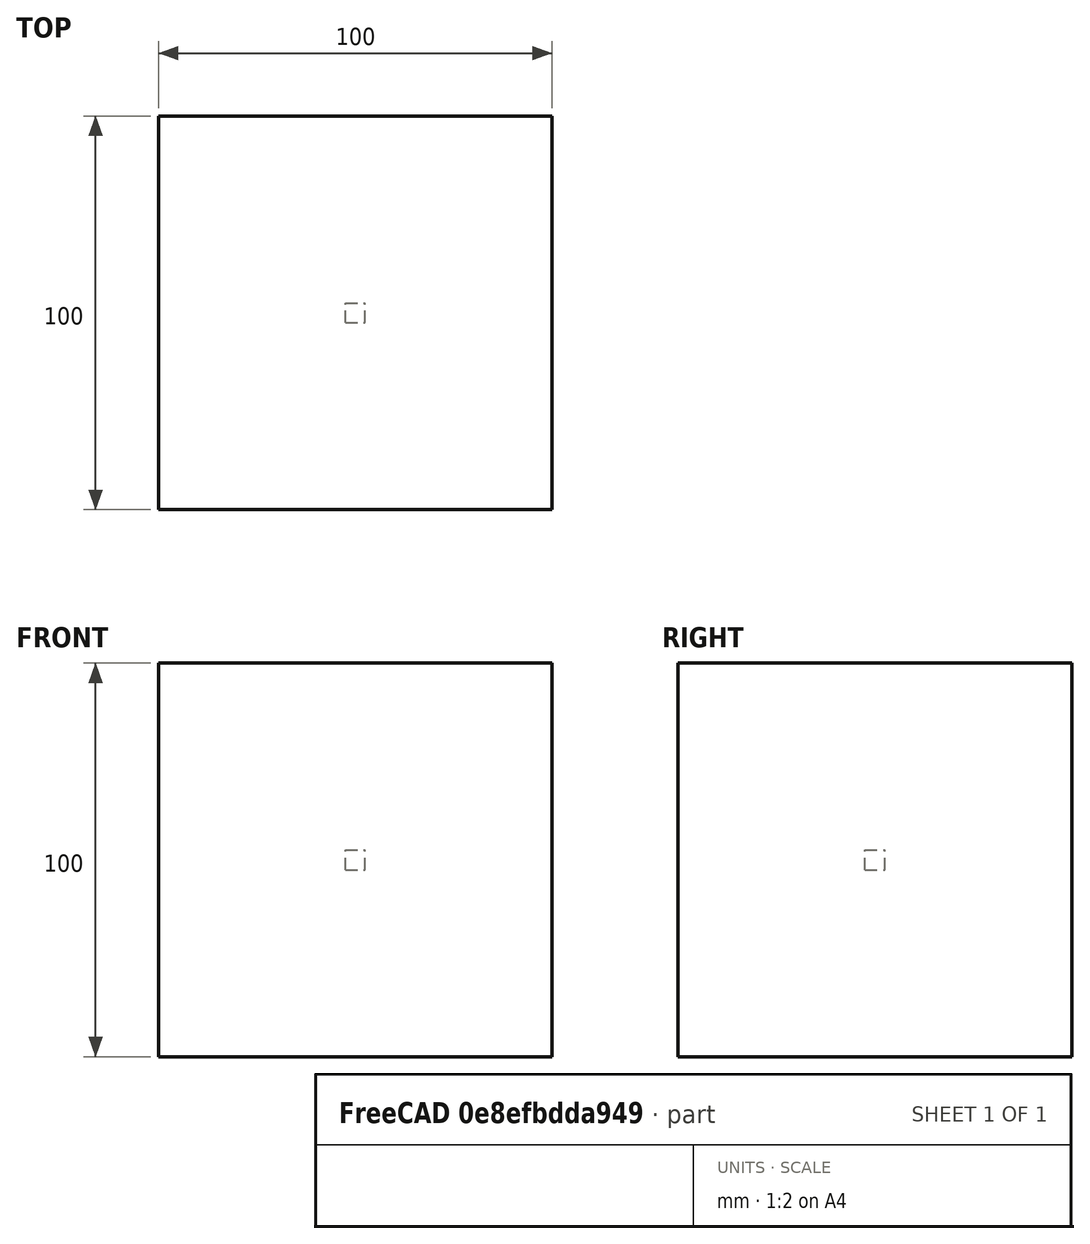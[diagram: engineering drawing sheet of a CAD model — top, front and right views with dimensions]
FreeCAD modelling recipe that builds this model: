
FCSTD DOCUMENT  (FreeCAD 1.0R39109 (Git))
Label: arrayTest-1-a
License: All rights reserved
LicenseURL: http://en.wikipedia.org/wiki/All_rights_reserved
objects: App::DocumentObjectGroupPython×1248, Part::FeaturePython×4, App::Part×4
note: 4 computed .brp shape members not serialized (recipe doc carries the construction recipe); baked Part::Feature solids carry a one-line shape summary decoded from their .brp

FEATURE [App::DocumentObjectGroupPython] HALFPI  # scripted group (container) (typed FeaturePython)
  name = HALFPI
  value = pi/2.
FEATURE [App::DocumentObjectGroupPython] PI  # scripted group (container) (typed FeaturePython)
  name = PI
  value = 1.*pi
FEATURE [App::DocumentObjectGroupPython] TWOPI  # scripted group (container) (typed FeaturePython)
  name = TWOPI
  value = 2.*pi
FEATURE [App::DocumentObjectGroupPython] Constants  # scripted group (container) (typed FeaturePython)
  Group = -> [HALFPI,PI,TWOPI]
FEATURE [App::DocumentObjectGroupPython] Variables  # scripted group (container) (typed FeaturePython)
FEATURE [App::DocumentObjectGroupPython] Quantities  # scripted group (container) (typed FeaturePython)
FEATURE [App::DocumentObjectGroupPython] Isotopes  # scripted group (container) (typed FeaturePython)
FEATURE [App::DocumentObjectGroupPython] Elements  # scripted group (container) (typed FeaturePython)
FEATURE [App::DocumentObjectGroupPython] G4Isotopes  # scripted group (container) (typed FeaturePython)
FEATURE [App::DocumentObjectGroupPython] H_element  # scripted group (container) (typed FeaturePython)
  Z = 1
  atom_value = 1.008
  formula = H
  name = H_element
FEATURE [App::DocumentObjectGroupPython] He_element  # scripted group (container) (typed FeaturePython)
  Z = 2
  atom_value = 4.0026
  formula = He
  name = He_element
FEATURE [App::DocumentObjectGroupPython] Li_element  # scripted group (container) (typed FeaturePython)
  Z = 3
  atom_value = 6.94
  formula = Li
  name = Li_element
FEATURE [App::DocumentObjectGroupPython] Be_element  # scripted group (container) (typed FeaturePython)
  Z = 4
  atom_value = 9.01218
  formula = Be
  name = Be_element
FEATURE [App::DocumentObjectGroupPython] B_element  # scripted group (container) (typed FeaturePython)
  Z = 5
  atom_value = 10.81
  formula = B
  name = B_element
FEATURE [App::DocumentObjectGroupPython] C_element  # scripted group (container) (typed FeaturePython)
  Z = 6
  atom_value = 12.011
  formula = C
  name = C_element
FEATURE [App::DocumentObjectGroupPython] N_element  # scripted group (container) (typed FeaturePython)
  Z = 7
  atom_value = 14.007
  formula = N
  name = N_element
FEATURE [App::DocumentObjectGroupPython] O_element  # scripted group (container) (typed FeaturePython)
  Z = 8
  atom_value = 15.999
  formula = O
  name = O_element
FEATURE [App::DocumentObjectGroupPython] F_element  # scripted group (container) (typed FeaturePython)
  Z = 9
  atom_value = 18.9984
  formula = F
  name = F_element
FEATURE [App::DocumentObjectGroupPython] Ne_element  # scripted group (container) (typed FeaturePython)
  Z = 10
  atom_value = 20.1797
  formula = Ne
  name = Ne_element
FEATURE [App::DocumentObjectGroupPython] Na_element  # scripted group (container) (typed FeaturePython)
  Z = 11
  atom_value = 22.9898
  formula = Na
  name = Na_element
FEATURE [App::DocumentObjectGroupPython] Mg_element  # scripted group (container) (typed FeaturePython)
  Z = 12
  atom_value = 24.305
  formula = Mg
  name = Mg_element
FEATURE [App::DocumentObjectGroupPython] Al_element  # scripted group (container) (typed FeaturePython)
  Z = 13
  atom_value = 26.9815
  formula = Al
  name = Al_element
FEATURE [App::DocumentObjectGroupPython] Si_element  # scripted group (container) (typed FeaturePython)
  Z = 14
  atom_value = 28.085
  formula = Si
  name = Si_element
FEATURE [App::DocumentObjectGroupPython] P_element  # scripted group (container) (typed FeaturePython)
  Z = 15
  atom_value = 30.9738
  formula = P
  name = P_element
FEATURE [App::DocumentObjectGroupPython] S_element  # scripted group (container) (typed FeaturePython)
  Z = 16
  atom_value = 32.06
  formula = S
  name = S_element
FEATURE [App::DocumentObjectGroupPython] Cl_element  # scripted group (container) (typed FeaturePython)
  Z = 17
  atom_value = 35.45
  formula = Cl
  name = Cl_element
FEATURE [App::DocumentObjectGroupPython] Ar_element  # scripted group (container) (typed FeaturePython)
  Z = 18
  atom_value = 39.95
  formula = Ar
  name = Ar_element
FEATURE [App::DocumentObjectGroupPython] K_element  # scripted group (container) (typed FeaturePython)
  Z = 19
  atom_value = 39.0983
  formula = K
  name = K_element
FEATURE [App::DocumentObjectGroupPython] Ca_element  # scripted group (container) (typed FeaturePython)
  Z = 20
  atom_value = 40.078
  formula = Ca
  name = Ca_element
FEATURE [App::DocumentObjectGroupPython] Sc_element  # scripted group (container) (typed FeaturePython)
  Z = 21
  atom_value = 44.9559
  formula = Sc
  name = Sc_element
FEATURE [App::DocumentObjectGroupPython] Ti_element  # scripted group (container) (typed FeaturePython)
  Z = 22
  atom_value = 47.867
  formula = Ti
  name = Ti_element
FEATURE [App::DocumentObjectGroupPython] V_element  # scripted group (container) (typed FeaturePython)
  Z = 23
  atom_value = 50.9415
  formula = V
  name = V_element
FEATURE [App::DocumentObjectGroupPython] Cr_element  # scripted group (container) (typed FeaturePython)
  Z = 24
  atom_value = 51.9961
  formula = Cr
  name = Cr_element
FEATURE [App::DocumentObjectGroupPython] Mn_element  # scripted group (container) (typed FeaturePython)
  Z = 25
  atom_value = 54.938
  formula = Mn
  name = Mn_element
FEATURE [App::DocumentObjectGroupPython] Fe_element  # scripted group (container) (typed FeaturePython)
  Z = 26
  atom_value = 55.845
  formula = Fe
  name = Fe_element
FEATURE [App::DocumentObjectGroupPython] Co_element  # scripted group (container) (typed FeaturePython)
  Z = 27
  atom_value = 58.9332
  formula = Co
  name = Co_element
FEATURE [App::DocumentObjectGroupPython] Ni_element  # scripted group (container) (typed FeaturePython)
  Z = 28
  atom_value = 58.6934
  formula = Ni
  name = Ni_element
FEATURE [App::DocumentObjectGroupPython] Cu_element  # scripted group (container) (typed FeaturePython)
  Z = 29
  atom_value = 63.546
  formula = Cu
  name = Cu_element
FEATURE [App::DocumentObjectGroupPython] Zn_element  # scripted group (container) (typed FeaturePython)
  Z = 30
  atom_value = 65.38
  formula = Zn
  name = Zn_element
FEATURE [App::DocumentObjectGroupPython] Ga_element  # scripted group (container) (typed FeaturePython)
  Z = 31
  atom_value = 69.723
  formula = Ga
  name = Ga_element
FEATURE [App::DocumentObjectGroupPython] Ge_element  # scripted group (container) (typed FeaturePython)
  Z = 32
  atom_value = 72.63
  formula = Ge
  name = Ge_element
FEATURE [App::DocumentObjectGroupPython] As_element  # scripted group (container) (typed FeaturePython)
  Z = 33
  atom_value = 74.9216
  formula = As
  name = As_element
FEATURE [App::DocumentObjectGroupPython] Se_element  # scripted group (container) (typed FeaturePython)
  Z = 34
  atom_value = 78.971
  formula = Se
  name = Se_element
FEATURE [App::DocumentObjectGroupPython] Br_element  # scripted group (container) (typed FeaturePython)
  Z = 35
  atom_value = 79.904
  formula = Br
  name = Br_element
FEATURE [App::DocumentObjectGroupPython] Kr_element  # scripted group (container) (typed FeaturePython)
  Z = 36
  atom_value = 83.798
  formula = Kr
  name = Kr_element
FEATURE [App::DocumentObjectGroupPython] Rb_element  # scripted group (container) (typed FeaturePython)
  Z = 37
  atom_value = 85.4678
  formula = Rb
  name = Rb_element
FEATURE [App::DocumentObjectGroupPython] Sr_element  # scripted group (container) (typed FeaturePython)
  Z = 38
  atom_value = 87.62
  formula = Sr
  name = Sr_element
FEATURE [App::DocumentObjectGroupPython] Y_element  # scripted group (container) (typed FeaturePython)
  Z = 39
  atom_value = 88.9058
  formula = Y
  name = Y_element
FEATURE [App::DocumentObjectGroupPython] Zr_element  # scripted group (container) (typed FeaturePython)
  Z = 40
  atom_value = 91.224
  formula = Zr
  name = Zr_element
FEATURE [App::DocumentObjectGroupPython] Nb_element  # scripted group (container) (typed FeaturePython)
  Z = 41
  atom_value = 92.9064
  formula = Nb
  name = Nb_element
FEATURE [App::DocumentObjectGroupPython] Mo_element  # scripted group (container) (typed FeaturePython)
  Z = 42
  atom_value = 95.95
  formula = Mo
  name = Mo_element
FEATURE [App::DocumentObjectGroupPython] Tc_element  # scripted group (container) (typed FeaturePython)
  Z = 43
  atom_value = 97
  formula = Tc
  name = Tc_element
FEATURE [App::DocumentObjectGroupPython] Ru_element  # scripted group (container) (typed FeaturePython)
  Z = 44
  atom_value = 101.07
  formula = Ru
  name = Ru_element
FEATURE [App::DocumentObjectGroupPython] Rh_element  # scripted group (container) (typed FeaturePython)
  Z = 45
  atom_value = 102.905
  formula = Rh
  name = Rh_element
FEATURE [App::DocumentObjectGroupPython] Pd_element  # scripted group (container) (typed FeaturePython)
  Z = 46
  atom_value = 106.42
  formula = Pd
  name = Pd_element
FEATURE [App::DocumentObjectGroupPython] Ag_element  # scripted group (container) (typed FeaturePython)
  Z = 47
  atom_value = 107.868
  formula = Ag
  name = Ag_element
FEATURE [App::DocumentObjectGroupPython] Cd_element  # scripted group (container) (typed FeaturePython)
  Z = 48
  atom_value = 112.414
  formula = Cd
  name = Cd_element
FEATURE [App::DocumentObjectGroupPython] In_element  # scripted group (container) (typed FeaturePython)
  Z = 49
  atom_value = 114.818
  formula = In
  name = In_element
FEATURE [App::DocumentObjectGroupPython] Sn_element  # scripted group (container) (typed FeaturePython)
  Z = 50
  atom_value = 118.71
  formula = Sn
  name = Sn_element
FEATURE [App::DocumentObjectGroupPython] Sb_element  # scripted group (container) (typed FeaturePython)
  Z = 51
  atom_value = 121.76
  formula = Sb
  name = Sb_element
FEATURE [App::DocumentObjectGroupPython] Te_element  # scripted group (container) (typed FeaturePython)
  Z = 52
  atom_value = 127.6
  formula = Te
  name = Te_element
FEATURE [App::DocumentObjectGroupPython] I_element  # scripted group (container) (typed FeaturePython)
  Z = 53
  atom_value = 126.904
  formula = I
  name = I_element
FEATURE [App::DocumentObjectGroupPython] Xe_element  # scripted group (container) (typed FeaturePython)
  Z = 54
  atom_value = 131.293
  formula = Xe
  name = Xe_element
FEATURE [App::DocumentObjectGroupPython] Cs_element  # scripted group (container) (typed FeaturePython)
  Z = 55
  atom_value = 132.905
  formula = Cs
  name = Cs_element
FEATURE [App::DocumentObjectGroupPython] Ba_element  # scripted group (container) (typed FeaturePython)
  Z = 56
  atom_value = 137.327
  formula = Ba
  name = Ba_element
FEATURE [App::DocumentObjectGroupPython] La_element  # scripted group (container) (typed FeaturePython)
  Z = 57
  atom_value = 138.905
  formula = La
  name = La_element
FEATURE [App::DocumentObjectGroupPython] Ce_element  # scripted group (container) (typed FeaturePython)
  Z = 58
  atom_value = 140.116
  formula = Ce
  name = Ce_element
FEATURE [App::DocumentObjectGroupPython] Pr_element  # scripted group (container) (typed FeaturePython)
  Z = 59
  atom_value = 140.908
  formula = Pr
  name = Pr_element
FEATURE [App::DocumentObjectGroupPython] Nd_element  # scripted group (container) (typed FeaturePython)
  Z = 60
  atom_value = 144.242
  formula = Nd
  name = Nd_element
FEATURE [App::DocumentObjectGroupPython] Pm_element  # scripted group (container) (typed FeaturePython)
  Z = 61
  atom_value = 145
  formula = Pm
  name = Pm_element
FEATURE [App::DocumentObjectGroupPython] Sm_element  # scripted group (container) (typed FeaturePython)
  Z = 62
  atom_value = 150.36
  formula = Sm
  name = Sm_element
FEATURE [App::DocumentObjectGroupPython] Eu_element  # scripted group (container) (typed FeaturePython)
  Z = 63
  atom_value = 151.964
  formula = Eu
  name = Eu_element
FEATURE [App::DocumentObjectGroupPython] Gd_element  # scripted group (container) (typed FeaturePython)
  Z = 64
  atom_value = 157.25
  formula = Gd
  name = Gd_element
FEATURE [App::DocumentObjectGroupPython] Tb_element  # scripted group (container) (typed FeaturePython)
  Z = 65
  atom_value = 158.925
  formula = Tb
  name = Tb_element
FEATURE [App::DocumentObjectGroupPython] Dy_element  # scripted group (container) (typed FeaturePython)
  Z = 66
  atom_value = 162.5
  formula = Dy
  name = Dy_element
FEATURE [App::DocumentObjectGroupPython] Ho_element  # scripted group (container) (typed FeaturePython)
  Z = 67
  atom_value = 164.93
  formula = Ho
  name = Ho_element
FEATURE [App::DocumentObjectGroupPython] Er_element  # scripted group (container) (typed FeaturePython)
  Z = 68
  atom_value = 167.259
  formula = Er
  name = Er_element
FEATURE [App::DocumentObjectGroupPython] Tm_element  # scripted group (container) (typed FeaturePython)
  Z = 69
  atom_value = 168.934
  formula = Tm
  name = Tm_element
FEATURE [App::DocumentObjectGroupPython] Yb_element  # scripted group (container) (typed FeaturePython)
  Z = 70
  atom_value = 173.045
  formula = Yb
  name = Yb_element
FEATURE [App::DocumentObjectGroupPython] Lu_element  # scripted group (container) (typed FeaturePython)
  Z = 71
  atom_value = 174.967
  formula = Lu
  name = Lu_element
FEATURE [App::DocumentObjectGroupPython] Hf_element  # scripted group (container) (typed FeaturePython)
  Z = 72
  atom_value = 178.49
  formula = Hf
  name = Hf_element
FEATURE [App::DocumentObjectGroupPython] Ta_element  # scripted group (container) (typed FeaturePython)
  Z = 73
  atom_value = 180.948
  formula = Ta
  name = Ta_element
FEATURE [App::DocumentObjectGroupPython] W_element  # scripted group (container) (typed FeaturePython)
  Z = 74
  atom_value = 183.84
  formula = W
  name = W_element
FEATURE [App::DocumentObjectGroupPython] Re_element  # scripted group (container) (typed FeaturePython)
  Z = 75
  atom_value = 186.207
  formula = Re
  name = Re_element
FEATURE [App::DocumentObjectGroupPython] Os_element  # scripted group (container) (typed FeaturePython)
  Z = 76
  atom_value = 190.23
  formula = Os
  name = Os_element
FEATURE [App::DocumentObjectGroupPython] Ir_element  # scripted group (container) (typed FeaturePython)
  Z = 77
  atom_value = 192.217
  formula = Ir
  name = Ir_element
FEATURE [App::DocumentObjectGroupPython] Pt_element  # scripted group (container) (typed FeaturePython)
  Z = 78
  atom_value = 195.084
  formula = Pt
  name = Pt_element
FEATURE [App::DocumentObjectGroupPython] Au_element  # scripted group (container) (typed FeaturePython)
  Z = 79
  atom_value = 196.967
  formula = Au
  name = Au_element
FEATURE [App::DocumentObjectGroupPython] Hg_element  # scripted group (container) (typed FeaturePython)
  Z = 80
  atom_value = 200.592
  formula = Hg
  name = Hg_element
FEATURE [App::DocumentObjectGroupPython] Tl_element  # scripted group (container) (typed FeaturePython)
  Z = 81
  atom_value = 204.38
  formula = Tl
  name = Tl_element
FEATURE [App::DocumentObjectGroupPython] Pb_element  # scripted group (container) (typed FeaturePython)
  Z = 82
  atom_value = 207.2
  formula = Pb
  name = Pb_element
FEATURE [App::DocumentObjectGroupPython] Bi_element  # scripted group (container) (typed FeaturePython)
  Z = 83
  atom_value = 208.98
  formula = Bi
  name = Bi_element
FEATURE [App::DocumentObjectGroupPython] Po_element  # scripted group (container) (typed FeaturePython)
  Z = 84
  atom_value = 209
  formula = Po
  name = Po_element
FEATURE [App::DocumentObjectGroupPython] At_element  # scripted group (container) (typed FeaturePython)
  Z = 85
  atom_value = 210
  formula = At
  name = At_element
FEATURE [App::DocumentObjectGroupPython] Rn_element  # scripted group (container) (typed FeaturePython)
  Z = 86
  atom_value = 222
  formula = Rn
  name = Rn_element
FEATURE [App::DocumentObjectGroupPython] Fr_element  # scripted group (container) (typed FeaturePython)
  Z = 87
  atom_value = 223
  formula = Fr
  name = Fr_element
FEATURE [App::DocumentObjectGroupPython] Ra_element  # scripted group (container) (typed FeaturePython)
  Z = 88
  atom_value = 226
  formula = Ra
  name = Ra_element
FEATURE [App::DocumentObjectGroupPython] Ac_element  # scripted group (container) (typed FeaturePython)
  Z = 89
  atom_value = 227
  formula = Ac
  name = Ac_element
FEATURE [App::DocumentObjectGroupPython] Th_element  # scripted group (container) (typed FeaturePython)
  Z = 90
  atom_value = 232.038
  formula = Th
  name = Th_element
FEATURE [App::DocumentObjectGroupPython] Pa_element  # scripted group (container) (typed FeaturePython)
  Z = 91
  atom_value = 231.036
  formula = Pa
  name = Pa_element
FEATURE [App::DocumentObjectGroupPython] U_element  # scripted group (container) (typed FeaturePython)
  Z = 92
  atom_value = 238.029
  formula = U
  name = U_element
FEATURE [App::DocumentObjectGroupPython] Np_element  # scripted group (container) (typed FeaturePython)
  Z = 93
  atom_value = 237
  formula = Np
  name = Np_element
FEATURE [App::DocumentObjectGroupPython] Pu_element  # scripted group (container) (typed FeaturePython)
  Z = 94
  atom_value = 244
  formula = Pu
  name = Pu_element
FEATURE [App::DocumentObjectGroupPython] Am_element  # scripted group (container) (typed FeaturePython)
  Z = 95
  atom_value = 243
  formula = Am
  name = Am_element
FEATURE [App::DocumentObjectGroupPython] Cm_element  # scripted group (container) (typed FeaturePython)
  Z = 96
  atom_value = 247
  formula = Cm
  name = Cm_element
FEATURE [App::DocumentObjectGroupPython] Bk_element  # scripted group (container) (typed FeaturePython)
  Z = 97
  atom_value = 247
  formula = Bk
  name = Bk_element
FEATURE [App::DocumentObjectGroupPython] Cf_element  # scripted group (container) (typed FeaturePython)
  Z = 98
  atom_value = 251
  formula = Cf
  name = Cf_element
FEATURE [App::DocumentObjectGroupPython] G4Elements  # scripted group (container) (typed FeaturePython)
  Group = -> [H_element,He_element,Li_element,Be_element,B_element,C_element,N_element,O_element,F_element,Ne_element,Na_element,Mg_element,Al_element,Si_element,P_element,S_element,Cl_element,Ar_element,K_element,Ca_element,Sc_element,Ti_element,V_element,Cr_element,Mn_element,Fe_element,Co_element,Ni_element,Cu_element,Zn_element,Ga_element,Ge_element,As_element,Se_element,Br_element,Kr_element,Rb_element,+61 more]
FEATURE [App::DocumentObjectGroupPython] H_element001  label="H_element : 0.101"  # scripted group (container) (typed FeaturePython)
  n = 0.101327
FEATURE [App::DocumentObjectGroupPython] C_element001  label="C_element : 0.775"  # scripted group (container) (typed FeaturePython)
  n = 0.7755
FEATURE [App::DocumentObjectGroupPython] N_element001  label="N_element : 0.035"  # scripted group (container) (typed FeaturePython)
  n = 0.035057
FEATURE [App::DocumentObjectGroupPython] O_element001  label="O_element : 0.052"  # scripted group (container) (typed FeaturePython)
  n = 0.0523159
FEATURE [App::DocumentObjectGroupPython] F_element001  label="F_element : 0.017"  # scripted group (container) (typed FeaturePython)
  n = 0.017422
FEATURE [App::DocumentObjectGroupPython] Ca_element001  label="Ca_element : 0.018"  # scripted group (container) (typed FeaturePython)
  n = 0.018378
FEATURE [App::DocumentObjectGroupPython] G4_A_150_TISSUE  label="G4_A-150_TISSUE"  # scripted group (container) (typed FeaturePython)
  Dunit = g/cm3
  Dvalue = 1.127
  Group = -> [H_element001,C_element001,N_element001,O_element001,F_element001,Ca_element001]
  conduct = 2
  density = 1
  expand = 3
  formula = G4_A-150_TISSUE
  name = G4_A-150_TISSUE
  specific = 4
FEATURE [App::DocumentObjectGroupPython] C_element002  label="C_element : 3"  # scripted group (container) (typed FeaturePython)
  n = 3
  ref = C_element
FEATURE [App::DocumentObjectGroupPython] H_element002  label="H_element : 6"  # scripted group (container) (typed FeaturePython)
  n = 6
  ref = H_element
FEATURE [App::DocumentObjectGroupPython] O_element002  label="O_element : 1"  # scripted group (container) (typed FeaturePython)
  n = 1
  ref = O_element
FEATURE [App::DocumentObjectGroupPython] G4_ACETONE  # scripted group (container) (typed FeaturePython)
  Dunit = g/cm3
  Dvalue = 0.7899
  Group = -> [C_element002,H_element002,O_element002]
  conduct = 2
  density = 1
  expand = 3
  formula = G4_ACETONE
  name = G4_ACETONE
  specific = 4
FEATURE [App::DocumentObjectGroupPython] C_element003  label="C_element : 2"  # scripted group (container) (typed FeaturePython)
  n = 2
  ref = C_element
FEATURE [App::DocumentObjectGroupPython] H_element003  label="H_element : 2"  # scripted group (container) (typed FeaturePython)
  n = 2
  ref = H_element
FEATURE [App::DocumentObjectGroupPython] G4_ACETYLENE  # scripted group (container) (typed FeaturePython)
  Dunit = g/cm3
  Dvalue = 0.0010967
  Group = -> [C_element003,H_element003]
  conduct = 2
  density = 1
  expand = 3
  formula = G4_ACETYLENE
  name = G4_ACETYLENE
  specific = 4
FEATURE [App::DocumentObjectGroupPython] C_element004  label="C_element : 5"  # scripted group (container) (typed FeaturePython)
  n = 5
  ref = C_element
FEATURE [App::DocumentObjectGroupPython] H_element004  label="H_element : 5"  # scripted group (container) (typed FeaturePython)
  n = 5
  ref = H_element
FEATURE [App::DocumentObjectGroupPython] N_element002  label="N_element : 5"  # scripted group (container) (typed FeaturePython)
  n = 5
  ref = N_element
FEATURE [App::DocumentObjectGroupPython] G4_ADENINE  # scripted group (container) (typed FeaturePython)
  Dunit = g/cm3
  Dvalue = 1.6
  Group = -> [C_element004,H_element004,N_element002]
  conduct = 2
  density = 1
  expand = 3
  formula = G4_ADENINE
  name = G4_ADENINE
  specific = 4
FEATURE [App::DocumentObjectGroupPython] H_element005  label="H_element : 0.114"  # scripted group (container) (typed FeaturePython)
  n = 0.114
FEATURE [App::DocumentObjectGroupPython] C_element005  label="C_element : 0.598"  # scripted group (container) (typed FeaturePython)
  n = 0.598
FEATURE [App::DocumentObjectGroupPython] N_element003  label="N_element : 0.007"  # scripted group (container) (typed FeaturePython)
  n = 0.007
FEATURE [App::DocumentObjectGroupPython] O_element003  label="O_element : 0.278"  # scripted group (container) (typed FeaturePython)
  n = 0.278
FEATURE [App::DocumentObjectGroupPython] Na_element001  label="Na_element : 0.001"  # scripted group (container) (typed FeaturePython)
  n = 0.001
FEATURE [App::DocumentObjectGroupPython] S_element001  label="S_element : 0.001"  # scripted group (container) (typed FeaturePython)
  n = 0.001
FEATURE [App::DocumentObjectGroupPython] Cl_element001  label="Cl_element : 0.001"  # scripted group (container) (typed FeaturePython)
  n = 0.001
FEATURE [App::DocumentObjectGroupPython] G4_ADIPOSE_TISSUE_ICRP  # scripted group (container) (typed FeaturePython)
  Dunit = g/cm3
  Dvalue = 0.95
  Group = -> [H_element005,C_element005,N_element003,O_element003,Na_element001,S_element001,Cl_element001]
  conduct = 2
  density = 1
  expand = 3
  formula = G4_ADIPOSE_TISSUE_ICRP
  name = G4_ADIPOSE_TISSUE_ICRP
  specific = 4
FEATURE [App::DocumentObjectGroupPython] C_element006  label="C_element : 0.000"  # scripted group (container) (typed FeaturePython)
  n = 0.000124
FEATURE [App::DocumentObjectGroupPython] N_element004  label="N_element : 0.755"  # scripted group (container) (typed FeaturePython)
  n = 0.755268
FEATURE [App::DocumentObjectGroupPython] O_element004  label="O_element : 0.232"  # scripted group (container) (typed FeaturePython)
  n = 0.231781
FEATURE [App::DocumentObjectGroupPython] Ar_element001  label="Ar_element : 0.013"  # scripted group (container) (typed FeaturePython)
  n = 0.012827
FEATURE [App::DocumentObjectGroupPython] G4_AIR  # scripted group (container) (typed FeaturePython)
  Dunit = g/cm3
  Dvalue = 0.00120479
  Group = -> [C_element006,N_element004,O_element004,Ar_element001]
  conduct = 2
  density = 1
  expand = 3
  formula = G4_AIR
  name = G4_AIR
  specific = 4
FEATURE [App::DocumentObjectGroupPython] C_element007  label="C_element : 006"  # scripted group (container) (typed FeaturePython)
  n = 3
  ref = C_element
FEATURE [App::DocumentObjectGroupPython] H_element006  label="H_element : 7"  # scripted group (container) (typed FeaturePython)
  n = 7
  ref = H_element
FEATURE [App::DocumentObjectGroupPython] N_element005  label="N_element : 1"  # scripted group (container) (typed FeaturePython)
  n = 1
  ref = N_element
FEATURE [App::DocumentObjectGroupPython] O_element005  label="O_element : 2"  # scripted group (container) (typed FeaturePython)
  n = 2
  ref = O_element
FEATURE [App::DocumentObjectGroupPython] G4_ALANINE  # scripted group (container) (typed FeaturePython)
  Dunit = g/cm3
  Dvalue = 1.42
  Group = -> [C_element007,H_element006,N_element005,O_element005]
  conduct = 2
  density = 1
  expand = 3
  formula = G4_ALANINE
  name = G4_ALANINE
  specific = 4
FEATURE [App::DocumentObjectGroupPython] Al_element001  label="Al_element : 2"  # scripted group (container) (typed FeaturePython)
  n = 2
  ref = Al_element
FEATURE [App::DocumentObjectGroupPython] O_element006  label="O_element : 3"  # scripted group (container) (typed FeaturePython)
  n = 3
  ref = O_element
FEATURE [App::DocumentObjectGroupPython] G4_ALUMINUM_OXIDE  # scripted group (container) (typed FeaturePython)
  Dunit = g/cm3
  Dvalue = 3.97
  Group = -> [Al_element001,O_element006]
  conduct = 2
  density = 1
  expand = 3
  formula = G4_ALUMINUM_OXIDE
  name = G4_ALUMINUM_OXIDE
  specific = 4
FEATURE [App::DocumentObjectGroupPython] H_element007  label="H_element : 0.106"  # scripted group (container) (typed FeaturePython)
  n = 0.10593
FEATURE [App::DocumentObjectGroupPython] C_element008  label="C_element : 0.789"  # scripted group (container) (typed FeaturePython)
  n = 0.788974
FEATURE [App::DocumentObjectGroupPython] O_element007  label="O_element : 0.105"  # scripted group (container) (typed FeaturePython)
  n = 0.105096
FEATURE [App::DocumentObjectGroupPython] G4_AMBER  # scripted group (container) (typed FeaturePython)
  Dunit = g/cm3
  Dvalue = 1.1
  Group = -> [H_element007,C_element008,O_element007]
  conduct = 2
  density = 1
  expand = 3
  formula = G4_AMBER
  name = G4_AMBER
  specific = 4
FEATURE [App::DocumentObjectGroupPython] N_element006  label="N_element : 006"  # scripted group (container) (typed FeaturePython)
  n = 1
  ref = N_element
FEATURE [App::DocumentObjectGroupPython] H_element008  label="H_element : 3"  # scripted group (container) (typed FeaturePython)
  n = 3
  ref = H_element
FEATURE [App::DocumentObjectGroupPython] G4_AMMONIA  # scripted group (container) (typed FeaturePython)
  Dunit = g/cm3
  Dvalue = 0.000826019
  Group = -> [N_element006,H_element008]
  conduct = 2
  density = 1
  expand = 3
  formula = G4_AMMONIA
  name = G4_AMMONIA
  specific = 4
FEATURE [App::DocumentObjectGroupPython] C_element009  label="C_element : 6"  # scripted group (container) (typed FeaturePython)
  n = 6
  ref = C_element
FEATURE [App::DocumentObjectGroupPython] H_element009  label="H_element : 008"  # scripted group (container) (typed FeaturePython)
  n = 7
  ref = H_element
FEATURE [App::DocumentObjectGroupPython] N_element007  label="N_element : 007"  # scripted group (container) (typed FeaturePython)
  n = 1
  ref = N_element
FEATURE [App::DocumentObjectGroupPython] G4_ANILINE  # scripted group (container) (typed FeaturePython)
  Dunit = g/cm3
  Dvalue = 1.0235
  Group = -> [C_element009,H_element009,N_element007]
  conduct = 2
  density = 1
  expand = 3
  formula = G4_ANILINE
  name = G4_ANILINE
  specific = 4
FEATURE [App::DocumentObjectGroupPython] C_element010  label="C_element : 14"  # scripted group (container) (typed FeaturePython)
  n = 14
  ref = C_element
FEATURE [App::DocumentObjectGroupPython] H_element010  label="H_element : 10"  # scripted group (container) (typed FeaturePython)
  n = 10
  ref = H_element
FEATURE [App::DocumentObjectGroupPython] G4_ANTHRACENE  # scripted group (container) (typed FeaturePython)
  Dunit = g/cm3
  Dvalue = 1.283
  Group = -> [C_element010,H_element010]
  conduct = 2
  density = 1
  expand = 3
  formula = G4_ANTHRACENE
  name = G4_ANTHRACENE
  specific = 4
FEATURE [App::DocumentObjectGroupPython] H_element011  label="H_element : 0.065"  # scripted group (container) (typed FeaturePython)
  n = 0.0654709
FEATURE [App::DocumentObjectGroupPython] C_element011  label="C_element : 0.537"  # scripted group (container) (typed FeaturePython)
  n = 0.536944
FEATURE [App::DocumentObjectGroupPython] N_element008  label="N_element : 0.021"  # scripted group (container) (typed FeaturePython)
  n = 0.0215
FEATURE [App::DocumentObjectGroupPython] O_element008  label="O_element : 0.032"  # scripted group (container) (typed FeaturePython)
  n = 0.032085
FEATURE [App::DocumentObjectGroupPython] F_element002  label="F_element : 0.167"  # scripted group (container) (typed FeaturePython)
  n = 0.167411
FEATURE [App::DocumentObjectGroupPython] Ca_element002  label="Ca_element : 0.177"  # scripted group (container) (typed FeaturePython)
  n = 0.176589
FEATURE [App::DocumentObjectGroupPython] G4_B_100_BONE  label="G4_B-100_BONE"  # scripted group (container) (typed FeaturePython)
  Dunit = g/cm3
  Dvalue = 1.45
  Group = -> [H_element011,C_element011,N_element008,O_element008,F_element002,Ca_element002]
  conduct = 2
  density = 1
  expand = 3
  formula = G4_B-100_BONE
  name = G4_B-100_BONE
  specific = 4
FEATURE [App::DocumentObjectGroupPython] H_element012  label="H_element : 0.057"  # scripted group (container) (typed FeaturePython)
  n = 0.057441
FEATURE [App::DocumentObjectGroupPython] C_element012  label="C_element : 0.790"  # scripted group (container) (typed FeaturePython)
  n = 0.774591
FEATURE [App::DocumentObjectGroupPython] O_element009  label="O_element : 0.168"  # scripted group (container) (typed FeaturePython)
  n = 0.167968
FEATURE [App::DocumentObjectGroupPython] G4_BAKELITE  # scripted group (container) (typed FeaturePython)
  Dunit = g/cm3
  Dvalue = 1.25
  Group = -> [H_element012,C_element012,O_element009]
  conduct = 2
  density = 1
  expand = 3
  formula = G4_BAKELITE
  name = G4_BAKELITE
  specific = 4
FEATURE [App::DocumentObjectGroupPython] Ba_element001  label="Ba_element : 1"  # scripted group (container) (typed FeaturePython)
  n = 1
  ref = Ba_element
FEATURE [App::DocumentObjectGroupPython] F_element003  label="F_element : 2"  # scripted group (container) (typed FeaturePython)
  n = 2
  ref = F_element
FEATURE [App::DocumentObjectGroupPython] G4_BARIUM_FLUORIDE  # scripted group (container) (typed FeaturePython)
  Dunit = g/cm3
  Dvalue = 4.89
  Group = -> [Ba_element001,F_element003]
  conduct = 2
  density = 1
  expand = 3
  formula = G4_BARIUM_FLUORIDE
  name = G4_BARIUM_FLUORIDE
  specific = 4
FEATURE [App::DocumentObjectGroupPython] Ba_element002  label="Ba_element : 002"  # scripted group (container) (typed FeaturePython)
  n = 1
  ref = Ba_element
FEATURE [App::DocumentObjectGroupPython] S_element002  label="S_element : 1"  # scripted group (container) (typed FeaturePython)
  n = 1
  ref = S_element
FEATURE [App::DocumentObjectGroupPython] O_element010  label="O_element : 4"  # scripted group (container) (typed FeaturePython)
  n = 4
  ref = O_element
FEATURE [App::DocumentObjectGroupPython] G4_BARIUM_SULFATE  # scripted group (container) (typed FeaturePython)
  Dunit = g/cm3
  Dvalue = 4.5
  Group = -> [Ba_element002,S_element002,O_element010]
  conduct = 2
  density = 1
  expand = 3
  formula = G4_BARIUM_SULFATE
  name = G4_BARIUM_SULFATE
  specific = 4
FEATURE [App::DocumentObjectGroupPython] C_element013  label="C_element : 007"  # scripted group (container) (typed FeaturePython)
  n = 6
  ref = C_element
FEATURE [App::DocumentObjectGroupPython] H_element013  label="H_element : 009"  # scripted group (container) (typed FeaturePython)
  n = 6
  ref = H_element
FEATURE [App::DocumentObjectGroupPython] G4_BENZENE  # scripted group (container) (typed FeaturePython)
  Dunit = g/cm3
  Dvalue = 0.87865
  Group = -> [C_element013,H_element013]
  conduct = 2
  density = 1
  expand = 3
  formula = G4_BENZENE
  name = G4_BENZENE
  specific = 4
FEATURE [App::DocumentObjectGroupPython] Be_element001  label="Be_element : 1"  # scripted group (container) (typed FeaturePython)
  n = 1
  ref = Be_element
FEATURE [App::DocumentObjectGroupPython] O_element011  label="O_element : 005"  # scripted group (container) (typed FeaturePython)
  n = 1
  ref = O_element
FEATURE [App::DocumentObjectGroupPython] G4_BERYLLIUM_OXIDE  # scripted group (container) (typed FeaturePython)
  Dunit = g/cm3
  Dvalue = 3.01
  Group = -> [Be_element001,O_element011]
  conduct = 2
  density = 1
  expand = 3
  formula = G4_BERYLLIUM_OXIDE
  name = G4_BERYLLIUM_OXIDE
  specific = 4
FEATURE [App::DocumentObjectGroupPython] Bi_element001  label="Bi_element : 4"  # scripted group (container) (typed FeaturePython)
  n = 4
  ref = Bi_element
FEATURE [App::DocumentObjectGroupPython] Ge_element001  label="Ge_element : 3"  # scripted group (container) (typed FeaturePython)
  n = 3
  ref = Ge_element
FEATURE [App::DocumentObjectGroupPython] O_element012  label="O_element : 12"  # scripted group (container) (typed FeaturePython)
  n = 12
  ref = O_element
FEATURE [App::DocumentObjectGroupPython] G4_BGO  # scripted group (container) (typed FeaturePython)
  Dunit = g/cm3
  Dvalue = 7.13
  Group = -> [Bi_element001,Ge_element001,O_element012]
  conduct = 2
  density = 1
  expand = 3
  formula = G4_BGO
  name = G4_BGO
  specific = 4
FEATURE [App::DocumentObjectGroupPython] H_element014  label="H_element : 0.102"  # scripted group (container) (typed FeaturePython)
  n = 0.102
FEATURE [App::DocumentObjectGroupPython] C_element014  label="C_element : 0.110"  # scripted group (container) (typed FeaturePython)
  n = 0.11
FEATURE [App::DocumentObjectGroupPython] N_element009  label="N_element : 0.033"  # scripted group (container) (typed FeaturePython)
  n = 0.033
FEATURE [App::DocumentObjectGroupPython] O_element013  label="O_element : 0.745"  # scripted group (container) (typed FeaturePython)
  n = 0.745
FEATURE [App::DocumentObjectGroupPython] Na_element002  label="Na_element : 0.002"  # scripted group (container) (typed FeaturePython)
  n = 0.001
FEATURE [App::DocumentObjectGroupPython] P_element001  label="P_element : 0.001"  # scripted group (container) (typed FeaturePython)
  n = 0.001
FEATURE [App::DocumentObjectGroupPython] S_element003  label="S_element : 0.002"  # scripted group (container) (typed FeaturePython)
  n = 0.002
FEATURE [App::DocumentObjectGroupPython] Cl_element002  label="Cl_element : 0.003"  # scripted group (container) (typed FeaturePython)
  n = 0.003
FEATURE [App::DocumentObjectGroupPython] K_element001  label="K_element : 0.002"  # scripted group (container) (typed FeaturePython)
  n = 0.002
FEATURE [App::DocumentObjectGroupPython] Fe_element001  label="Fe_element : 0.001"  # scripted group (container) (typed FeaturePython)
  n = 0.001
FEATURE [App::DocumentObjectGroupPython] G4_BLOOD_ICRP  # scripted group (container) (typed FeaturePython)
  Dunit = g/cm3
  Dvalue = 1.06
  Group = -> [H_element014,C_element014,N_element009,O_element013,Na_element002,P_element001,S_element003,Cl_element002,K_element001,Fe_element001]
  conduct = 2
  density = 1
  expand = 3
  formula = G4_BLOOD_ICRP
  name = G4_BLOOD_ICRP
  specific = 4
FEATURE [App::DocumentObjectGroupPython] H_element015  label="H_element : 0.064"  # scripted group (container) (typed FeaturePython)
  n = 0.064
FEATURE [App::DocumentObjectGroupPython] C_element015  label="C_element : 0.278"  # scripted group (container) (typed FeaturePython)
  n = 0.278
FEATURE [App::DocumentObjectGroupPython] N_element010  label="N_element : 0.027"  # scripted group (container) (typed FeaturePython)
  n = 0.027
FEATURE [App::DocumentObjectGroupPython] O_element014  label="O_element : 0.410"  # scripted group (container) (typed FeaturePython)
  n = 0.41
FEATURE [App::DocumentObjectGroupPython] Mg_element001  label="Mg_element : 0.002"  # scripted group (container) (typed FeaturePython)
  n = 0.002
FEATURE [App::DocumentObjectGroupPython] P_element002  label="P_element : 0.070"  # scripted group (container) (typed FeaturePython)
  n = 0.07
FEATURE [App::DocumentObjectGroupPython] S_element004  label="S_element : 0.003"  # scripted group (container) (typed FeaturePython)
  n = 0.002
FEATURE [App::DocumentObjectGroupPython] Ca_element003  label="Ca_element : 0.147"  # scripted group (container) (typed FeaturePython)
  n = 0.147
FEATURE [App::DocumentObjectGroupPython] G4_BONE_COMPACT_ICRU  # scripted group (container) (typed FeaturePython)
  Dunit = g/cm3
  Dvalue = 1.85
  Group = -> [H_element015,C_element015,N_element010,O_element014,Mg_element001,P_element002,S_element004,Ca_element003]
  conduct = 2
  density = 1
  expand = 3
  formula = G4_BONE_COMPACT_ICRU
  name = G4_BONE_COMPACT_ICRU
  specific = 4
FEATURE [App::DocumentObjectGroupPython] H_element016  label="H_element : 0.034"  # scripted group (container) (typed FeaturePython)
  n = 0.034
FEATURE [App::DocumentObjectGroupPython] C_element016  label="C_element : 0.155"  # scripted group (container) (typed FeaturePython)
  n = 0.155
FEATURE [App::DocumentObjectGroupPython] N_element011  label="N_element : 0.042"  # scripted group (container) (typed FeaturePython)
  n = 0.042
FEATURE [App::DocumentObjectGroupPython] O_element015  label="O_element : 0.435"  # scripted group (container) (typed FeaturePython)
  n = 0.435
FEATURE [App::DocumentObjectGroupPython] Na_element003  label="Na_element : 0.003"  # scripted group (container) (typed FeaturePython)
  n = 0.001
FEATURE [App::DocumentObjectGroupPython] Mg_element002  label="Mg_element : 0.003"  # scripted group (container) (typed FeaturePython)
  n = 0.002
FEATURE [App::DocumentObjectGroupPython] P_element003  label="P_element : 0.103"  # scripted group (container) (typed FeaturePython)
  n = 0.103
FEATURE [App::DocumentObjectGroupPython] S_element005  label="S_element : 0.004"  # scripted group (container) (typed FeaturePython)
  n = 0.003
FEATURE [App::DocumentObjectGroupPython] Ca_element004  label="Ca_element : 0.225"  # scripted group (container) (typed FeaturePython)
  n = 0.225
FEATURE [App::DocumentObjectGroupPython] G4_BONE_CORTICAL_ICRP  # scripted group (container) (typed FeaturePython)
  Dunit = g/cm3
  Dvalue = 1.92
  Group = -> [H_element016,C_element016,N_element011,O_element015,Na_element003,Mg_element002,P_element003,S_element005,Ca_element004]
  conduct = 2
  density = 1
  expand = 3
  formula = G4_BONE_CORTICAL_ICRP
  name = G4_BONE_CORTICAL_ICRP
  specific = 4
FEATURE [App::DocumentObjectGroupPython] B_element001  label="B_element : 4"  # scripted group (container) (typed FeaturePython)
  n = 4
  ref = B_element
FEATURE [App::DocumentObjectGroupPython] C_element017  label="C_element : 1"  # scripted group (container) (typed FeaturePython)
  n = 1
  ref = C_element
FEATURE [App::DocumentObjectGroupPython] G4_BORON_CARBIDE  # scripted group (container) (typed FeaturePython)
  Dunit = g/cm3
  Dvalue = 2.52
  Group = -> [B_element001,C_element017]
  conduct = 2
  density = 1
  expand = 3
  formula = G4_BORON_CARBIDE
  name = G4_BORON_CARBIDE
  specific = 4
FEATURE [App::DocumentObjectGroupPython] B_element002  label="B_element : 2"  # scripted group (container) (typed FeaturePython)
  n = 2
  ref = B_element
FEATURE [App::DocumentObjectGroupPython] O_element016  label="O_element : 006"  # scripted group (container) (typed FeaturePython)
  n = 3
  ref = O_element
FEATURE [App::DocumentObjectGroupPython] G4_BORON_OXIDE  # scripted group (container) (typed FeaturePython)
  Dunit = g/cm3
  Dvalue = 1.812
  Group = -> [B_element002,O_element016]
  conduct = 2
  density = 1
  expand = 3
  formula = G4_BORON_OXIDE
  name = G4_BORON_OXIDE
  specific = 4
FEATURE [App::DocumentObjectGroupPython] H_element017  label="H_element : 0.107"  # scripted group (container) (typed FeaturePython)
  n = 0.107
FEATURE [App::DocumentObjectGroupPython] C_element018  label="C_element : 0.145"  # scripted group (container) (typed FeaturePython)
  n = 0.145
FEATURE [App::DocumentObjectGroupPython] N_element012  label="N_element : 0.022"  # scripted group (container) (typed FeaturePython)
  n = 0.022
FEATURE [App::DocumentObjectGroupPython] O_element017  label="O_element : 0.712"  # scripted group (container) (typed FeaturePython)
  n = 0.712
FEATURE [App::DocumentObjectGroupPython] Na_element004  label="Na_element : 0.004"  # scripted group (container) (typed FeaturePython)
  n = 0.002
FEATURE [App::DocumentObjectGroupPython] P_element004  label="P_element : 0.004"  # scripted group (container) (typed FeaturePython)
  n = 0.004
FEATURE [App::DocumentObjectGroupPython] S_element006  label="S_element : 0.005"  # scripted group (container) (typed FeaturePython)
  n = 0.002
FEATURE [App::DocumentObjectGroupPython] Cl_element003  label="Cl_element : 0.004"  # scripted group (container) (typed FeaturePython)
  n = 0.003
FEATURE [App::DocumentObjectGroupPython] K_element002  label="K_element : 0.003"  # scripted group (container) (typed FeaturePython)
  n = 0.003
FEATURE [App::DocumentObjectGroupPython] G4_BRAIN_ICRP  # scripted group (container) (typed FeaturePython)
  Dunit = g/cm3
  Dvalue = 1.04
  Group = -> [H_element017,C_element018,N_element012,O_element017,Na_element004,P_element004,S_element006,Cl_element003,K_element002]
  conduct = 2
  density = 1
  expand = 3
  formula = G4_BRAIN_ICRP
  name = G4_BRAIN_ICRP
  specific = 4
FEATURE [App::DocumentObjectGroupPython] C_element019  label="C_element : 4"  # scripted group (container) (typed FeaturePython)
  n = 4
  ref = C_element
FEATURE [App::DocumentObjectGroupPython] H_element018  label="H_element : 010"  # scripted group (container) (typed FeaturePython)
  n = 10
  ref = H_element
FEATURE [App::DocumentObjectGroupPython] G4_BUTANE  # scripted group (container) (typed FeaturePython)
  Dunit = g/cm3
  Dvalue = 0.00249343
  Group = -> [C_element019,H_element018]
  conduct = 2
  density = 1
  expand = 3
  formula = G4_BUTANE
  name = G4_BUTANE
  specific = 4
FEATURE [App::DocumentObjectGroupPython] C_element020  label="C_element : 008"  # scripted group (container) (typed FeaturePython)
  n = 4
  ref = C_element
FEATURE [App::DocumentObjectGroupPython] H_element019  label="H_element : 011"  # scripted group (container) (typed FeaturePython)
  n = 10
  ref = H_element
FEATURE [App::DocumentObjectGroupPython] O_element018  label="O_element : 007"  # scripted group (container) (typed FeaturePython)
  n = 1
  ref = O_element
FEATURE [App::DocumentObjectGroupPython] G4_N_BUTYL_ALCOHOL  label="G4_N-BUTYL_ALCOHOL"  # scripted group (container) (typed FeaturePython)
  Dunit = g/cm3
  Dvalue = 0.8098
  Group = -> [C_element020,H_element019,O_element018]
  conduct = 2
  density = 1
  expand = 3
  formula = G4_N-BUTYL_ALCOHOL
  name = G4_N-BUTYL_ALCOHOL
  specific = 4
FEATURE [App::DocumentObjectGroupPython] H_element020  label="H_element : 0.025"  # scripted group (container) (typed FeaturePython)
  n = 0.02468
FEATURE [App::DocumentObjectGroupPython] C_element021  label="C_element : 0.502"  # scripted group (container) (typed FeaturePython)
  n = 0.501611
FEATURE [App::DocumentObjectGroupPython] O_element019  label="O_element : 0.005"  # scripted group (container) (typed FeaturePython)
  n = 0.004527
FEATURE [App::DocumentObjectGroupPython] F_element004  label="F_element : 0.465"  # scripted group (container) (typed FeaturePython)
  n = 0.465209
FEATURE [App::DocumentObjectGroupPython] Si_element001  label="Si_element : 0.004"  # scripted group (container) (typed FeaturePython)
  n = 0.003973
FEATURE [App::DocumentObjectGroupPython] G4_C_552  label="G4_C-552"  # scripted group (container) (typed FeaturePython)
  Dunit = g/cm3
  Dvalue = 1.76
  Group = -> [H_element020,C_element021,O_element019,F_element004,Si_element001]
  conduct = 2
  density = 1
  expand = 3
  formula = G4_C-552
  name = G4_C-552
  specific = 4
FEATURE [App::DocumentObjectGroupPython] Cd_element001  label="Cd_element : 1"  # scripted group (container) (typed FeaturePython)
  n = 1
  ref = Cd_element
FEATURE [App::DocumentObjectGroupPython] Te_element001  label="Te_element : 1"  # scripted group (container) (typed FeaturePython)
  n = 1
  ref = Te_element
FEATURE [App::DocumentObjectGroupPython] G4_CADMIUM_TELLURIDE  # scripted group (container) (typed FeaturePython)
  Dunit = g/cm3
  Dvalue = 6.2
  Group = -> [Cd_element001,Te_element001]
  conduct = 2
  density = 1
  expand = 3
  formula = G4_CADMIUM_TELLURIDE
  name = G4_CADMIUM_TELLURIDE
  specific = 4
FEATURE [App::DocumentObjectGroupPython] Cd_element002  label="Cd_element : 002"  # scripted group (container) (typed FeaturePython)
  n = 1
  ref = Cd_element
FEATURE [App::DocumentObjectGroupPython] W_element001  label="W_element : 1"  # scripted group (container) (typed FeaturePython)
  n = 1
  ref = W_element
FEATURE [App::DocumentObjectGroupPython] O_element020  label="O_element : 008"  # scripted group (container) (typed FeaturePython)
  n = 4
  ref = O_element
FEATURE [App::DocumentObjectGroupPython] G4_CADMIUM_TUNGSTATE  # scripted group (container) (typed FeaturePython)
  Dunit = g/cm3
  Dvalue = 7.9
  Group = -> [Cd_element002,W_element001,O_element020]
  conduct = 2
  density = 1
  expand = 3
  formula = G4_CADMIUM_TUNGSTATE
  name = G4_CADMIUM_TUNGSTATE
  specific = 4
FEATURE [App::DocumentObjectGroupPython] Ca_element005  label="Ca_element : 1"  # scripted group (container) (typed FeaturePython)
  n = 1
  ref = Ca_element
FEATURE [App::DocumentObjectGroupPython] C_element022  label="C_element : 009"  # scripted group (container) (typed FeaturePython)
  n = 1
  ref = C_element
FEATURE [App::DocumentObjectGroupPython] O_element021  label="O_element : 009"  # scripted group (container) (typed FeaturePython)
  n = 3
  ref = O_element
FEATURE [App::DocumentObjectGroupPython] G4_CALCIUM_CARBONATE  # scripted group (container) (typed FeaturePython)
  Dunit = g/cm3
  Dvalue = 2.8
  Group = -> [Ca_element005,C_element022,O_element021]
  conduct = 2
  density = 1
  expand = 3
  formula = G4_CALCIUM_CARBONATE
  name = G4_CALCIUM_CARBONATE
  specific = 4
FEATURE [App::DocumentObjectGroupPython] Ca_element006  label="Ca_element : 002"  # scripted group (container) (typed FeaturePython)
  n = 1
  ref = Ca_element
FEATURE [App::DocumentObjectGroupPython] F_element005  label="F_element : 003"  # scripted group (container) (typed FeaturePython)
  n = 2
  ref = F_element
FEATURE [App::DocumentObjectGroupPython] G4_CALCIUM_FLUORIDE  # scripted group (container) (typed FeaturePython)
  Dunit = g/cm3
  Dvalue = 3.18
  Group = -> [Ca_element006,F_element005]
  conduct = 2
  density = 1
  expand = 3
  formula = G4_CALCIUM_FLUORIDE
  name = G4_CALCIUM_FLUORIDE
  specific = 4
FEATURE [App::DocumentObjectGroupPython] Ca_element007  label="Ca_element : 003"  # scripted group (container) (typed FeaturePython)
  n = 1
  ref = Ca_element
FEATURE [App::DocumentObjectGroupPython] O_element022  label="O_element : 010"  # scripted group (container) (typed FeaturePython)
  n = 1
  ref = O_element
FEATURE [App::DocumentObjectGroupPython] G4_CALCIUM_OXIDE  # scripted group (container) (typed FeaturePython)
  Dunit = g/cm3
  Dvalue = 3.3
  Group = -> [Ca_element007,O_element022]
  conduct = 2
  density = 1
  expand = 3
  formula = G4_CALCIUM_OXIDE
  name = G4_CALCIUM_OXIDE
  specific = 4
FEATURE [App::DocumentObjectGroupPython] Ca_element008  label="Ca_element : 004"  # scripted group (container) (typed FeaturePython)
  n = 1
  ref = Ca_element
FEATURE [App::DocumentObjectGroupPython] S_element007  label="S_element : 002"  # scripted group (container) (typed FeaturePython)
  n = 1
  ref = S_element
FEATURE [App::DocumentObjectGroupPython] O_element023  label="O_element : 011"  # scripted group (container) (typed FeaturePython)
  n = 4
  ref = O_element
FEATURE [App::DocumentObjectGroupPython] G4_CALCIUM_SULFATE  # scripted group (container) (typed FeaturePython)
  Dunit = g/cm3
  Dvalue = 2.96
  Group = -> [Ca_element008,S_element007,O_element023]
  conduct = 2
  density = 1
  expand = 3
  formula = G4_CALCIUM_SULFATE
  name = G4_CALCIUM_SULFATE
  specific = 4
FEATURE [App::DocumentObjectGroupPython] Ca_element009  label="Ca_element : 005"  # scripted group (container) (typed FeaturePython)
  n = 1
  ref = Ca_element
FEATURE [App::DocumentObjectGroupPython] W_element002  label="W_element : 002"  # scripted group (container) (typed FeaturePython)
  n = 1
  ref = W_element
FEATURE [App::DocumentObjectGroupPython] O_element024  label="O_element : 012"  # scripted group (container) (typed FeaturePython)
  n = 4
  ref = O_element
FEATURE [App::DocumentObjectGroupPython] G4_CALCIUM_TUNGSTATE  # scripted group (container) (typed FeaturePython)
  Dunit = g/cm3
  Dvalue = 6.062
  Group = -> [Ca_element009,W_element002,O_element024]
  conduct = 2
  density = 1
  expand = 3
  formula = G4_CALCIUM_TUNGSTATE
  name = G4_CALCIUM_TUNGSTATE
  specific = 4
FEATURE [App::DocumentObjectGroupPython] C_element023  label="C_element : 010"  # scripted group (container) (typed FeaturePython)
  n = 1
  ref = C_element
FEATURE [App::DocumentObjectGroupPython] O_element025  label="O_element : 013"  # scripted group (container) (typed FeaturePython)
  n = 2
  ref = O_element
FEATURE [App::DocumentObjectGroupPython] G4_CARBON_DIOXIDE  # scripted group (container) (typed FeaturePython)
  Dunit = g/cm3
  Dvalue = 0.00184212
  Group = -> [C_element023,O_element025]
  conduct = 2
  density = 1
  expand = 3
  formula = G4_CARBON_DIOXIDE
  name = G4_CARBON_DIOXIDE
  specific = 4
FEATURE [App::DocumentObjectGroupPython] C_element024  label="C_element : 011"  # scripted group (container) (typed FeaturePython)
  n = 1
  ref = C_element
FEATURE [App::DocumentObjectGroupPython] Cl_element004  label="Cl_element : 4"  # scripted group (container) (typed FeaturePython)
  n = 4
  ref = Cl_element
FEATURE [App::DocumentObjectGroupPython] G4_CARBON_TETRACHLORIDE  # scripted group (container) (typed FeaturePython)
  Dunit = g/cm3
  Dvalue = 1.594
  Group = -> [C_element024,Cl_element004]
  conduct = 2
  density = 1
  expand = 3
  formula = G4_CARBON_TETRACHLORIDE
  name = G4_CARBON_TETRACHLORIDE
  specific = 4
FEATURE [App::DocumentObjectGroupPython] C_element025  label="C_element : 012"  # scripted group (container) (typed FeaturePython)
  n = 6
  ref = C_element
FEATURE [App::DocumentObjectGroupPython] H_element021  label="H_element : 012"  # scripted group (container) (typed FeaturePython)
  n = 10
  ref = H_element
FEATURE [App::DocumentObjectGroupPython] O_element026  label="O_element : 5"  # scripted group (container) (typed FeaturePython)
  n = 5
  ref = O_element
FEATURE [App::DocumentObjectGroupPython] G4_CELLULOSE_CELLOPHANE  # scripted group (container) (typed FeaturePython)
  Dunit = g/cm3
  Dvalue = 1.42
  Group = -> [C_element025,H_element021,O_element026]
  conduct = 2
  density = 1
  expand = 3
  formula = G4_CELLULOSE_CELLOPHANE
  name = G4_CELLULOSE_CELLOPHANE
  specific = 4
FEATURE [App::DocumentObjectGroupPython] H_element022  label="H_element : 0.067"  # scripted group (container) (typed FeaturePython)
  n = 0.067125
FEATURE [App::DocumentObjectGroupPython] C_element026  label="C_element : 0.545"  # scripted group (container) (typed FeaturePython)
  n = 0.545403
FEATURE [App::DocumentObjectGroupPython] O_element027  label="O_element : 0.387"  # scripted group (container) (typed FeaturePython)
  n = 0.387472
FEATURE [App::DocumentObjectGroupPython] G4_CELLULOSE_BUTYRATE  # scripted group (container) (typed FeaturePython)
  Dunit = g/cm3
  Dvalue = 1.2
  Group = -> [H_element022,C_element026,O_element027]
  conduct = 2
  density = 1
  expand = 3
  formula = G4_CELLULOSE_BUTYRATE
  name = G4_CELLULOSE_BUTYRATE
  specific = 4
FEATURE [App::DocumentObjectGroupPython] H_element023  label="H_element : 0.029"  # scripted group (container) (typed FeaturePython)
  n = 0.029216
FEATURE [App::DocumentObjectGroupPython] C_element027  label="C_element : 0.271"  # scripted group (container) (typed FeaturePython)
  n = 0.271296
FEATURE [App::DocumentObjectGroupPython] N_element013  label="N_element : 0.121"  # scripted group (container) (typed FeaturePython)
  n = 0.121276
FEATURE [App::DocumentObjectGroupPython] O_element028  label="O_element : 0.578"  # scripted group (container) (typed FeaturePython)
  n = 0.578212
FEATURE [App::DocumentObjectGroupPython] G4_CELLULOSE_NITRATE  # scripted group (container) (typed FeaturePython)
  Dunit = g/cm3
  Dvalue = 1.49
  Group = -> [H_element023,C_element027,N_element013,O_element028]
  conduct = 2
  density = 1
  expand = 3
  formula = G4_CELLULOSE_NITRATE
  name = G4_CELLULOSE_NITRATE
  specific = 4
FEATURE [App::DocumentObjectGroupPython] H_element024  label="H_element : 0.108"  # scripted group (container) (typed FeaturePython)
  n = 0.107596
FEATURE [App::DocumentObjectGroupPython] N_element014  label="N_element : 0.001"  # scripted group (container) (typed FeaturePython)
  n = 0.0008
FEATURE [App::DocumentObjectGroupPython] O_element029  label="O_element : 0.875"  # scripted group (container) (typed FeaturePython)
  n = 0.874976
FEATURE [App::DocumentObjectGroupPython] S_element008  label="S_element : 0.015"  # scripted group (container) (typed FeaturePython)
  n = 0.014627
FEATURE [App::DocumentObjectGroupPython] Ce_element001  label="Ce_element : 0.002"  # scripted group (container) (typed FeaturePython)
  n = 0.002001
FEATURE [App::DocumentObjectGroupPython] G4_CERIC_SULFATE  # scripted group (container) (typed FeaturePython)
  Dunit = g/cm3
  Dvalue = 1.03
  Group = -> [H_element024,N_element014,O_element029,S_element008,Ce_element001]
  conduct = 2
  density = 1
  expand = 3
  formula = G4_CERIC_SULFATE
  name = G4_CERIC_SULFATE
  specific = 4
FEATURE [App::DocumentObjectGroupPython] Cs_element001  label="Cs_element : 1"  # scripted group (container) (typed FeaturePython)
  n = 1
  ref = Cs_element
FEATURE [App::DocumentObjectGroupPython] F_element006  label="F_element : 1"  # scripted group (container) (typed FeaturePython)
  n = 1
  ref = F_element
FEATURE [App::DocumentObjectGroupPython] G4_CESIUM_FLUORIDE  # scripted group (container) (typed FeaturePython)
  Dunit = g/cm3
  Dvalue = 4.115
  Group = -> [Cs_element001,F_element006]
  conduct = 2
  density = 1
  expand = 3
  formula = G4_CESIUM_FLUORIDE
  name = G4_CESIUM_FLUORIDE
  specific = 4
FEATURE [App::DocumentObjectGroupPython] Cs_element002  label="Cs_element : 002"  # scripted group (container) (typed FeaturePython)
  n = 1
  ref = Cs_element
FEATURE [App::DocumentObjectGroupPython] I_element001  label="I_element : 1"  # scripted group (container) (typed FeaturePython)
  n = 1
  ref = I_element
FEATURE [App::DocumentObjectGroupPython] G4_CESIUM_IODIDE  # scripted group (container) (typed FeaturePython)
  Dunit = g/cm3
  Dvalue = 4.51
  Group = -> [Cs_element002,I_element001]
  conduct = 2
  density = 1
  expand = 3
  formula = G4_CESIUM_IODIDE
  name = G4_CESIUM_IODIDE
  specific = 4
FEATURE [App::DocumentObjectGroupPython] C_element028  label="C_element : 013"  # scripted group (container) (typed FeaturePython)
  n = 6
  ref = C_element
FEATURE [App::DocumentObjectGroupPython] H_element025  label="H_element : 013"  # scripted group (container) (typed FeaturePython)
  n = 5
  ref = H_element
FEATURE [App::DocumentObjectGroupPython] Cl_element005  label="Cl_element : 1"  # scripted group (container) (typed FeaturePython)
  n = 1
  ref = Cl_element
FEATURE [App::DocumentObjectGroupPython] G4_CHLOROBENZENE  # scripted group (container) (typed FeaturePython)
  Dunit = g/cm3
  Dvalue = 1.1058
  Group = -> [C_element028,H_element025,Cl_element005]
  conduct = 2
  density = 1
  expand = 3
  formula = G4_CHLOROBENZENE
  name = G4_CHLOROBENZENE
  specific = 4
FEATURE [App::DocumentObjectGroupPython] C_element029  label="C_element : 014"  # scripted group (container) (typed FeaturePython)
  n = 1
  ref = C_element
FEATURE [App::DocumentObjectGroupPython] H_element026  label="H_element : 1"  # scripted group (container) (typed FeaturePython)
  n = 1
  ref = H_element
FEATURE [App::DocumentObjectGroupPython] Cl_element006  label="Cl_element : 3"  # scripted group (container) (typed FeaturePython)
  n = 3
  ref = Cl_element
FEATURE [App::DocumentObjectGroupPython] G4_CHLOROFORM  # scripted group (container) (typed FeaturePython)
  Dunit = g/cm3
  Dvalue = 1.4832
  Group = -> [C_element029,H_element026,Cl_element006]
  conduct = 2
  density = 1
  expand = 3
  formula = G4_CHLOROFORM
  name = G4_CHLOROFORM
  specific = 4
FEATURE [App::DocumentObjectGroupPython] H_element027  label="H_element : 0.010"  # scripted group (container) (typed FeaturePython)
  n = 0.01
FEATURE [App::DocumentObjectGroupPython] C_element030  label="C_element : 0.001"  # scripted group (container) (typed FeaturePython)
  n = 0.001
FEATURE [App::DocumentObjectGroupPython] O_element030  label="O_element : 0.529"  # scripted group (container) (typed FeaturePython)
  n = 0.529107
FEATURE [App::DocumentObjectGroupPython] Na_element005  label="Na_element : 0.016"  # scripted group (container) (typed FeaturePython)
  n = 0.016
FEATURE [App::DocumentObjectGroupPython] Mg_element003  label="Mg_element : 0.004"  # scripted group (container) (typed FeaturePython)
  n = 0.002
FEATURE [App::DocumentObjectGroupPython] Al_element002  label="Al_element : 0.034"  # scripted group (container) (typed FeaturePython)
  n = 0.033872
FEATURE [App::DocumentObjectGroupPython] Si_element002  label="Si_element : 0.337"  # scripted group (container) (typed FeaturePython)
  n = 0.337021
FEATURE [App::DocumentObjectGroupPython] K_element003  label="K_element : 0.013"  # scripted group (container) (typed FeaturePython)
  n = 0.013
FEATURE [App::DocumentObjectGroupPython] Ca_element010  label="Ca_element : 0.044"  # scripted group (container) (typed FeaturePython)
  n = 0.044
FEATURE [App::DocumentObjectGroupPython] Fe_element002  label="Fe_element : 0.014"  # scripted group (container) (typed FeaturePython)
  n = 0.014
FEATURE [App::DocumentObjectGroupPython] G4_CONCRETE  # scripted group (container) (typed FeaturePython)
  Dunit = g/cm3
  Dvalue = 2.3
  Group = -> [H_element027,C_element030,O_element030,Na_element005,Mg_element003,Al_element002,Si_element002,K_element003,Ca_element010,Fe_element002]
  conduct = 2
  density = 1
  expand = 3
  formula = G4_CONCRETE
  name = G4_CONCRETE
  specific = 4
FEATURE [App::DocumentObjectGroupPython] C_element031  label="C_element : 015"  # scripted group (container) (typed FeaturePython)
  n = 6
  ref = C_element
FEATURE [App::DocumentObjectGroupPython] H_element028  label="H_element : 12"  # scripted group (container) (typed FeaturePython)
  n = 12
  ref = H_element
FEATURE [App::DocumentObjectGroupPython] G4_CYCLOHEXANE  # scripted group (container) (typed FeaturePython)
  Dunit = g/cm3
  Dvalue = 0.779
  Group = -> [C_element031,H_element028]
  conduct = 2
  density = 1
  expand = 3
  formula = G4_CYCLOHEXANE
  name = G4_CYCLOHEXANE
  specific = 4
FEATURE [App::DocumentObjectGroupPython] C_element032  label="C_element : 016"  # scripted group (container) (typed FeaturePython)
  n = 6
  ref = C_element
FEATURE [App::DocumentObjectGroupPython] H_element029  label="H_element : 4"  # scripted group (container) (typed FeaturePython)
  n = 4
  ref = H_element
FEATURE [App::DocumentObjectGroupPython] Cl_element007  label="Cl_element : 2"  # scripted group (container) (typed FeaturePython)
  n = 2
  ref = Cl_element
FEATURE [App::DocumentObjectGroupPython] G4_1_2_DICHLOROBENZENE  label="G4_1.2-DICHLOROBENZENE"  # scripted group (container) (typed FeaturePython)
  Dunit = g/cm3
  Dvalue = 1.3048
  Group = -> [C_element032,H_element029,Cl_element007]
  conduct = 2
  density = 1
  expand = 3
  formula = G4_1.2-DICHLOROBENZENE
  name = G4_1.2-DICHLOROBENZENE
  specific = 4
FEATURE [App::DocumentObjectGroupPython] C_element033  label="C_element : 017"  # scripted group (container) (typed FeaturePython)
  n = 4
  ref = C_element
FEATURE [App::DocumentObjectGroupPython] H_element030  label="H_element : 8"  # scripted group (container) (typed FeaturePython)
  n = 8
  ref = H_element
FEATURE [App::DocumentObjectGroupPython] O_element031  label="O_element : 014"  # scripted group (container) (typed FeaturePython)
  n = 1
  ref = O_element
FEATURE [App::DocumentObjectGroupPython] Cl_element008  label="Cl_element : 005"  # scripted group (container) (typed FeaturePython)
  n = 2
  ref = Cl_element
FEATURE [App::DocumentObjectGroupPython] G4_DICHLORODIETHYL_ETHER  # scripted group (container) (typed FeaturePython)
  Dunit = g/cm3
  Dvalue = 1.2199
  Group = -> [C_element033,H_element030,O_element031,Cl_element008]
  conduct = 2
  density = 1
  expand = 3
  formula = G4_DICHLORODIETHYL_ETHER
  name = G4_DICHLORODIETHYL_ETHER
  specific = 4
FEATURE [App::DocumentObjectGroupPython] C_element034  label="C_element : 018"  # scripted group (container) (typed FeaturePython)
  n = 2
  ref = C_element
FEATURE [App::DocumentObjectGroupPython] H_element031  label="H_element : 014"  # scripted group (container) (typed FeaturePython)
  n = 4
  ref = H_element
FEATURE [App::DocumentObjectGroupPython] Cl_element009  label="Cl_element : 006"  # scripted group (container) (typed FeaturePython)
  n = 2
  ref = Cl_element
FEATURE [App::DocumentObjectGroupPython] G4_1_2_DICHLOROETHANE  label="G4_1.2-DICHLOROETHANE"  # scripted group (container) (typed FeaturePython)
  Dunit = g/cm3
  Dvalue = 1.2351
  Group = -> [C_element034,H_element031,Cl_element009]
  conduct = 2
  density = 1
  expand = 3
  formula = G4_1.2-DICHLOROETHANE
  name = G4_1.2-DICHLOROETHANE
  specific = 4
FEATURE [App::DocumentObjectGroupPython] C_element035  label="C_element : 019"  # scripted group (container) (typed FeaturePython)
  n = 4
  ref = C_element
FEATURE [App::DocumentObjectGroupPython] H_element032  label="H_element : 015"  # scripted group (container) (typed FeaturePython)
  n = 10
  ref = H_element
FEATURE [App::DocumentObjectGroupPython] O_element032  label="O_element : 015"  # scripted group (container) (typed FeaturePython)
  n = 1
  ref = O_element
FEATURE [App::DocumentObjectGroupPython] G4_DIETHYL_ETHER  # scripted group (container) (typed FeaturePython)
  Dunit = g/cm3
  Dvalue = 0.71378
  Group = -> [C_element035,H_element032,O_element032]
  conduct = 2
  density = 1
  expand = 3
  formula = G4_DIETHYL_ETHER
  name = G4_DIETHYL_ETHER
  specific = 4
FEATURE [App::DocumentObjectGroupPython] C_element036  label="C_element : 020"  # scripted group (container) (typed FeaturePython)
  n = 3
  ref = C_element
FEATURE [App::DocumentObjectGroupPython] H_element033  label="H_element : 016"  # scripted group (container) (typed FeaturePython)
  n = 7
  ref = H_element
FEATURE [App::DocumentObjectGroupPython] N_element015  label="N_element : 008"  # scripted group (container) (typed FeaturePython)
  n = 1
  ref = N_element
FEATURE [App::DocumentObjectGroupPython] O_element033  label="O_element : 016"  # scripted group (container) (typed FeaturePython)
  n = 1
  ref = O_element
FEATURE [App::DocumentObjectGroupPython] G4_N_N_DIMETHYL_FORMAMIDE  label="G4_N.N-DIMETHYL_FORMAMIDE"  # scripted group (container) (typed FeaturePython)
  Dunit = g/cm3
  Dvalue = 0.9487
  Group = -> [C_element036,H_element033,N_element015,O_element033]
  conduct = 2
  density = 1
  expand = 3
  formula = G4_N.N-DIMETHYL_FORMAMIDE
  name = G4_N.N-DIMETHYL_FORMAMIDE
  specific = 4
FEATURE [App::DocumentObjectGroupPython] C_element037  label="C_element : 021"  # scripted group (container) (typed FeaturePython)
  n = 2
  ref = C_element
FEATURE [App::DocumentObjectGroupPython] H_element034  label="H_element : 017"  # scripted group (container) (typed FeaturePython)
  n = 6
  ref = H_element
FEATURE [App::DocumentObjectGroupPython] O_element034  label="O_element : 017"  # scripted group (container) (typed FeaturePython)
  n = 1
  ref = O_element
FEATURE [App::DocumentObjectGroupPython] S_element009  label="S_element : 003"  # scripted group (container) (typed FeaturePython)
  n = 1
  ref = S_element
FEATURE [App::DocumentObjectGroupPython] G4_DIMETHYL_SULFOXIDE  # scripted group (container) (typed FeaturePython)
  Dunit = g/cm3
  Dvalue = 1.1014
  Group = -> [C_element037,H_element034,O_element034,S_element009]
  conduct = 2
  density = 1
  expand = 3
  formula = G4_DIMETHYL_SULFOXIDE
  name = G4_DIMETHYL_SULFOXIDE
  specific = 4
FEATURE [App::DocumentObjectGroupPython] C_element038  label="C_element : 022"  # scripted group (container) (typed FeaturePython)
  n = 2
  ref = C_element
FEATURE [App::DocumentObjectGroupPython] H_element035  label="H_element : 018"  # scripted group (container) (typed FeaturePython)
  n = 6
  ref = H_element
FEATURE [App::DocumentObjectGroupPython] G4_ETHANE  # scripted group (container) (typed FeaturePython)
  Dunit = g/cm3
  Dvalue = 0.00125324
  Group = -> [C_element038,H_element035]
  conduct = 2
  density = 1
  expand = 3
  formula = G4_ETHANE
  name = G4_ETHANE
  specific = 4
FEATURE [App::DocumentObjectGroupPython] C_element039  label="C_element : 023"  # scripted group (container) (typed FeaturePython)
  n = 2
  ref = C_element
FEATURE [App::DocumentObjectGroupPython] H_element036  label="H_element : 019"  # scripted group (container) (typed FeaturePython)
  n = 6
  ref = H_element
FEATURE [App::DocumentObjectGroupPython] O_element035  label="O_element : 018"  # scripted group (container) (typed FeaturePython)
  n = 1
  ref = O_element
FEATURE [App::DocumentObjectGroupPython] G4_ETHYL_ALCOHOL  # scripted group (container) (typed FeaturePython)
  Dunit = g/cm3
  Dvalue = 0.7893
  Group = -> [C_element039,H_element036,O_element035]
  conduct = 2
  density = 1
  expand = 3
  formula = G4_ETHYL_ALCOHOL
  name = G4_ETHYL_ALCOHOL
  specific = 4
FEATURE [App::DocumentObjectGroupPython] H_element037  label="H_element : 0.090"  # scripted group (container) (typed FeaturePython)
  n = 0.090027
FEATURE [App::DocumentObjectGroupPython] C_element040  label="C_element : 0.585"  # scripted group (container) (typed FeaturePython)
  n = 0.585182
FEATURE [App::DocumentObjectGroupPython] O_element036  label="O_element : 0.325"  # scripted group (container) (typed FeaturePython)
  n = 0.324791
FEATURE [App::DocumentObjectGroupPython] G4_ETHYL_CELLULOSE  # scripted group (container) (typed FeaturePython)
  Dunit = g/cm3
  Dvalue = 1.13
  Group = -> [H_element037,C_element040,O_element036]
  conduct = 2
  density = 1
  expand = 3
  formula = G4_ETHYL_CELLULOSE
  name = G4_ETHYL_CELLULOSE
  specific = 4
FEATURE [App::DocumentObjectGroupPython] C_element041  label="C_element : 024"  # scripted group (container) (typed FeaturePython)
  n = 2
  ref = C_element
FEATURE [App::DocumentObjectGroupPython] H_element038  label="H_element : 020"  # scripted group (container) (typed FeaturePython)
  n = 4
  ref = H_element
FEATURE [App::DocumentObjectGroupPython] G4_ETHYLENE  # scripted group (container) (typed FeaturePython)
  Dunit = g/cm3
  Dvalue = 0.00117497
  Group = -> [C_element041,H_element038]
  conduct = 2
  density = 1
  expand = 3
  formula = G4_ETHYLENE
  name = G4_ETHYLENE
  specific = 4
FEATURE [App::DocumentObjectGroupPython] H_element039  label="H_element : 0.096"  # scripted group (container) (typed FeaturePython)
  n = 0.096
FEATURE [App::DocumentObjectGroupPython] C_element042  label="C_element : 0.195"  # scripted group (container) (typed FeaturePython)
  n = 0.195
FEATURE [App::DocumentObjectGroupPython] N_element016  label="N_element : 0.057"  # scripted group (container) (typed FeaturePython)
  n = 0.057
FEATURE [App::DocumentObjectGroupPython] O_element037  label="O_element : 0.646"  # scripted group (container) (typed FeaturePython)
  n = 0.646
FEATURE [App::DocumentObjectGroupPython] Na_element006  label="Na_element : 0.017"  # scripted group (container) (typed FeaturePython)
  n = 0.001
FEATURE [App::DocumentObjectGroupPython] P_element005  label="P_element : 0.104"  # scripted group (container) (typed FeaturePython)
  n = 0.001
FEATURE [App::DocumentObjectGroupPython] S_element010  label="S_element : 0.016"  # scripted group (container) (typed FeaturePython)
  n = 0.003
FEATURE [App::DocumentObjectGroupPython] Cl_element010  label="Cl_element : 0.005"  # scripted group (container) (typed FeaturePython)
  n = 0.001
FEATURE [App::DocumentObjectGroupPython] G4_EYE_LENS_ICRP  # scripted group (container) (typed FeaturePython)
  Dunit = g/cm3
  Dvalue = 1.07
  Group = -> [H_element039,C_element042,N_element016,O_element037,Na_element006,P_element005,S_element010,Cl_element010]
  conduct = 2
  density = 1
  expand = 3
  formula = G4_EYE_LENS_ICRP
  name = G4_EYE_LENS_ICRP
  specific = 4
FEATURE [App::DocumentObjectGroupPython] Fe_element003  label="Fe_element : 2"  # scripted group (container) (typed FeaturePython)
  n = 2
  ref = Fe_element
FEATURE [App::DocumentObjectGroupPython] O_element038  label="O_element : 019"  # scripted group (container) (typed FeaturePython)
  n = 3
  ref = O_element
FEATURE [App::DocumentObjectGroupPython] G4_FERRIC_OXIDE  # scripted group (container) (typed FeaturePython)
  Dunit = g/cm3
  Dvalue = 5.2
  Group = -> [Fe_element003,O_element038]
  conduct = 2
  density = 1
  expand = 3
  formula = G4_FERRIC_OXIDE
  name = G4_FERRIC_OXIDE
  specific = 4
FEATURE [App::DocumentObjectGroupPython] Fe_element004  label="Fe_element : 1"  # scripted group (container) (typed FeaturePython)
  n = 1
  ref = Fe_element
FEATURE [App::DocumentObjectGroupPython] B_element003  label="B_element : 1"  # scripted group (container) (typed FeaturePython)
  n = 1
  ref = B_element
FEATURE [App::DocumentObjectGroupPython] G4_FERROBORIDE  # scripted group (container) (typed FeaturePython)
  Dunit = g/cm3
  Dvalue = 7.15
  Group = -> [Fe_element004,B_element003]
  conduct = 2
  density = 1
  expand = 3
  formula = G4_FERROBORIDE
  name = G4_FERROBORIDE
  specific = 4
FEATURE [App::DocumentObjectGroupPython] Fe_element005  label="Fe_element : 003"  # scripted group (container) (typed FeaturePython)
  n = 1
  ref = Fe_element
FEATURE [App::DocumentObjectGroupPython] O_element039  label="O_element : 020"  # scripted group (container) (typed FeaturePython)
  n = 1
  ref = O_element
FEATURE [App::DocumentObjectGroupPython] G4_FERROUS_OXIDE  # scripted group (container) (typed FeaturePython)
  Dunit = g/cm3
  Dvalue = 5.7
  Group = -> [Fe_element005,O_element039]
  conduct = 2
  density = 1
  expand = 3
  formula = G4_FERROUS_OXIDE
  name = G4_FERROUS_OXIDE
  specific = 4
FEATURE [App::DocumentObjectGroupPython] H_element040  label="H_element : 0.115"  # scripted group (container) (typed FeaturePython)
  n = 0.108259
FEATURE [App::DocumentObjectGroupPython] N_element017  label="N_element : 0.000"  # scripted group (container) (typed FeaturePython)
  n = 2.7e-05
FEATURE [App::DocumentObjectGroupPython] O_element040  label="O_element : 0.879"  # scripted group (container) (typed FeaturePython)
  n = 0.878636
FEATURE [App::DocumentObjectGroupPython] Na_element007  label="Na_element : 0.000"  # scripted group (container) (typed FeaturePython)
  n = 2.2e-05
FEATURE [App::DocumentObjectGroupPython] S_element011  label="S_element : 0.013"  # scripted group (container) (typed FeaturePython)
  n = 0.012968
FEATURE [App::DocumentObjectGroupPython] Cl_element011  label="Cl_element : 0.000"  # scripted group (container) (typed FeaturePython)
  n = 3.4e-05
FEATURE [App::DocumentObjectGroupPython] Fe_element006  label="Fe_element : 0.000"  # scripted group (container) (typed FeaturePython)
  n = 5.4e-05
FEATURE [App::DocumentObjectGroupPython] G4_FERROUS_SULFATE  # scripted group (container) (typed FeaturePython)
  Dunit = g/cm3
  Dvalue = 1.024
  Group = -> [H_element040,N_element017,O_element040,Na_element007,S_element011,Cl_element011,Fe_element006]
  conduct = 2
  density = 1
  expand = 3
  formula = G4_FERROUS_SULFATE
  name = G4_FERROUS_SULFATE
  specific = 4
FEATURE [App::DocumentObjectGroupPython] C_element043  label="C_element : 0.099"  # scripted group (container) (typed FeaturePython)
  n = 0.099335
FEATURE [App::DocumentObjectGroupPython] F_element007  label="F_element : 0.314"  # scripted group (container) (typed FeaturePython)
  n = 0.314247
FEATURE [App::DocumentObjectGroupPython] Cl_element012  label="Cl_element : 0.586"  # scripted group (container) (typed FeaturePython)
  n = 0.586418
FEATURE [App::DocumentObjectGroupPython] G4_FREON_12  label="G4_FREON-12"  # scripted group (container) (typed FeaturePython)
  Dunit = g/cm3
  Dvalue = 1.12
  Group = -> [C_element043,F_element007,Cl_element012]
  conduct = 2
  density = 1
  expand = 3
  formula = G4_FREON-12
  name = G4_FREON-12
  specific = 4
FEATURE [App::DocumentObjectGroupPython] C_element044  label="C_element : 0.057"  # scripted group (container) (typed FeaturePython)
  n = 0.057245
FEATURE [App::DocumentObjectGroupPython] F_element008  label="F_element : 0.181"  # scripted group (container) (typed FeaturePython)
  n = 0.181096
FEATURE [App::DocumentObjectGroupPython] Br_element001  label="Br_element : 0.762"  # scripted group (container) (typed FeaturePython)
  n = 0.761659
FEATURE [App::DocumentObjectGroupPython] G4_FREON_12B2  label="G4_FREON-12B2"  # scripted group (container) (typed FeaturePython)
  Dunit = g/cm3
  Dvalue = 1.8
  Group = -> [C_element044,F_element008,Br_element001]
  conduct = 2
  density = 1
  expand = 3
  formula = G4_FREON-12B2
  name = G4_FREON-12B2
  specific = 4
FEATURE [App::DocumentObjectGroupPython] C_element045  label="C_element : 0.115"  # scripted group (container) (typed FeaturePython)
  n = 0.114983
FEATURE [App::DocumentObjectGroupPython] F_element009  label="F_element : 0.546"  # scripted group (container) (typed FeaturePython)
  n = 0.545621
FEATURE [App::DocumentObjectGroupPython] Cl_element013  label="Cl_element : 0.339"  # scripted group (container) (typed FeaturePython)
  n = 0.339396
FEATURE [App::DocumentObjectGroupPython] G4_FREON_13  label="G4_FREON-13"  # scripted group (container) (typed FeaturePython)
  Dunit = g/cm3
  Dvalue = 0.95
  Group = -> [C_element045,F_element009,Cl_element013]
  conduct = 2
  density = 1
  expand = 3
  formula = G4_FREON-13
  name = G4_FREON-13
  specific = 4
FEATURE [App::DocumentObjectGroupPython] C_element046  label="C_element : 025"  # scripted group (container) (typed FeaturePython)
  n = 1
  ref = C_element
FEATURE [App::DocumentObjectGroupPython] F_element010  label="F_element : 3"  # scripted group (container) (typed FeaturePython)
  n = 3
  ref = F_element
FEATURE [App::DocumentObjectGroupPython] Br_element002  label="Br_element : 1"  # scripted group (container) (typed FeaturePython)
  n = 1
  ref = Br_element
FEATURE [App::DocumentObjectGroupPython] G4_FREON_13B1  label="G4_FREON-13B1"  # scripted group (container) (typed FeaturePython)
  Dunit = g/cm3
  Dvalue = 1.5
  Group = -> [C_element046,F_element010,Br_element002]
  conduct = 2
  density = 1
  expand = 3
  formula = G4_FREON-13B1
  name = G4_FREON-13B1
  specific = 4
FEATURE [App::DocumentObjectGroupPython] C_element047  label="C_element : 0.061"  # scripted group (container) (typed FeaturePython)
  n = 0.061309
FEATURE [App::DocumentObjectGroupPython] F_element011  label="F_element : 0.291"  # scripted group (container) (typed FeaturePython)
  n = 0.290924
FEATURE [App::DocumentObjectGroupPython] I_element002  label="I_element : 0.648"  # scripted group (container) (typed FeaturePython)
  n = 0.647767
FEATURE [App::DocumentObjectGroupPython] G4_FREON_13I1  label="G4_FREON-13I1"  # scripted group (container) (typed FeaturePython)
  Dunit = g/cm3
  Dvalue = 1.8
  Group = -> [C_element047,F_element011,I_element002]
  conduct = 2
  density = 1
  expand = 3
  formula = G4_FREON-13I1
  name = G4_FREON-13I1
  specific = 4
FEATURE [App::DocumentObjectGroupPython] Gd_element001  label="Gd_element : 2"  # scripted group (container) (typed FeaturePython)
  n = 2
  ref = Gd_element
FEATURE [App::DocumentObjectGroupPython] O_element041  label="O_element : 021"  # scripted group (container) (typed FeaturePython)
  n = 2
  ref = O_element
FEATURE [App::DocumentObjectGroupPython] S_element012  label="S_element : 004"  # scripted group (container) (typed FeaturePython)
  n = 1
  ref = S_element
FEATURE [App::DocumentObjectGroupPython] G4_GADOLINIUM_OXYSULFIDE  # scripted group (container) (typed FeaturePython)
  Dunit = g/cm3
  Dvalue = 7.44
  Group = -> [Gd_element001,O_element041,S_element012]
  conduct = 2
  density = 1
  expand = 3
  formula = G4_GADOLINIUM_OXYSULFIDE
  name = G4_GADOLINIUM_OXYSULFIDE
  specific = 4
FEATURE [App::DocumentObjectGroupPython] Ga_element001  label="Ga_element : 1"  # scripted group (container) (typed FeaturePython)
  n = 1
  ref = Ga_element
FEATURE [App::DocumentObjectGroupPython] As_element001  label="As_element : 1"  # scripted group (container) (typed FeaturePython)
  n = 1
  ref = As_element
FEATURE [App::DocumentObjectGroupPython] G4_GALLIUM_ARSENIDE  # scripted group (container) (typed FeaturePython)
  Dunit = g/cm3
  Dvalue = 5.31
  Group = -> [Ga_element001,As_element001]
  conduct = 2
  density = 1
  expand = 3
  formula = G4_GALLIUM_ARSENIDE
  name = G4_GALLIUM_ARSENIDE
  specific = 4
FEATURE [App::DocumentObjectGroupPython] H_element041  label="H_element : 0.081"  # scripted group (container) (typed FeaturePython)
  n = 0.08118
FEATURE [App::DocumentObjectGroupPython] C_element048  label="C_element : 0.416"  # scripted group (container) (typed FeaturePython)
  n = 0.41606
FEATURE [App::DocumentObjectGroupPython] N_element018  label="N_element : 0.111"  # scripted group (container) (typed FeaturePython)
  n = 0.11124
FEATURE [App::DocumentObjectGroupPython] O_element042  label="O_element : 0.381"  # scripted group (container) (typed FeaturePython)
  n = 0.38064
FEATURE [App::DocumentObjectGroupPython] S_element013  label="S_element : 0.011"  # scripted group (container) (typed FeaturePython)
  n = 0.01088
FEATURE [App::DocumentObjectGroupPython] G4_GEL_PHOTO_EMULSION  # scripted group (container) (typed FeaturePython)
  Dunit = g/cm3
  Dvalue = 1.2914
  Group = -> [H_element041,C_element048,N_element018,O_element042,S_element013]
  conduct = 2
  density = 1
  expand = 3
  formula = G4_GEL_PHOTO_EMULSION
  name = G4_GEL_PHOTO_EMULSION
  specific = 4
FEATURE [App::DocumentObjectGroupPython] B_element004  label="B_element : 0.040"  # scripted group (container) (typed FeaturePython)
  n = 0.0400639
FEATURE [App::DocumentObjectGroupPython] O_element043  label="O_element : 0.540"  # scripted group (container) (typed FeaturePython)
  n = 0.539561
FEATURE [App::DocumentObjectGroupPython] Na_element008  label="Na_element : 0.028"  # scripted group (container) (typed FeaturePython)
  n = 0.0281909
FEATURE [App::DocumentObjectGroupPython] Al_element003  label="Al_element : 0.012"  # scripted group (container) (typed FeaturePython)
  n = 0.011644
FEATURE [App::DocumentObjectGroupPython] Si_element003  label="Si_element : 0.377"  # scripted group (container) (typed FeaturePython)
  n = 0.377219
FEATURE [App::DocumentObjectGroupPython] K_element004  label="K_element : 0.014"  # scripted group (container) (typed FeaturePython)
  n = 0.00332099
FEATURE [App::DocumentObjectGroupPython] G4_Pyrex_Glass  # scripted group (container) (typed FeaturePython)
  Dunit = g/cm3
  Dvalue = 2.23
  Group = -> [B_element004,O_element043,Na_element008,Al_element003,Si_element003,K_element004]
  conduct = 2
  density = 1
  expand = 3
  formula = G4_Pyrex_Glass
  name = G4_Pyrex_Glass
  specific = 4
FEATURE [App::DocumentObjectGroupPython] O_element044  label="O_element : 0.156"  # scripted group (container) (typed FeaturePython)
  n = 0.156453
FEATURE [App::DocumentObjectGroupPython] Si_element004  label="Si_element : 0.081"  # scripted group (container) (typed FeaturePython)
  n = 0.080866
FEATURE [App::DocumentObjectGroupPython] Ti_element001  label="Ti_element : 0.008"  # scripted group (container) (typed FeaturePython)
  n = 0.008092
FEATURE [App::DocumentObjectGroupPython] As_element002  label="As_element : 0.003"  # scripted group (container) (typed FeaturePython)
  n = 0.002651
FEATURE [App::DocumentObjectGroupPython] Pb_element001  label="Pb_element : 0.752"  # scripted group (container) (typed FeaturePython)
  n = 0.751938
FEATURE [App::DocumentObjectGroupPython] G4_GLASS_LEAD  # scripted group (container) (typed FeaturePython)
  Dunit = g/cm3
  Dvalue = 6.22
  Group = -> [O_element044,Si_element004,Ti_element001,As_element002,Pb_element001]
  conduct = 2
  density = 1
  expand = 3
  formula = G4_GLASS_LEAD
  name = G4_GLASS_LEAD
  specific = 4
FEATURE [App::DocumentObjectGroupPython] O_element045  label="O_element : 0.460"  # scripted group (container) (typed FeaturePython)
  n = 0.4598
FEATURE [App::DocumentObjectGroupPython] Na_element009  label="Na_element : 0.096"  # scripted group (container) (typed FeaturePython)
  n = 0.0964411
FEATURE [App::DocumentObjectGroupPython] Si_element005  label="Si_element : 0.378"  # scripted group (container) (typed FeaturePython)
  n = 0.336553
FEATURE [App::DocumentObjectGroupPython] Ca_element011  label="Ca_element : 0.107"  # scripted group (container) (typed FeaturePython)
  n = 0.107205
FEATURE [App::DocumentObjectGroupPython] G4_GLASS_PLATE  # scripted group (container) (typed FeaturePython)
  Dunit = g/cm3
  Dvalue = 2.4
  Group = -> [O_element045,Na_element009,Si_element005,Ca_element011]
  conduct = 2
  density = 1
  expand = 3
  formula = G4_GLASS_PLATE
  name = G4_GLASS_PLATE
  specific = 4
FEATURE [App::DocumentObjectGroupPython] C_element049  label="C_element : 026"  # scripted group (container) (typed FeaturePython)
  n = 5
  ref = C_element
FEATURE [App::DocumentObjectGroupPython] H_element042  label="H_element : 021"  # scripted group (container) (typed FeaturePython)
  n = 10
  ref = H_element
FEATURE [App::DocumentObjectGroupPython] N_element019  label="N_element : 2"  # scripted group (container) (typed FeaturePython)
  n = 2
  ref = N_element
FEATURE [App::DocumentObjectGroupPython] O_element046  label="O_element : 022"  # scripted group (container) (typed FeaturePython)
  n = 3
  ref = O_element
FEATURE [App::DocumentObjectGroupPython] G4_GLUTAMINE  # scripted group (container) (typed FeaturePython)
  Dunit = g/cm3
  Dvalue = 1.46
  Group = -> [C_element049,H_element042,N_element019,O_element046]
  conduct = 2
  density = 1
  expand = 3
  formula = G4_GLUTAMINE
  name = G4_GLUTAMINE
  specific = 4
FEATURE [App::DocumentObjectGroupPython] C_element050  label="C_element : 027"  # scripted group (container) (typed FeaturePython)
  n = 3
  ref = C_element
FEATURE [App::DocumentObjectGroupPython] H_element043  label="H_element : 022"  # scripted group (container) (typed FeaturePython)
  n = 8
  ref = H_element
FEATURE [App::DocumentObjectGroupPython] O_element047  label="O_element : 023"  # scripted group (container) (typed FeaturePython)
  n = 3
  ref = O_element
FEATURE [App::DocumentObjectGroupPython] G4_GLYCEROL  # scripted group (container) (typed FeaturePython)
  Dunit = g/cm3
  Dvalue = 1.2613
  Group = -> [C_element050,H_element043,O_element047]
  conduct = 2
  density = 1
  expand = 3
  formula = G4_GLYCEROL
  name = G4_GLYCEROL
  specific = 4
FEATURE [App::DocumentObjectGroupPython] C_element051  label="C_element : 028"  # scripted group (container) (typed FeaturePython)
  n = 5
  ref = C_element
FEATURE [App::DocumentObjectGroupPython] H_element044  label="H_element : 023"  # scripted group (container) (typed FeaturePython)
  n = 5
  ref = H_element
FEATURE [App::DocumentObjectGroupPython] N_element020  label="N_element : 009"  # scripted group (container) (typed FeaturePython)
  n = 5
  ref = N_element
FEATURE [App::DocumentObjectGroupPython] O_element048  label="O_element : 024"  # scripted group (container) (typed FeaturePython)
  n = 1
  ref = O_element
FEATURE [App::DocumentObjectGroupPython] G4_GUANINE  # scripted group (container) (typed FeaturePython)
  Dunit = g/cm3
  Dvalue = 2.2
  Group = -> [C_element051,H_element044,N_element020,O_element048]
  conduct = 2
  density = 1
  expand = 3
  formula = G4_GUANINE
  name = G4_GUANINE
  specific = 4
FEATURE [App::DocumentObjectGroupPython] Ca_element012  label="Ca_element : 006"  # scripted group (container) (typed FeaturePython)
  n = 1
  ref = Ca_element
FEATURE [App::DocumentObjectGroupPython] S_element014  label="S_element : 005"  # scripted group (container) (typed FeaturePython)
  n = 1
  ref = S_element
FEATURE [App::DocumentObjectGroupPython] O_element049  label="O_element : 6"  # scripted group (container) (typed FeaturePython)
  n = 6
  ref = O_element
FEATURE [App::DocumentObjectGroupPython] H_element045  label="H_element : 024"  # scripted group (container) (typed FeaturePython)
  n = 4
  ref = H_element
FEATURE [App::DocumentObjectGroupPython] G4_GYPSUM  # scripted group (container) (typed FeaturePython)
  Dunit = g/cm3
  Dvalue = 2.32
  Group = -> [Ca_element012,S_element014,O_element049,H_element045]
  conduct = 2
  density = 1
  expand = 3
  formula = G4_GYPSUM
  name = G4_GYPSUM
  specific = 4
FEATURE [App::DocumentObjectGroupPython] C_element052  label="C_element : 7"  # scripted group (container) (typed FeaturePython)
  n = 7
  ref = C_element
FEATURE [App::DocumentObjectGroupPython] H_element046  label="H_element : 16"  # scripted group (container) (typed FeaturePython)
  n = 16
  ref = H_element
FEATURE [App::DocumentObjectGroupPython] G4_N_HEPTANE  label="G4_N-HEPTANE"  # scripted group (container) (typed FeaturePython)
  Dunit = g/cm3
  Dvalue = 0.68376
  Group = -> [C_element052,H_element046]
  conduct = 2
  density = 1
  expand = 3
  formula = G4_N-HEPTANE
  name = G4_N-HEPTANE
  specific = 4
FEATURE [App::DocumentObjectGroupPython] C_element053  label="C_element : 029"  # scripted group (container) (typed FeaturePython)
  n = 6
  ref = C_element
FEATURE [App::DocumentObjectGroupPython] H_element047  label="H_element : 14"  # scripted group (container) (typed FeaturePython)
  n = 14
  ref = H_element
FEATURE [App::DocumentObjectGroupPython] G4_N_HEXANE  label="G4_N-HEXANE"  # scripted group (container) (typed FeaturePython)
  Dunit = g/cm3
  Dvalue = 0.6603
  Group = -> [C_element053,H_element047]
  conduct = 2
  density = 1
  expand = 3
  formula = G4_N-HEXANE
  name = G4_N-HEXANE
  specific = 4
FEATURE [App::DocumentObjectGroupPython] C_element054  label="C_element : 22"  # scripted group (container) (typed FeaturePython)
  n = 22
  ref = C_element
FEATURE [App::DocumentObjectGroupPython] H_element048  label="H_element : 025"  # scripted group (container) (typed FeaturePython)
  n = 10
  ref = H_element
FEATURE [App::DocumentObjectGroupPython] N_element021  label="N_element : 010"  # scripted group (container) (typed FeaturePython)
  n = 2
  ref = N_element
FEATURE [App::DocumentObjectGroupPython] O_element050  label="O_element : 025"  # scripted group (container) (typed FeaturePython)
  n = 5
  ref = O_element
FEATURE [App::DocumentObjectGroupPython] G4_KAPTON  # scripted group (container) (typed FeaturePython)
  Dunit = g/cm3
  Dvalue = 1.42
  Group = -> [C_element054,H_element048,N_element021,O_element050]
  conduct = 2
  density = 1
  expand = 3
  formula = G4_KAPTON
  name = G4_KAPTON
  specific = 4
FEATURE [App::DocumentObjectGroupPython] La_element001  label="La_element : 1"  # scripted group (container) (typed FeaturePython)
  n = 1
  ref = La_element
FEATURE [App::DocumentObjectGroupPython] Br_element003  label="Br_element : 002"  # scripted group (container) (typed FeaturePython)
  n = 1
  ref = Br_element
FEATURE [App::DocumentObjectGroupPython] O_element051  label="O_element : 026"  # scripted group (container) (typed FeaturePython)
  n = 1
  ref = O_element
FEATURE [App::DocumentObjectGroupPython] G4_LANTHANUM_OXYBROMIDE  # scripted group (container) (typed FeaturePython)
  Dunit = g/cm3
  Dvalue = 6.28
  Group = -> [La_element001,Br_element003,O_element051]
  conduct = 2
  density = 1
  expand = 3
  formula = G4_LANTHANUM_OXYBROMIDE
  name = G4_LANTHANUM_OXYBROMIDE
  specific = 4
FEATURE [App::DocumentObjectGroupPython] La_element002  label="La_element : 2"  # scripted group (container) (typed FeaturePython)
  n = 2
  ref = La_element
FEATURE [App::DocumentObjectGroupPython] O_element052  label="O_element : 027"  # scripted group (container) (typed FeaturePython)
  n = 2
  ref = O_element
FEATURE [App::DocumentObjectGroupPython] S_element015  label="S_element : 006"  # scripted group (container) (typed FeaturePython)
  n = 1
  ref = S_element
FEATURE [App::DocumentObjectGroupPython] G4_LANTHANUM_OXYSULFIDE  # scripted group (container) (typed FeaturePython)
  Dunit = g/cm3
  Dvalue = 5.86
  Group = -> [La_element002,O_element052,S_element015]
  conduct = 2
  density = 1
  expand = 3
  formula = G4_LANTHANUM_OXYSULFIDE
  name = G4_LANTHANUM_OXYSULFIDE
  specific = 4
FEATURE [App::DocumentObjectGroupPython] O_element053  label="O_element : 0.072"  # scripted group (container) (typed FeaturePython)
  n = 0.071682
FEATURE [App::DocumentObjectGroupPython] Pb_element002  label="Pb_element : 0.928"  # scripted group (container) (typed FeaturePython)
  n = 0.928318
FEATURE [App::DocumentObjectGroupPython] G4_LEAD_OXIDE  # scripted group (container) (typed FeaturePython)
  Dunit = g/cm3
  Dvalue = 9.53
  Group = -> [O_element053,Pb_element002]
  conduct = 2
  density = 1
  expand = 3
  formula = G4_LEAD_OXIDE
  name = G4_LEAD_OXIDE
  specific = 4
FEATURE [App::DocumentObjectGroupPython] Li_element001  label="Li_element : 1"  # scripted group (container) (typed FeaturePython)
  n = 1
  ref = Li_element
FEATURE [App::DocumentObjectGroupPython] N_element022  label="N_element : 011"  # scripted group (container) (typed FeaturePython)
  n = 1
  ref = N_element
FEATURE [App::DocumentObjectGroupPython] H_element049  label="H_element : 026"  # scripted group (container) (typed FeaturePython)
  n = 2
  ref = H_element
FEATURE [App::DocumentObjectGroupPython] G4_LITHIUM_AMIDE  # scripted group (container) (typed FeaturePython)
  Dunit = g/cm3
  Dvalue = 1.178
  Group = -> [Li_element001,N_element022,H_element049]
  conduct = 2
  density = 1
  expand = 3
  formula = G4_LITHIUM_AMIDE
  name = G4_LITHIUM_AMIDE
  specific = 4
FEATURE [App::DocumentObjectGroupPython] Li_element002  label="Li_element : 2"  # scripted group (container) (typed FeaturePython)
  n = 2
  ref = Li_element
FEATURE [App::DocumentObjectGroupPython] C_element055  label="C_element : 030"  # scripted group (container) (typed FeaturePython)
  n = 1
  ref = C_element
FEATURE [App::DocumentObjectGroupPython] O_element054  label="O_element : 028"  # scripted group (container) (typed FeaturePython)
  n = 3
  ref = O_element
FEATURE [App::DocumentObjectGroupPython] G4_LITHIUM_CARBONATE  # scripted group (container) (typed FeaturePython)
  Dunit = g/cm3
  Dvalue = 2.11
  Group = -> [Li_element002,C_element055,O_element054]
  conduct = 2
  density = 1
  expand = 3
  formula = G4_LITHIUM_CARBONATE
  name = G4_LITHIUM_CARBONATE
  specific = 4
FEATURE [App::DocumentObjectGroupPython] Li_element003  label="Li_element : 003"  # scripted group (container) (typed FeaturePython)
  n = 1
  ref = Li_element
FEATURE [App::DocumentObjectGroupPython] F_element012  label="F_element : 004"  # scripted group (container) (typed FeaturePython)
  n = 1
  ref = F_element
FEATURE [App::DocumentObjectGroupPython] G4_LITHIUM_FLUORIDE  # scripted group (container) (typed FeaturePython)
  Dunit = g/cm3
  Dvalue = 2.635
  Group = -> [Li_element003,F_element012]
  conduct = 2
  density = 1
  expand = 3
  formula = G4_LITHIUM_FLUORIDE
  name = G4_LITHIUM_FLUORIDE
  specific = 4
FEATURE [App::DocumentObjectGroupPython] Li_element004  label="Li_element : 004"  # scripted group (container) (typed FeaturePython)
  n = 1
  ref = Li_element
FEATURE [App::DocumentObjectGroupPython] H_element050  label="H_element : 027"  # scripted group (container) (typed FeaturePython)
  n = 1
  ref = H_element
FEATURE [App::DocumentObjectGroupPython] G4_LITHIUM_HYDRIDE  # scripted group (container) (typed FeaturePython)
  Dunit = g/cm3
  Dvalue = 0.82
  Group = -> [Li_element004,H_element050]
  conduct = 2
  density = 1
  expand = 3
  formula = G4_LITHIUM_HYDRIDE
  name = G4_LITHIUM_HYDRIDE
  specific = 4
FEATURE [App::DocumentObjectGroupPython] Li_element005  label="Li_element : 005"  # scripted group (container) (typed FeaturePython)
  n = 1
  ref = Li_element
FEATURE [App::DocumentObjectGroupPython] I_element003  label="I_element : 002"  # scripted group (container) (typed FeaturePython)
  n = 1
  ref = I_element
FEATURE [App::DocumentObjectGroupPython] G4_LITHIUM_IODIDE  # scripted group (container) (typed FeaturePython)
  Dunit = g/cm3
  Dvalue = 3.494
  Group = -> [Li_element005,I_element003]
  conduct = 2
  density = 1
  expand = 3
  formula = G4_LITHIUM_IODIDE
  name = G4_LITHIUM_IODIDE
  specific = 4
FEATURE [App::DocumentObjectGroupPython] Li_element006  label="Li_element : 006"  # scripted group (container) (typed FeaturePython)
  n = 2
  ref = Li_element
FEATURE [App::DocumentObjectGroupPython] O_element055  label="O_element : 029"  # scripted group (container) (typed FeaturePython)
  n = 1
  ref = O_element
FEATURE [App::DocumentObjectGroupPython] G4_LITHIUM_OXIDE  # scripted group (container) (typed FeaturePython)
  Dunit = g/cm3
  Dvalue = 2.013
  Group = -> [Li_element006,O_element055]
  conduct = 2
  density = 1
  expand = 3
  formula = G4_LITHIUM_OXIDE
  name = G4_LITHIUM_OXIDE
  specific = 4
FEATURE [App::DocumentObjectGroupPython] Li_element007  label="Li_element : 007"  # scripted group (container) (typed FeaturePython)
  n = 2
  ref = Li_element
FEATURE [App::DocumentObjectGroupPython] B_element005  label="B_element : 005"  # scripted group (container) (typed FeaturePython)
  n = 4
  ref = B_element
FEATURE [App::DocumentObjectGroupPython] O_element056  label="O_element : 7"  # scripted group (container) (typed FeaturePython)
  n = 7
  ref = O_element
FEATURE [App::DocumentObjectGroupPython] G4_LITHIUM_TETRABORATE  # scripted group (container) (typed FeaturePython)
  Dunit = g/cm3
  Dvalue = 2.44
  Group = -> [Li_element007,B_element005,O_element056]
  conduct = 2
  density = 1
  expand = 3
  formula = G4_LITHIUM_TETRABORATE
  name = G4_LITHIUM_TETRABORATE
  specific = 4
FEATURE [App::DocumentObjectGroupPython] H_element051  label="H_element : 0.105"  # scripted group (container) (typed FeaturePython)
  n = 0.105
FEATURE [App::DocumentObjectGroupPython] C_element056  label="C_element : 0.083"  # scripted group (container) (typed FeaturePython)
  n = 0.083
FEATURE [App::DocumentObjectGroupPython] N_element023  label="N_element : 0.023"  # scripted group (container) (typed FeaturePython)
  n = 0.023
FEATURE [App::DocumentObjectGroupPython] O_element057  label="O_element : 0.779"  # scripted group (container) (typed FeaturePython)
  n = 0.779
FEATURE [App::DocumentObjectGroupPython] Na_element010  label="Na_element : 0.097"  # scripted group (container) (typed FeaturePython)
  n = 0.002
FEATURE [App::DocumentObjectGroupPython] P_element006  label="P_element : 0.105"  # scripted group (container) (typed FeaturePython)
  n = 0.001
FEATURE [App::DocumentObjectGroupPython] S_element016  label="S_element : 0.017"  # scripted group (container) (typed FeaturePython)
  n = 0.002
FEATURE [App::DocumentObjectGroupPython] Cl_element014  label="Cl_element : 0.587"  # scripted group (container) (typed FeaturePython)
  n = 0.003
FEATURE [App::DocumentObjectGroupPython] K_element005  label="K_element : 0.015"  # scripted group (container) (typed FeaturePython)
  n = 0.002
FEATURE [App::DocumentObjectGroupPython] G4_LUNG_ICRP  # scripted group (container) (typed FeaturePython)
  Dunit = g/cm3
  Dvalue = 1.04
  Group = -> [H_element051,C_element056,N_element023,O_element057,Na_element010,P_element006,S_element016,Cl_element014,K_element005]
  conduct = 2
  density = 1
  expand = 3
  formula = G4_LUNG_ICRP
  name = G4_LUNG_ICRP
  specific = 4
FEATURE [App::DocumentObjectGroupPython] H_element052  label="H_element : 0.116"  # scripted group (container) (typed FeaturePython)
  n = 0.114318
FEATURE [App::DocumentObjectGroupPython] C_element057  label="C_element : 0.656"  # scripted group (container) (typed FeaturePython)
  n = 0.655824
FEATURE [App::DocumentObjectGroupPython] O_element058  label="O_element : 0.092"  # scripted group (container) (typed FeaturePython)
  n = 0.0921831
FEATURE [App::DocumentObjectGroupPython] Mg_element004  label="Mg_element : 0.135"  # scripted group (container) (typed FeaturePython)
  n = 0.134792
FEATURE [App::DocumentObjectGroupPython] Ca_element013  label="Ca_element : 0.003"  # scripted group (container) (typed FeaturePython)
  n = 0.002883
FEATURE [App::DocumentObjectGroupPython] G4_M3_WAX  # scripted group (container) (typed FeaturePython)
  Dunit = g/cm3
  Dvalue = 1.05
  Group = -> [H_element052,C_element057,O_element058,Mg_element004,Ca_element013]
  conduct = 2
  density = 1
  expand = 3
  formula = G4_M3_WAX
  name = G4_M3_WAX
  specific = 4
FEATURE [App::DocumentObjectGroupPython] Mg_element005  label="Mg_element : 1"  # scripted group (container) (typed FeaturePython)
  n = 1
  ref = Mg_element
FEATURE [App::DocumentObjectGroupPython] C_element058  label="C_element : 031"  # scripted group (container) (typed FeaturePython)
  n = 1
  ref = C_element
FEATURE [App::DocumentObjectGroupPython] O_element059  label="O_element : 030"  # scripted group (container) (typed FeaturePython)
  n = 3
  ref = O_element
FEATURE [App::DocumentObjectGroupPython] G4_MAGNESIUM_CARBONATE  # scripted group (container) (typed FeaturePython)
  Dunit = g/cm3
  Dvalue = 2.958
  Group = -> [Mg_element005,C_element058,O_element059]
  conduct = 2
  density = 1
  expand = 3
  formula = G4_MAGNESIUM_CARBONATE
  name = G4_MAGNESIUM_CARBONATE
  specific = 4
FEATURE [App::DocumentObjectGroupPython] Mg_element006  label="Mg_element : 002"  # scripted group (container) (typed FeaturePython)
  n = 1
  ref = Mg_element
FEATURE [App::DocumentObjectGroupPython] F_element013  label="F_element : 005"  # scripted group (container) (typed FeaturePython)
  n = 2
  ref = F_element
FEATURE [App::DocumentObjectGroupPython] G4_MAGNESIUM_FLUORIDE  # scripted group (container) (typed FeaturePython)
  Dunit = g/cm3
  Dvalue = 3
  Group = -> [Mg_element006,F_element013]
  conduct = 2
  density = 1
  expand = 3
  formula = G4_MAGNESIUM_FLUORIDE
  name = G4_MAGNESIUM_FLUORIDE
  specific = 4
FEATURE [App::DocumentObjectGroupPython] Mg_element007  label="Mg_element : 003"  # scripted group (container) (typed FeaturePython)
  n = 1
  ref = Mg_element
FEATURE [App::DocumentObjectGroupPython] O_element060  label="O_element : 031"  # scripted group (container) (typed FeaturePython)
  n = 1
  ref = O_element
FEATURE [App::DocumentObjectGroupPython] G4_MAGNESIUM_OXIDE  # scripted group (container) (typed FeaturePython)
  Dunit = g/cm3
  Dvalue = 3.58
  Group = -> [Mg_element007,O_element060]
  conduct = 2
  density = 1
  expand = 3
  formula = G4_MAGNESIUM_OXIDE
  name = G4_MAGNESIUM_OXIDE
  specific = 4
FEATURE [App::DocumentObjectGroupPython] Mg_element008  label="Mg_element : 004"  # scripted group (container) (typed FeaturePython)
  n = 1
  ref = Mg_element
FEATURE [App::DocumentObjectGroupPython] B_element006  label="B_element : 006"  # scripted group (container) (typed FeaturePython)
  n = 4
  ref = B_element
FEATURE [App::DocumentObjectGroupPython] O_element061  label="O_element : 032"  # scripted group (container) (typed FeaturePython)
  n = 7
  ref = O_element
FEATURE [App::DocumentObjectGroupPython] G4_MAGNESIUM_TETRABORATE  # scripted group (container) (typed FeaturePython)
  Dunit = g/cm3
  Dvalue = 2.53
  Group = -> [Mg_element008,B_element006,O_element061]
  conduct = 2
  density = 1
  expand = 3
  formula = G4_MAGNESIUM_TETRABORATE
  name = G4_MAGNESIUM_TETRABORATE
  specific = 4
FEATURE [App::DocumentObjectGroupPython] Hg_element001  label="Hg_element : 1"  # scripted group (container) (typed FeaturePython)
  n = 1
  ref = Hg_element
FEATURE [App::DocumentObjectGroupPython] I_element004  label="I_element : 2"  # scripted group (container) (typed FeaturePython)
  n = 2
  ref = I_element
FEATURE [App::DocumentObjectGroupPython] G4_MERCURIC_IODIDE  # scripted group (container) (typed FeaturePython)
  Dunit = g/cm3
  Dvalue = 6.36
  Group = -> [Hg_element001,I_element004]
  conduct = 2
  density = 1
  expand = 3
  formula = G4_MERCURIC_IODIDE
  name = G4_MERCURIC_IODIDE
  specific = 4
FEATURE [App::DocumentObjectGroupPython] C_element059  label="C_element : 032"  # scripted group (container) (typed FeaturePython)
  n = 1
  ref = C_element
FEATURE [App::DocumentObjectGroupPython] H_element053  label="H_element : 028"  # scripted group (container) (typed FeaturePython)
  n = 4
  ref = H_element
FEATURE [App::DocumentObjectGroupPython] G4_METHANE  # scripted group (container) (typed FeaturePython)
  Dunit = g/cm3
  Dvalue = 0.000667151
  Group = -> [C_element059,H_element053]
  conduct = 2
  density = 1
  expand = 3
  formula = G4_METHANE
  name = G4_METHANE
  specific = 4
FEATURE [App::DocumentObjectGroupPython] C_element060  label="C_element : 033"  # scripted group (container) (typed FeaturePython)
  n = 1
  ref = C_element
FEATURE [App::DocumentObjectGroupPython] H_element054  label="H_element : 029"  # scripted group (container) (typed FeaturePython)
  n = 4
  ref = H_element
FEATURE [App::DocumentObjectGroupPython] O_element062  label="O_element : 033"  # scripted group (container) (typed FeaturePython)
  n = 1
  ref = O_element
FEATURE [App::DocumentObjectGroupPython] G4_METHANOL  # scripted group (container) (typed FeaturePython)
  Dunit = g/cm3
  Dvalue = 0.7914
  Group = -> [C_element060,H_element054,O_element062]
  conduct = 2
  density = 1
  expand = 3
  formula = G4_METHANOL
  name = G4_METHANOL
  specific = 4
FEATURE [App::DocumentObjectGroupPython] H_element055  label="H_element : 0.134"  # scripted group (container) (typed FeaturePython)
  n = 0.13404
FEATURE [App::DocumentObjectGroupPython] C_element061  label="C_element : 0.778"  # scripted group (container) (typed FeaturePython)
  n = 0.77796
FEATURE [App::DocumentObjectGroupPython] O_element063  label="O_element : 0.035"  # scripted group (container) (typed FeaturePython)
  n = 0.03502
FEATURE [App::DocumentObjectGroupPython] Mg_element009  label="Mg_element : 0.039"  # scripted group (container) (typed FeaturePython)
  n = 0.038594
FEATURE [App::DocumentObjectGroupPython] Ti_element002  label="Ti_element : 0.014"  # scripted group (container) (typed FeaturePython)
  n = 0.014386
FEATURE [App::DocumentObjectGroupPython] G4_MIX_D_WAX  # scripted group (container) (typed FeaturePython)
  Dunit = g/cm3
  Dvalue = 0.99
  Group = -> [H_element055,C_element061,O_element063,Mg_element009,Ti_element002]
  conduct = 2
  density = 1
  expand = 3
  formula = G4_MIX_D_WAX
  name = G4_MIX_D_WAX
  specific = 4
FEATURE [App::DocumentObjectGroupPython] H_element056  label="H_element : 0.135"  # scripted group (container) (typed FeaturePython)
  n = 0.081192
FEATURE [App::DocumentObjectGroupPython] C_element062  label="C_element : 0.583"  # scripted group (container) (typed FeaturePython)
  n = 0.583442
FEATURE [App::DocumentObjectGroupPython] N_element024  label="N_element : 0.018"  # scripted group (container) (typed FeaturePython)
  n = 0.017798
FEATURE [App::DocumentObjectGroupPython] O_element064  label="O_element : 0.186"  # scripted group (container) (typed FeaturePython)
  n = 0.186381
FEATURE [App::DocumentObjectGroupPython] Mg_element010  label="Mg_element : 0.130"  # scripted group (container) (typed FeaturePython)
  n = 0.130287
FEATURE [App::DocumentObjectGroupPython] Cl_element015  label="Cl_element : 0.588"  # scripted group (container) (typed FeaturePython)
  n = 0.0009
FEATURE [App::DocumentObjectGroupPython] G4_MS20_TISSUE  # scripted group (container) (typed FeaturePython)
  Dunit = g/cm3
  Dvalue = 1
  Group = -> [H_element056,C_element062,N_element024,O_element064,Mg_element010,Cl_element015]
  conduct = 2
  density = 1
  expand = 3
  formula = G4_MS20_TISSUE
  name = G4_MS20_TISSUE
  specific = 4
FEATURE [App::DocumentObjectGroupPython] H_element057  label="H_element : 0.136"  # scripted group (container) (typed FeaturePython)
  n = 0.102
FEATURE [App::DocumentObjectGroupPython] C_element063  label="C_element : 0.143"  # scripted group (container) (typed FeaturePython)
  n = 0.143
FEATURE [App::DocumentObjectGroupPython] N_element025  label="N_element : 0.034"  # scripted group (container) (typed FeaturePython)
  n = 0.034
FEATURE [App::DocumentObjectGroupPython] O_element065  label="O_element : 0.710"  # scripted group (container) (typed FeaturePython)
  n = 0.71
FEATURE [App::DocumentObjectGroupPython] Na_element011  label="Na_element : 0.098"  # scripted group (container) (typed FeaturePython)
  n = 0.001
FEATURE [App::DocumentObjectGroupPython] P_element007  label="P_element : 0.002"  # scripted group (container) (typed FeaturePython)
  n = 0.002
FEATURE [App::DocumentObjectGroupPython] S_element017  label="S_element : 0.018"  # scripted group (container) (typed FeaturePython)
  n = 0.003
FEATURE [App::DocumentObjectGroupPython] Cl_element016  label="Cl_element : 0.589"  # scripted group (container) (typed FeaturePython)
  n = 0.001
FEATURE [App::DocumentObjectGroupPython] K_element006  label="K_element : 0.004"  # scripted group (container) (typed FeaturePython)
  n = 0.004
FEATURE [App::DocumentObjectGroupPython] G4_MUSCLE_SKELETAL_ICRP  # scripted group (container) (typed FeaturePython)
  Dunit = g/cm3
  Dvalue = 1.05
  Group = -> [H_element057,C_element063,N_element025,O_element065,Na_element011,P_element007,S_element017,Cl_element016,K_element006]
  conduct = 2
  density = 1
  expand = 3
  formula = G4_MUSCLE_SKELETAL_ICRP
  name = G4_MUSCLE_SKELETAL_ICRP
  specific = 4
FEATURE [App::DocumentObjectGroupPython] H_element058  label="H_element : 0.137"  # scripted group (container) (typed FeaturePython)
  n = 0.102102
FEATURE [App::DocumentObjectGroupPython] C_element064  label="C_element : 0.123"  # scripted group (container) (typed FeaturePython)
  n = 0.123123
FEATURE [App::DocumentObjectGroupPython] N_element026  label="N_element : 0.756"  # scripted group (container) (typed FeaturePython)
  n = 0.035035
FEATURE [App::DocumentObjectGroupPython] O_element066  label="O_element : 0.730"  # scripted group (container) (typed FeaturePython)
  n = 0.72973
FEATURE [App::DocumentObjectGroupPython] Na_element012  label="Na_element : 0.099"  # scripted group (container) (typed FeaturePython)
  n = 0.001001
FEATURE [App::DocumentObjectGroupPython] P_element008  label="P_element : 0.106"  # scripted group (container) (typed FeaturePython)
  n = 0.002002
FEATURE [App::DocumentObjectGroupPython] S_element018  label="S_element : 0.019"  # scripted group (container) (typed FeaturePython)
  n = 0.004004
FEATURE [App::DocumentObjectGroupPython] K_element007  label="K_element : 0.016"  # scripted group (container) (typed FeaturePython)
  n = 0.003003
FEATURE [App::DocumentObjectGroupPython] G4_MUSCLE_STRIATED_ICRU  # scripted group (container) (typed FeaturePython)
  Dunit = g/cm3
  Dvalue = 1.04
  Group = -> [H_element058,C_element064,N_element026,O_element066,Na_element012,P_element008,S_element018,K_element007]
  conduct = 2
  density = 1
  expand = 3
  formula = G4_MUSCLE_STRIATED_ICRU
  name = G4_MUSCLE_STRIATED_ICRU
  specific = 4
FEATURE [App::DocumentObjectGroupPython] H_element059  label="H_element : 0.098"  # scripted group (container) (typed FeaturePython)
  n = 0.0982341
FEATURE [App::DocumentObjectGroupPython] C_element065  label="C_element : 0.156"  # scripted group (container) (typed FeaturePython)
  n = 0.156214
FEATURE [App::DocumentObjectGroupPython] N_element027  label="N_element : 0.757"  # scripted group (container) (typed FeaturePython)
  n = 0.035451
FEATURE [App::DocumentObjectGroupPython] O_element067  label="O_element : 0.880"  # scripted group (container) (typed FeaturePython)
  n = 0.710101
FEATURE [App::DocumentObjectGroupPython] G4_MUSCLE_WITH_SUCROSE  # scripted group (container) (typed FeaturePython)
  Dunit = g/cm3
  Dvalue = 1.11
  Group = -> [H_element059,C_element065,N_element027,O_element067]
  conduct = 2
  density = 1
  expand = 3
  formula = G4_MUSCLE_WITH_SUCROSE
  name = G4_MUSCLE_WITH_SUCROSE
  specific = 4
FEATURE [App::DocumentObjectGroupPython] H_element060  label="H_element : 0.138"  # scripted group (container) (typed FeaturePython)
  n = 0.101969
FEATURE [App::DocumentObjectGroupPython] C_element066  label="C_element : 0.120"  # scripted group (container) (typed FeaturePython)
  n = 0.120058
FEATURE [App::DocumentObjectGroupPython] N_element028  label="N_element : 0.758"  # scripted group (container) (typed FeaturePython)
  n = 0.035451
FEATURE [App::DocumentObjectGroupPython] O_element068  label="O_element : 0.743"  # scripted group (container) (typed FeaturePython)
  n = 0.742522
FEATURE [App::DocumentObjectGroupPython] G4_MUSCLE_WITHOUT_SUCROSE  # scripted group (container) (typed FeaturePython)
  Dunit = g/cm3
  Dvalue = 1.07
  Group = -> [H_element060,C_element066,N_element028,O_element068]
  conduct = 2
  density = 1
  expand = 3
  formula = G4_MUSCLE_WITHOUT_SUCROSE
  name = G4_MUSCLE_WITHOUT_SUCROSE
  specific = 4
FEATURE [App::DocumentObjectGroupPython] C_element067  label="C_element : 10"  # scripted group (container) (typed FeaturePython)
  n = 10
  ref = C_element
FEATURE [App::DocumentObjectGroupPython] H_element061  label="H_element : 030"  # scripted group (container) (typed FeaturePython)
  n = 8
  ref = H_element
FEATURE [App::DocumentObjectGroupPython] G4_NAPHTHALENE  # scripted group (container) (typed FeaturePython)
  Dunit = g/cm3
  Dvalue = 1.145
  Group = -> [C_element067,H_element061]
  conduct = 2
  density = 1
  expand = 3
  formula = G4_NAPHTHALENE
  name = G4_NAPHTHALENE
  specific = 4
FEATURE [App::DocumentObjectGroupPython] C_element068  label="C_element : 034"  # scripted group (container) (typed FeaturePython)
  n = 6
  ref = C_element
FEATURE [App::DocumentObjectGroupPython] H_element062  label="H_element : 031"  # scripted group (container) (typed FeaturePython)
  n = 5
  ref = H_element
FEATURE [App::DocumentObjectGroupPython] N_element029  label="N_element : 012"  # scripted group (container) (typed FeaturePython)
  n = 1
  ref = N_element
FEATURE [App::DocumentObjectGroupPython] O_element069  label="O_element : 034"  # scripted group (container) (typed FeaturePython)
  n = 2
  ref = O_element
FEATURE [App::DocumentObjectGroupPython] G4_NITROBENZENE  # scripted group (container) (typed FeaturePython)
  Dunit = g/cm3
  Dvalue = 1.19867
  Group = -> [C_element068,H_element062,N_element029,O_element069]
  conduct = 2
  density = 1
  expand = 3
  formula = G4_NITROBENZENE
  name = G4_NITROBENZENE
  specific = 4
FEATURE [App::DocumentObjectGroupPython] N_element030  label="N_element : 013"  # scripted group (container) (typed FeaturePython)
  n = 2
  ref = N_element
FEATURE [App::DocumentObjectGroupPython] O_element070  label="O_element : 035"  # scripted group (container) (typed FeaturePython)
  n = 1
  ref = O_element
FEATURE [App::DocumentObjectGroupPython] G4_NITROUS_OXIDE  # scripted group (container) (typed FeaturePython)
  Dunit = g/cm3
  Dvalue = 0.00183094
  Group = -> [N_element030,O_element070]
  conduct = 2
  density = 1
  expand = 3
  formula = G4_NITROUS_OXIDE
  name = G4_NITROUS_OXIDE
  specific = 4
FEATURE [App::DocumentObjectGroupPython] H_element063  label="H_element : 0.104"  # scripted group (container) (typed FeaturePython)
  n = 0.103509
FEATURE [App::DocumentObjectGroupPython] C_element069  label="C_element : 0.648"  # scripted group (container) (typed FeaturePython)
  n = 0.648416
FEATURE [App::DocumentObjectGroupPython] N_element031  label="N_element : 0.100"  # scripted group (container) (typed FeaturePython)
  n = 0.0995361
FEATURE [App::DocumentObjectGroupPython] O_element071  label="O_element : 0.149"  # scripted group (container) (typed FeaturePython)
  n = 0.148539
FEATURE [App::DocumentObjectGroupPython] G4_NYLON_8062  label="G4_NYLON-8062"  # scripted group (container) (typed FeaturePython)
  Dunit = g/cm3
  Dvalue = 1.08
  Group = -> [H_element063,C_element069,N_element031,O_element071]
  conduct = 2
  density = 1
  expand = 3
  formula = G4_NYLON-8062
  name = G4_NYLON-8062
  specific = 4
FEATURE [App::DocumentObjectGroupPython] C_element070  label="C_element : 035"  # scripted group (container) (typed FeaturePython)
  n = 6
  ref = C_element
FEATURE [App::DocumentObjectGroupPython] H_element064  label="H_element : 11"  # scripted group (container) (typed FeaturePython)
  n = 11
  ref = H_element
FEATURE [App::DocumentObjectGroupPython] N_element032  label="N_element : 014"  # scripted group (container) (typed FeaturePython)
  n = 1
  ref = N_element
FEATURE [App::DocumentObjectGroupPython] O_element072  label="O_element : 036"  # scripted group (container) (typed FeaturePython)
  n = 1
  ref = O_element
FEATURE [App::DocumentObjectGroupPython] G4_NYLON_6_6  label="G4_NYLON-6-6"  # scripted group (container) (typed FeaturePython)
  Dunit = g/cm3
  Dvalue = 1.14
  Group = -> [C_element070,H_element064,N_element032,O_element072]
  conduct = 2
  density = 1
  expand = 3
  formula = G4_NYLON-6-6
  name = G4_NYLON-6-6
  specific = 4
FEATURE [App::DocumentObjectGroupPython] H_element065  label="H_element : 0.139"  # scripted group (container) (typed FeaturePython)
  n = 0.107062
FEATURE [App::DocumentObjectGroupPython] C_element071  label="C_element : 0.680"  # scripted group (container) (typed FeaturePython)
  n = 0.680449
FEATURE [App::DocumentObjectGroupPython] N_element033  label="N_element : 0.099"  # scripted group (container) (typed FeaturePython)
  n = 0.099189
FEATURE [App::DocumentObjectGroupPython] O_element073  label="O_element : 0.113"  # scripted group (container) (typed FeaturePython)
  n = 0.1133
FEATURE [App::DocumentObjectGroupPython] G4_NYLON_6_10  label="G4_NYLON-6-10"  # scripted group (container) (typed FeaturePython)
  Dunit = g/cm3
  Dvalue = 1.14
  Group = -> [H_element065,C_element071,N_element033,O_element073]
  conduct = 2
  density = 1
  expand = 3
  formula = G4_NYLON-6-10
  name = G4_NYLON-6-10
  specific = 4
FEATURE [App::DocumentObjectGroupPython] H_element066  label="H_element : 0.140"  # scripted group (container) (typed FeaturePython)
  n = 0.115476
FEATURE [App::DocumentObjectGroupPython] C_element072  label="C_element : 0.721"  # scripted group (container) (typed FeaturePython)
  n = 0.720818
FEATURE [App::DocumentObjectGroupPython] N_element034  label="N_element : 0.076"  # scripted group (container) (typed FeaturePython)
  n = 0.0764169
FEATURE [App::DocumentObjectGroupPython] O_element074  label="O_element : 0.087"  # scripted group (container) (typed FeaturePython)
  n = 0.0872889
FEATURE [App::DocumentObjectGroupPython] G4_NYLON_11_RILSAN  label="G4_NYLON-11_RILSAN"  # scripted group (container) (typed FeaturePython)
  Dunit = g/cm3
  Dvalue = 1.425
  Group = -> [H_element066,C_element072,N_element034,O_element074]
  conduct = 2
  density = 1
  expand = 3
  formula = G4_NYLON-11_RILSAN
  name = G4_NYLON-11_RILSAN
  specific = 4
FEATURE [App::DocumentObjectGroupPython] C_element073  label="C_element : 8"  # scripted group (container) (typed FeaturePython)
  n = 8
  ref = C_element
FEATURE [App::DocumentObjectGroupPython] H_element067  label="H_element : 18"  # scripted group (container) (typed FeaturePython)
  n = 18
  ref = H_element
FEATURE [App::DocumentObjectGroupPython] G4_OCTANE  # scripted group (container) (typed FeaturePython)
  Dunit = g/cm3
  Dvalue = 0.7026
  Group = -> [C_element073,H_element067]
  conduct = 2
  density = 1
  expand = 3
  formula = G4_OCTANE
  name = G4_OCTANE
  specific = 4
FEATURE [App::DocumentObjectGroupPython] C_element074  label="C_element : 25"  # scripted group (container) (typed FeaturePython)
  n = 25
  ref = C_element
FEATURE [App::DocumentObjectGroupPython] H_element068  label="H_element : 52"  # scripted group (container) (typed FeaturePython)
  n = 52
  ref = H_element
FEATURE [App::DocumentObjectGroupPython] G4_PARAFFIN  # scripted group (container) (typed FeaturePython)
  Dunit = g/cm3
  Dvalue = 0.93
  Group = -> [C_element074,H_element068]
  conduct = 2
  density = 1
  expand = 3
  formula = G4_PARAFFIN
  name = G4_PARAFFIN
  specific = 4
FEATURE [App::DocumentObjectGroupPython] C_element075  label="C_element : 036"  # scripted group (container) (typed FeaturePython)
  n = 5
  ref = C_element
FEATURE [App::DocumentObjectGroupPython] H_element069  label="H_element : 032"  # scripted group (container) (typed FeaturePython)
  n = 12
  ref = H_element
FEATURE [App::DocumentObjectGroupPython] G4_N_PENTANE  label="G4_N-PENTANE"  # scripted group (container) (typed FeaturePython)
  Dunit = g/cm3
  Dvalue = 0.6262
  Group = -> [C_element075,H_element069]
  conduct = 2
  density = 1
  expand = 3
  formula = G4_N-PENTANE
  name = G4_N-PENTANE
  specific = 4
FEATURE [App::DocumentObjectGroupPython] H_element070  label="H_element : 0.014"  # scripted group (container) (typed FeaturePython)
  n = 0.0141
FEATURE [App::DocumentObjectGroupPython] C_element076  label="C_element : 0.072"  # scripted group (container) (typed FeaturePython)
  n = 0.072261
FEATURE [App::DocumentObjectGroupPython] N_element035  label="N_element : 0.019"  # scripted group (container) (typed FeaturePython)
  n = 0.01932
FEATURE [App::DocumentObjectGroupPython] O_element075  label="O_element : 0.066"  # scripted group (container) (typed FeaturePython)
  n = 0.066101
FEATURE [App::DocumentObjectGroupPython] S_element019  label="S_element : 0.020"  # scripted group (container) (typed FeaturePython)
  n = 0.00189
FEATURE [App::DocumentObjectGroupPython] Br_element004  label="Br_element : 0.349"  # scripted group (container) (typed FeaturePython)
  n = 0.349103
FEATURE [App::DocumentObjectGroupPython] Ag_element001  label="Ag_element : 0.474"  # scripted group (container) (typed FeaturePython)
  n = 0.474105
FEATURE [App::DocumentObjectGroupPython] I_element005  label="I_element : 0.003"  # scripted group (container) (typed FeaturePython)
  n = 0.00312
FEATURE [App::DocumentObjectGroupPython] G4_PHOTO_EMULSION  # scripted group (container) (typed FeaturePython)
  Dunit = g/cm3
  Dvalue = 3.815
  Group = -> [H_element070,C_element076,N_element035,O_element075,S_element019,Br_element004,Ag_element001,I_element005]
  conduct = 2
  density = 1
  expand = 3
  formula = G4_PHOTO_EMULSION
  name = G4_PHOTO_EMULSION
  specific = 4
FEATURE [App::DocumentObjectGroupPython] C_element077  label="C_element : 9"  # scripted group (container) (typed FeaturePython)
  n = 9
  ref = C_element
FEATURE [App::DocumentObjectGroupPython] H_element071  label="H_element : 033"  # scripted group (container) (typed FeaturePython)
  n = 10
  ref = H_element
FEATURE [App::DocumentObjectGroupPython] G4_PLASTIC_SC_VINYLTOLUENE  # scripted group (container) (typed FeaturePython)
  Dunit = g/cm3
  Dvalue = 1.032
  Group = -> [C_element077,H_element071]
  conduct = 2
  density = 1
  expand = 3
  formula = G4_PLASTIC_SC_VINYLTOLUENE
  name = G4_PLASTIC_SC_VINYLTOLUENE
  specific = 4
FEATURE [App::DocumentObjectGroupPython] Pu_element001  label="Pu_element : 1"  # scripted group (container) (typed FeaturePython)
  n = 1
  ref = Pu_element
FEATURE [App::DocumentObjectGroupPython] O_element076  label="O_element : 037"  # scripted group (container) (typed FeaturePython)
  n = 2
  ref = O_element
FEATURE [App::DocumentObjectGroupPython] G4_PLUTONIUM_DIOXIDE  # scripted group (container) (typed FeaturePython)
  Dunit = g/cm3
  Dvalue = 11.46
  Group = -> [Pu_element001,O_element076]
  conduct = 2
  density = 1
  expand = 3
  formula = G4_PLUTONIUM_DIOXIDE
  name = G4_PLUTONIUM_DIOXIDE
  specific = 4
FEATURE [App::DocumentObjectGroupPython] C_element078  label="C_element : 037"  # scripted group (container) (typed FeaturePython)
  n = 3
  ref = C_element
FEATURE [App::DocumentObjectGroupPython] H_element072  label="H_element : 034"  # scripted group (container) (typed FeaturePython)
  n = 3
  ref = H_element
FEATURE [App::DocumentObjectGroupPython] N_element036  label="N_element : 015"  # scripted group (container) (typed FeaturePython)
  n = 1
  ref = N_element
FEATURE [App::DocumentObjectGroupPython] G4_POLYACRYLONITRILE  # scripted group (container) (typed FeaturePython)
  Dunit = g/cm3
  Dvalue = 1.17
  Group = -> [C_element078,H_element072,N_element036]
  conduct = 2
  density = 1
  expand = 3
  formula = G4_POLYACRYLONITRILE
  name = G4_POLYACRYLONITRILE
  specific = 4
FEATURE [App::DocumentObjectGroupPython] C_element079  label="C_element : 16"  # scripted group (container) (typed FeaturePython)
  n = 16
  ref = C_element
FEATURE [App::DocumentObjectGroupPython] H_element073  label="H_element : 035"  # scripted group (container) (typed FeaturePython)
  n = 14
  ref = H_element
FEATURE [App::DocumentObjectGroupPython] O_element077  label="O_element : 038"  # scripted group (container) (typed FeaturePython)
  n = 3
  ref = O_element
FEATURE [App::DocumentObjectGroupPython] G4_POLYCARBONATE  # scripted group (container) (typed FeaturePython)
  Dunit = g/cm3
  Dvalue = 1.2
  Group = -> [C_element079,H_element073,O_element077]
  conduct = 2
  density = 1
  expand = 3
  formula = G4_POLYCARBONATE
  name = G4_POLYCARBONATE
  specific = 4
FEATURE [App::DocumentObjectGroupPython] C_element080  label="C_element : 038"  # scripted group (container) (typed FeaturePython)
  n = 8
  ref = C_element
FEATURE [App::DocumentObjectGroupPython] H_element074  label="H_element : 036"  # scripted group (container) (typed FeaturePython)
  n = 7
  ref = H_element
FEATURE [App::DocumentObjectGroupPython] Cl_element017  label="Cl_element : 007"  # scripted group (container) (typed FeaturePython)
  n = 1
  ref = Cl_element
FEATURE [App::DocumentObjectGroupPython] G4_POLYCHLOROSTYRENE  # scripted group (container) (typed FeaturePython)
  Dunit = g/cm3
  Dvalue = 1.3
  Group = -> [C_element080,H_element074,Cl_element017]
  conduct = 2
  density = 1
  expand = 3
  formula = G4_POLYCHLOROSTYRENE
  name = G4_POLYCHLOROSTYRENE
  specific = 4
FEATURE [App::DocumentObjectGroupPython] C_element081  label="C_element : 039"  # scripted group (container) (typed FeaturePython)
  n = 1
  ref = C_element
FEATURE [App::DocumentObjectGroupPython] H_element075  label="H_element : 037"  # scripted group (container) (typed FeaturePython)
  n = 2
  ref = H_element
FEATURE [App::DocumentObjectGroupPython] G4_POLYETHYLENE  # scripted group (container) (typed FeaturePython)
  Dunit = g/cm3
  Dvalue = 0.94
  Group = -> [C_element081,H_element075]
  conduct = 2
  density = 1
  expand = 3
  formula = G4_POLYETHYLENE
  name = G4_POLYETHYLENE
  specific = 4
FEATURE [App::DocumentObjectGroupPython] C_element082  label="C_element : 040"  # scripted group (container) (typed FeaturePython)
  n = 10
  ref = C_element
FEATURE [App::DocumentObjectGroupPython] H_element076  label="H_element : 038"  # scripted group (container) (typed FeaturePython)
  n = 8
  ref = H_element
FEATURE [App::DocumentObjectGroupPython] O_element078  label="O_element : 039"  # scripted group (container) (typed FeaturePython)
  n = 4
  ref = O_element
FEATURE [App::DocumentObjectGroupPython] G4_MYLAR  # scripted group (container) (typed FeaturePython)
  Dunit = g/cm3
  Dvalue = 1.4
  Group = -> [C_element082,H_element076,O_element078]
  conduct = 2
  density = 1
  expand = 3
  formula = G4_MYLAR
  name = G4_MYLAR
  specific = 4
FEATURE [App::DocumentObjectGroupPython] C_element083  label="C_element : 041"  # scripted group (container) (typed FeaturePython)
  n = 5
  ref = C_element
FEATURE [App::DocumentObjectGroupPython] H_element077  label="H_element : 039"  # scripted group (container) (typed FeaturePython)
  n = 8
  ref = H_element
FEATURE [App::DocumentObjectGroupPython] O_element079  label="O_element : 040"  # scripted group (container) (typed FeaturePython)
  n = 2
  ref = O_element
FEATURE [App::DocumentObjectGroupPython] G4_PLEXIGLASS  # scripted group (container) (typed FeaturePython)
  Dunit = g/cm3
  Dvalue = 1.19
  Group = -> [C_element083,H_element077,O_element079]
  conduct = 2
  density = 1
  expand = 3
  formula = G4_PLEXIGLASS
  name = G4_PLEXIGLASS
  specific = 4
FEATURE [App::DocumentObjectGroupPython] C_element084  label="C_element : 042"  # scripted group (container) (typed FeaturePython)
  n = 1
  ref = C_element
FEATURE [App::DocumentObjectGroupPython] H_element078  label="H_element : 040"  # scripted group (container) (typed FeaturePython)
  n = 2
  ref = H_element
FEATURE [App::DocumentObjectGroupPython] O_element080  label="O_element : 041"  # scripted group (container) (typed FeaturePython)
  n = 1
  ref = O_element
FEATURE [App::DocumentObjectGroupPython] G4_POLYOXYMETHYLENE  # scripted group (container) (typed FeaturePython)
  Dunit = g/cm3
  Dvalue = 1.425
  Group = -> [C_element084,H_element078,O_element080]
  conduct = 2
  density = 1
  expand = 3
  formula = G4_POLYOXYMETHYLENE
  name = G4_POLYOXYMETHYLENE
  specific = 4
FEATURE [App::DocumentObjectGroupPython] C_element085  label="C_element : 043"  # scripted group (container) (typed FeaturePython)
  n = 2
  ref = C_element
FEATURE [App::DocumentObjectGroupPython] H_element079  label="H_element : 041"  # scripted group (container) (typed FeaturePython)
  n = 4
  ref = H_element
FEATURE [App::DocumentObjectGroupPython] G4_POLYPROPYLENE  # scripted group (container) (typed FeaturePython)
  Dunit = g/cm3
  Dvalue = 0.9
  Group = -> [C_element085,H_element079]
  conduct = 2
  density = 1
  expand = 3
  formula = G4_POLYPROPYLENE
  name = G4_POLYPROPYLENE
  specific = 4
FEATURE [App::DocumentObjectGroupPython] C_element086  label="C_element : 044"  # scripted group (container) (typed FeaturePython)
  n = 8
  ref = C_element
FEATURE [App::DocumentObjectGroupPython] H_element080  label="H_element : 042"  # scripted group (container) (typed FeaturePython)
  n = 8
  ref = H_element
FEATURE [App::DocumentObjectGroupPython] G4_POLYSTYRENE  # scripted group (container) (typed FeaturePython)
  Dunit = g/cm3
  Dvalue = 1.06
  Group = -> [C_element086,H_element080]
  conduct = 2
  density = 1
  expand = 3
  formula = G4_POLYSTYRENE
  name = G4_POLYSTYRENE
  specific = 4
FEATURE [App::DocumentObjectGroupPython] C_element087  label="C_element : 045"  # scripted group (container) (typed FeaturePython)
  n = 2
  ref = C_element
FEATURE [App::DocumentObjectGroupPython] F_element014  label="F_element : 4"  # scripted group (container) (typed FeaturePython)
  n = 4
  ref = F_element
FEATURE [App::DocumentObjectGroupPython] G4_TEFLON  # scripted group (container) (typed FeaturePython)
  Dunit = g/cm3
  Dvalue = 2.2
  Group = -> [C_element087,F_element014]
  conduct = 2
  density = 1
  expand = 3
  formula = G4_TEFLON
  name = G4_TEFLON
  specific = 4
FEATURE [App::DocumentObjectGroupPython] C_element088  label="C_element : 046"  # scripted group (container) (typed FeaturePython)
  n = 2
  ref = C_element
FEATURE [App::DocumentObjectGroupPython] F_element015  label="F_element : 006"  # scripted group (container) (typed FeaturePython)
  n = 3
  ref = F_element
FEATURE [App::DocumentObjectGroupPython] Cl_element018  label="Cl_element : 008"  # scripted group (container) (typed FeaturePython)
  n = 1
  ref = Cl_element
FEATURE [App::DocumentObjectGroupPython] G4_POLYTRIFLUOROCHLOROETHYLENE  # scripted group (container) (typed FeaturePython)
  Dunit = g/cm3
  Dvalue = 2.1
  Group = -> [C_element088,F_element015,Cl_element018]
  conduct = 2
  density = 1
  expand = 3
  formula = G4_POLYTRIFLUOROCHLOROETHYLENE
  name = G4_POLYTRIFLUOROCHLOROETHYLENE
  specific = 4
FEATURE [App::DocumentObjectGroupPython] C_element089  label="C_element : 047"  # scripted group (container) (typed FeaturePython)
  n = 4
  ref = C_element
FEATURE [App::DocumentObjectGroupPython] H_element081  label="H_element : 043"  # scripted group (container) (typed FeaturePython)
  n = 6
  ref = H_element
FEATURE [App::DocumentObjectGroupPython] O_element081  label="O_element : 042"  # scripted group (container) (typed FeaturePython)
  n = 2
  ref = O_element
FEATURE [App::DocumentObjectGroupPython] G4_POLYVINYL_ACETATE  # scripted group (container) (typed FeaturePython)
  Dunit = g/cm3
  Dvalue = 1.19
  Group = -> [C_element089,H_element081,O_element081]
  conduct = 2
  density = 1
  expand = 3
  formula = G4_POLYVINYL_ACETATE
  name = G4_POLYVINYL_ACETATE
  specific = 4
FEATURE [App::DocumentObjectGroupPython] C_element090  label="C_element : 048"  # scripted group (container) (typed FeaturePython)
  n = 2
  ref = C_element
FEATURE [App::DocumentObjectGroupPython] H_element082  label="H_element : 044"  # scripted group (container) (typed FeaturePython)
  n = 4
  ref = H_element
FEATURE [App::DocumentObjectGroupPython] O_element082  label="O_element : 043"  # scripted group (container) (typed FeaturePython)
  n = 1
  ref = O_element
FEATURE [App::DocumentObjectGroupPython] G4_POLYVINYL_ALCOHOL  # scripted group (container) (typed FeaturePython)
  Dunit = g/cm3
  Dvalue = 1.3
  Group = -> [C_element090,H_element082,O_element082]
  conduct = 2
  density = 1
  expand = 3
  formula = G4_POLYVINYL_ALCOHOL
  name = G4_POLYVINYL_ALCOHOL
  specific = 4
FEATURE [App::DocumentObjectGroupPython] C_element091  label="C_element : 049"  # scripted group (container) (typed FeaturePython)
  n = 8
  ref = C_element
FEATURE [App::DocumentObjectGroupPython] H_element083  label="H_element : 045"  # scripted group (container) (typed FeaturePython)
  n = 14
  ref = H_element
FEATURE [App::DocumentObjectGroupPython] O_element083  label="O_element : 044"  # scripted group (container) (typed FeaturePython)
  n = 2
  ref = O_element
FEATURE [App::DocumentObjectGroupPython] G4_POLYVINYL_BUTYRAL  # scripted group (container) (typed FeaturePython)
  Dunit = g/cm3
  Dvalue = 1.12
  Group = -> [C_element091,H_element083,O_element083]
  conduct = 2
  density = 1
  expand = 3
  formula = G4_POLYVINYL_BUTYRAL
  name = G4_POLYVINYL_BUTYRAL
  specific = 4
FEATURE [App::DocumentObjectGroupPython] C_element092  label="C_element : 050"  # scripted group (container) (typed FeaturePython)
  n = 2
  ref = C_element
FEATURE [App::DocumentObjectGroupPython] H_element084  label="H_element : 046"  # scripted group (container) (typed FeaturePython)
  n = 3
  ref = H_element
FEATURE [App::DocumentObjectGroupPython] Cl_element019  label="Cl_element : 009"  # scripted group (container) (typed FeaturePython)
  n = 1
  ref = Cl_element
FEATURE [App::DocumentObjectGroupPython] G4_POLYVINYL_CHLORIDE  # scripted group (container) (typed FeaturePython)
  Dunit = g/cm3
  Dvalue = 1.3
  Group = -> [C_element092,H_element084,Cl_element019]
  conduct = 2
  density = 1
  expand = 3
  formula = G4_POLYVINYL_CHLORIDE
  name = G4_POLYVINYL_CHLORIDE
  specific = 4
FEATURE [App::DocumentObjectGroupPython] C_element093  label="C_element : 051"  # scripted group (container) (typed FeaturePython)
  n = 2
  ref = C_element
FEATURE [App::DocumentObjectGroupPython] H_element085  label="H_element : 047"  # scripted group (container) (typed FeaturePython)
  n = 2
  ref = H_element
FEATURE [App::DocumentObjectGroupPython] Cl_element020  label="Cl_element : 010"  # scripted group (container) (typed FeaturePython)
  n = 2
  ref = Cl_element
FEATURE [App::DocumentObjectGroupPython] G4_POLYVINYLIDENE_CHLORIDE  # scripted group (container) (typed FeaturePython)
  Dunit = g/cm3
  Dvalue = 1.7
  Group = -> [C_element093,H_element085,Cl_element020]
  conduct = 2
  density = 1
  expand = 3
  formula = G4_POLYVINYLIDENE_CHLORIDE
  name = G4_POLYVINYLIDENE_CHLORIDE
  specific = 4
FEATURE [App::DocumentObjectGroupPython] C_element094  label="C_element : 052"  # scripted group (container) (typed FeaturePython)
  n = 2
  ref = C_element
FEATURE [App::DocumentObjectGroupPython] H_element086  label="H_element : 048"  # scripted group (container) (typed FeaturePython)
  n = 2
  ref = H_element
FEATURE [App::DocumentObjectGroupPython] F_element016  label="F_element : 007"  # scripted group (container) (typed FeaturePython)
  n = 2
  ref = F_element
FEATURE [App::DocumentObjectGroupPython] G4_POLYVINYLIDENE_FLUORIDE  # scripted group (container) (typed FeaturePython)
  Dunit = g/cm3
  Dvalue = 1.76
  Group = -> [C_element094,H_element086,F_element016]
  conduct = 2
  density = 1
  expand = 3
  formula = G4_POLYVINYLIDENE_FLUORIDE
  name = G4_POLYVINYLIDENE_FLUORIDE
  specific = 4
FEATURE [App::DocumentObjectGroupPython] C_element095  label="C_element : 053"  # scripted group (container) (typed FeaturePython)
  n = 6
  ref = C_element
FEATURE [App::DocumentObjectGroupPython] H_element087  label="H_element : 9"  # scripted group (container) (typed FeaturePython)
  n = 9
  ref = H_element
FEATURE [App::DocumentObjectGroupPython] N_element037  label="N_element : 016"  # scripted group (container) (typed FeaturePython)
  n = 1
  ref = N_element
FEATURE [App::DocumentObjectGroupPython] O_element084  label="O_element : 045"  # scripted group (container) (typed FeaturePython)
  n = 1
  ref = O_element
FEATURE [App::DocumentObjectGroupPython] G4_POLYVINYL_PYRROLIDONE  # scripted group (container) (typed FeaturePython)
  Dunit = g/cm3
  Dvalue = 1.25
  Group = -> [C_element095,H_element087,N_element037,O_element084]
  conduct = 2
  density = 1
  expand = 3
  formula = G4_POLYVINYL_PYRROLIDONE
  name = G4_POLYVINYL_PYRROLIDONE
  specific = 4
FEATURE [App::DocumentObjectGroupPython] K_element008  label="K_element : 1"  # scripted group (container) (typed FeaturePython)
  n = 1
  ref = K_element
FEATURE [App::DocumentObjectGroupPython] I_element006  label="I_element : 003"  # scripted group (container) (typed FeaturePython)
  n = 1
  ref = I_element
FEATURE [App::DocumentObjectGroupPython] G4_POTASSIUM_IODIDE  # scripted group (container) (typed FeaturePython)
  Dunit = g/cm3
  Dvalue = 3.13
  Group = -> [K_element008,I_element006]
  conduct = 2
  density = 1
  expand = 3
  formula = G4_POTASSIUM_IODIDE
  name = G4_POTASSIUM_IODIDE
  specific = 4
FEATURE [App::DocumentObjectGroupPython] K_element009  label="K_element : 2"  # scripted group (container) (typed FeaturePython)
  n = 2
  ref = K_element
FEATURE [App::DocumentObjectGroupPython] O_element085  label="O_element : 046"  # scripted group (container) (typed FeaturePython)
  n = 1
  ref = O_element
FEATURE [App::DocumentObjectGroupPython] G4_POTASSIUM_OXIDE  # scripted group (container) (typed FeaturePython)
  Dunit = g/cm3
  Dvalue = 2.32
  Group = -> [K_element009,O_element085]
  conduct = 2
  density = 1
  expand = 3
  formula = G4_POTASSIUM_OXIDE
  name = G4_POTASSIUM_OXIDE
  specific = 4
FEATURE [App::DocumentObjectGroupPython] C_element096  label="C_element : 054"  # scripted group (container) (typed FeaturePython)
  n = 3
  ref = C_element
FEATURE [App::DocumentObjectGroupPython] H_element088  label="H_element : 049"  # scripted group (container) (typed FeaturePython)
  n = 8
  ref = H_element
FEATURE [App::DocumentObjectGroupPython] G4_PROPANE  # scripted group (container) (typed FeaturePython)
  Dunit = g/cm3
  Dvalue = 0.00187939
  Group = -> [C_element096,H_element088]
  conduct = 2
  density = 1
  expand = 3
  formula = G4_PROPANE
  name = G4_PROPANE
  specific = 4
FEATURE [App::DocumentObjectGroupPython] C_element097  label="C_element : 055"  # scripted group (container) (typed FeaturePython)
  n = 3
  ref = C_element
FEATURE [App::DocumentObjectGroupPython] H_element089  label="H_element : 050"  # scripted group (container) (typed FeaturePython)
  n = 8
  ref = H_element
FEATURE [App::DocumentObjectGroupPython] G4_lPROPANE  # scripted group (container) (typed FeaturePython)
  Dunit = g/cm3
  Dvalue = 0.43
  Group = -> [C_element097,H_element089]
  conduct = 2
  density = 1
  expand = 3
  formula = G4_lPROPANE
  name = G4_lPROPANE
  specific = 4
FEATURE [App::DocumentObjectGroupPython] C_element098  label="C_element : 056"  # scripted group (container) (typed FeaturePython)
  n = 3
  ref = C_element
FEATURE [App::DocumentObjectGroupPython] H_element090  label="H_element : 051"  # scripted group (container) (typed FeaturePython)
  n = 8
  ref = H_element
FEATURE [App::DocumentObjectGroupPython] O_element086  label="O_element : 047"  # scripted group (container) (typed FeaturePython)
  n = 1
  ref = O_element
FEATURE [App::DocumentObjectGroupPython] G4_N_PROPYL_ALCOHOL  label="G4_N-PROPYL_ALCOHOL"  # scripted group (container) (typed FeaturePython)
  Dunit = g/cm3
  Dvalue = 0.8035
  Group = -> [C_element098,H_element090,O_element086]
  conduct = 2
  density = 1
  expand = 3
  formula = G4_N-PROPYL_ALCOHOL
  name = G4_N-PROPYL_ALCOHOL
  specific = 4
FEATURE [App::DocumentObjectGroupPython] C_element099  label="C_element : 057"  # scripted group (container) (typed FeaturePython)
  n = 5
  ref = C_element
FEATURE [App::DocumentObjectGroupPython] H_element091  label="H_element : 052"  # scripted group (container) (typed FeaturePython)
  n = 5
  ref = H_element
FEATURE [App::DocumentObjectGroupPython] N_element038  label="N_element : 017"  # scripted group (container) (typed FeaturePython)
  n = 1
  ref = N_element
FEATURE [App::DocumentObjectGroupPython] G4_PYRIDINE  # scripted group (container) (typed FeaturePython)
  Dunit = g/cm3
  Dvalue = 0.9819
  Group = -> [C_element099,H_element091,N_element038]
  conduct = 2
  density = 1
  expand = 3
  formula = G4_PYRIDINE
  name = G4_PYRIDINE
  specific = 4
FEATURE [App::DocumentObjectGroupPython] H_element092  label="H_element : 0.144"  # scripted group (container) (typed FeaturePython)
  n = 0.143711
FEATURE [App::DocumentObjectGroupPython] C_element100  label="C_element : 0.856"  # scripted group (container) (typed FeaturePython)
  n = 0.856289
FEATURE [App::DocumentObjectGroupPython] G4_RUBBER_BUTYL  # scripted group (container) (typed FeaturePython)
  Dunit = g/cm3
  Dvalue = 0.92
  Group = -> [H_element092,C_element100]
  conduct = 2
  density = 1
  expand = 3
  formula = G4_RUBBER_BUTYL
  name = G4_RUBBER_BUTYL
  specific = 4
FEATURE [App::DocumentObjectGroupPython] H_element093  label="H_element : 0.118"  # scripted group (container) (typed FeaturePython)
  n = 0.118371
FEATURE [App::DocumentObjectGroupPython] C_element101  label="C_element : 0.882"  # scripted group (container) (typed FeaturePython)
  n = 0.881629
FEATURE [App::DocumentObjectGroupPython] G4_RUBBER_NATURAL  # scripted group (container) (typed FeaturePython)
  Dunit = g/cm3
  Dvalue = 0.92
  Group = -> [H_element093,C_element101]
  conduct = 2
  density = 1
  expand = 3
  formula = G4_RUBBER_NATURAL
  name = G4_RUBBER_NATURAL
  specific = 4
FEATURE [App::DocumentObjectGroupPython] H_element094  label="H_element : 0.145"  # scripted group (container) (typed FeaturePython)
  n = 0.05692
FEATURE [App::DocumentObjectGroupPython] C_element102  label="C_element : 0.543"  # scripted group (container) (typed FeaturePython)
  n = 0.542646
FEATURE [App::DocumentObjectGroupPython] Cl_element021  label="Cl_element : 0.400"  # scripted group (container) (typed FeaturePython)
  n = 0.400434
FEATURE [App::DocumentObjectGroupPython] G4_RUBBER_NEOPRENE  # scripted group (container) (typed FeaturePython)
  Dunit = g/cm3
  Dvalue = 1.23
  Group = -> [H_element094,C_element102,Cl_element021]
  conduct = 2
  density = 1
  expand = 3
  formula = G4_RUBBER_NEOPRENE
  name = G4_RUBBER_NEOPRENE
  specific = 4
FEATURE [App::DocumentObjectGroupPython] Si_element006  label="Si_element : 1"  # scripted group (container) (typed FeaturePython)
  n = 1
  ref = Si_element
FEATURE [App::DocumentObjectGroupPython] O_element087  label="O_element : 048"  # scripted group (container) (typed FeaturePython)
  n = 2
  ref = O_element
FEATURE [App::DocumentObjectGroupPython] G4_SILICON_DIOXIDE  # scripted group (container) (typed FeaturePython)
  Dunit = g/cm3
  Dvalue = 2.32
  Group = -> [Si_element006,O_element087]
  conduct = 2
  density = 1
  expand = 3
  formula = G4_SILICON_DIOXIDE
  name = G4_SILICON_DIOXIDE
  specific = 4
FEATURE [App::DocumentObjectGroupPython] Ag_element002  label="Ag_element : 1"  # scripted group (container) (typed FeaturePython)
  n = 1
  ref = Ag_element
FEATURE [App::DocumentObjectGroupPython] Br_element005  label="Br_element : 003"  # scripted group (container) (typed FeaturePython)
  n = 1
  ref = Br_element
FEATURE [App::DocumentObjectGroupPython] G4_SILVER_BROMIDE  # scripted group (container) (typed FeaturePython)
  Dunit = g/cm3
  Dvalue = 6.473
  Group = -> [Ag_element002,Br_element005]
  conduct = 2
  density = 1
  expand = 3
  formula = G4_SILVER_BROMIDE
  name = G4_SILVER_BROMIDE
  specific = 4
FEATURE [App::DocumentObjectGroupPython] Ag_element003  label="Ag_element : 002"  # scripted group (container) (typed FeaturePython)
  n = 1
  ref = Ag_element
FEATURE [App::DocumentObjectGroupPython] Cl_element022  label="Cl_element : 011"  # scripted group (container) (typed FeaturePython)
  n = 1
  ref = Cl_element
FEATURE [App::DocumentObjectGroupPython] G4_SILVER_CHLORIDE  # scripted group (container) (typed FeaturePython)
  Dunit = g/cm3
  Dvalue = 5.56
  Group = -> [Ag_element003,Cl_element022]
  conduct = 2
  density = 1
  expand = 3
  formula = G4_SILVER_CHLORIDE
  name = G4_SILVER_CHLORIDE
  specific = 4
FEATURE [App::DocumentObjectGroupPython] Br_element006  label="Br_element : 0.423"  # scripted group (container) (typed FeaturePython)
  n = 0.422895
FEATURE [App::DocumentObjectGroupPython] Ag_element004  label="Ag_element : 0.574"  # scripted group (container) (typed FeaturePython)
  n = 0.573748
FEATURE [App::DocumentObjectGroupPython] I_element007  label="I_element : 0.649"  # scripted group (container) (typed FeaturePython)
  n = 0.003357
FEATURE [App::DocumentObjectGroupPython] G4_SILVER_HALIDES  # scripted group (container) (typed FeaturePython)
  Dunit = g/cm3
  Dvalue = 6.47
  Group = -> [Br_element006,Ag_element004,I_element007]
  conduct = 2
  density = 1
  expand = 3
  formula = G4_SILVER_HALIDES
  name = G4_SILVER_HALIDES
  specific = 4
FEATURE [App::DocumentObjectGroupPython] Ag_element005  label="Ag_element : 003"  # scripted group (container) (typed FeaturePython)
  n = 1
  ref = Ag_element
FEATURE [App::DocumentObjectGroupPython] I_element008  label="I_element : 004"  # scripted group (container) (typed FeaturePython)
  n = 1
  ref = I_element
FEATURE [App::DocumentObjectGroupPython] G4_SILVER_IODIDE  # scripted group (container) (typed FeaturePython)
  Dunit = g/cm3
  Dvalue = 6.01
  Group = -> [Ag_element005,I_element008]
  conduct = 2
  density = 1
  expand = 3
  formula = G4_SILVER_IODIDE
  name = G4_SILVER_IODIDE
  specific = 4
FEATURE [App::DocumentObjectGroupPython] H_element095  label="H_element : 0.100"  # scripted group (container) (typed FeaturePython)
  n = 0.1
FEATURE [App::DocumentObjectGroupPython] C_element103  label="C_element : 0.204"  # scripted group (container) (typed FeaturePython)
  n = 0.204
FEATURE [App::DocumentObjectGroupPython] N_element039  label="N_element : 0.759"  # scripted group (container) (typed FeaturePython)
  n = 0.042
FEATURE [App::DocumentObjectGroupPython] O_element088  label="O_element : 0.645"  # scripted group (container) (typed FeaturePython)
  n = 0.645
FEATURE [App::DocumentObjectGroupPython] Na_element013  label="Na_element : 0.100"  # scripted group (container) (typed FeaturePython)
  n = 0.002
FEATURE [App::DocumentObjectGroupPython] P_element009  label="P_element : 0.107"  # scripted group (container) (typed FeaturePython)
  n = 0.001
FEATURE [App::DocumentObjectGroupPython] S_element020  label="S_element : 0.021"  # scripted group (container) (typed FeaturePython)
  n = 0.002
FEATURE [App::DocumentObjectGroupPython] Cl_element023  label="Cl_element : 0.590"  # scripted group (container) (typed FeaturePython)
  n = 0.003
FEATURE [App::DocumentObjectGroupPython] K_element010  label="K_element : 0.001"  # scripted group (container) (typed FeaturePython)
  n = 0.001
FEATURE [App::DocumentObjectGroupPython] G4_SKIN_ICRP  # scripted group (container) (typed FeaturePython)
  Dunit = g/cm3
  Dvalue = 1.09
  Group = -> [H_element095,C_element103,N_element039,O_element088,Na_element013,P_element009,S_element020,Cl_element023,K_element010]
  conduct = 2
  density = 1
  expand = 3
  formula = G4_SKIN_ICRP
  name = G4_SKIN_ICRP
  specific = 4
FEATURE [App::DocumentObjectGroupPython] Na_element014  label="Na_element : 2"  # scripted group (container) (typed FeaturePython)
  n = 2
  ref = Na_element
FEATURE [App::DocumentObjectGroupPython] C_element104  label="C_element : 058"  # scripted group (container) (typed FeaturePython)
  n = 1
  ref = C_element
FEATURE [App::DocumentObjectGroupPython] O_element089  label="O_element : 049"  # scripted group (container) (typed FeaturePython)
  n = 3
  ref = O_element
FEATURE [App::DocumentObjectGroupPython] G4_SODIUM_CARBONATE  # scripted group (container) (typed FeaturePython)
  Dunit = g/cm3
  Dvalue = 2.532
  Group = -> [Na_element014,C_element104,O_element089]
  conduct = 2
  density = 1
  expand = 3
  formula = G4_SODIUM_CARBONATE
  name = G4_SODIUM_CARBONATE
  specific = 4
FEATURE [App::DocumentObjectGroupPython] Na_element015  label="Na_element : 1"  # scripted group (container) (typed FeaturePython)
  n = 1
  ref = Na_element
FEATURE [App::DocumentObjectGroupPython] I_element009  label="I_element : 005"  # scripted group (container) (typed FeaturePython)
  n = 1
  ref = I_element
FEATURE [App::DocumentObjectGroupPython] G4_SODIUM_IODIDE  # scripted group (container) (typed FeaturePython)
  Dunit = g/cm3
  Dvalue = 3.667
  Group = -> [Na_element015,I_element009]
  conduct = 2
  density = 1
  expand = 3
  formula = G4_SODIUM_IODIDE
  name = G4_SODIUM_IODIDE
  specific = 4
FEATURE [App::DocumentObjectGroupPython] Na_element016  label="Na_element : 003"  # scripted group (container) (typed FeaturePython)
  n = 2
  ref = Na_element
FEATURE [App::DocumentObjectGroupPython] O_element090  label="O_element : 050"  # scripted group (container) (typed FeaturePython)
  n = 1
  ref = O_element
FEATURE [App::DocumentObjectGroupPython] G4_SODIUM_MONOXIDE  # scripted group (container) (typed FeaturePython)
  Dunit = g/cm3
  Dvalue = 2.27
  Group = -> [Na_element016,O_element090]
  conduct = 2
  density = 1
  expand = 3
  formula = G4_SODIUM_MONOXIDE
  name = G4_SODIUM_MONOXIDE
  specific = 4
FEATURE [App::DocumentObjectGroupPython] Na_element017  label="Na_element : 004"  # scripted group (container) (typed FeaturePython)
  n = 1
  ref = Na_element
FEATURE [App::DocumentObjectGroupPython] N_element040  label="N_element : 018"  # scripted group (container) (typed FeaturePython)
  n = 1
  ref = N_element
FEATURE [App::DocumentObjectGroupPython] O_element091  label="O_element : 051"  # scripted group (container) (typed FeaturePython)
  n = 3
  ref = O_element
FEATURE [App::DocumentObjectGroupPython] G4_SODIUM_NITRATE  # scripted group (container) (typed FeaturePython)
  Dunit = g/cm3
  Dvalue = 2.261
  Group = -> [Na_element017,N_element040,O_element091]
  conduct = 2
  density = 1
  expand = 3
  formula = G4_SODIUM_NITRATE
  name = G4_SODIUM_NITRATE
  specific = 4
FEATURE [App::DocumentObjectGroupPython] C_element105  label="C_element : 059"  # scripted group (container) (typed FeaturePython)
  n = 14
  ref = C_element
FEATURE [App::DocumentObjectGroupPython] H_element096  label="H_element : 053"  # scripted group (container) (typed FeaturePython)
  n = 12
  ref = H_element
FEATURE [App::DocumentObjectGroupPython] G4_STILBENE  # scripted group (container) (typed FeaturePython)
  Dunit = g/cm3
  Dvalue = 0.9707
  Group = -> [C_element105,H_element096]
  conduct = 2
  density = 1
  expand = 3
  formula = G4_STILBENE
  name = G4_STILBENE
  specific = 4
FEATURE [App::DocumentObjectGroupPython] C_element106  label="C_element : 12"  # scripted group (container) (typed FeaturePython)
  n = 12
  ref = C_element
FEATURE [App::DocumentObjectGroupPython] H_element097  label="H_element : 22"  # scripted group (container) (typed FeaturePython)
  n = 22
  ref = H_element
FEATURE [App::DocumentObjectGroupPython] O_element092  label="O_element : 11"  # scripted group (container) (typed FeaturePython)
  n = 11
  ref = O_element
FEATURE [App::DocumentObjectGroupPython] G4_SUCROSE  # scripted group (container) (typed FeaturePython)
  Dunit = g/cm3
  Dvalue = 1.5805
  Group = -> [C_element106,H_element097,O_element092]
  conduct = 2
  density = 1
  expand = 3
  formula = G4_SUCROSE
  name = G4_SUCROSE
  specific = 4
FEATURE [App::DocumentObjectGroupPython] C_element107  label="C_element : 18"  # scripted group (container) (typed FeaturePython)
  n = 18
  ref = C_element
FEATURE [App::DocumentObjectGroupPython] H_element098  label="H_element : 054"  # scripted group (container) (typed FeaturePython)
  n = 14
  ref = H_element
FEATURE [App::DocumentObjectGroupPython] G4_TERPHENYL  # scripted group (container) (typed FeaturePython)
  Dunit = g/cm3
  Dvalue = 1.24
  Group = -> [C_element107,H_element098]
  conduct = 2
  density = 1
  expand = 3
  formula = G4_TERPHENYL
  name = G4_TERPHENYL
  specific = 4
FEATURE [App::DocumentObjectGroupPython] H_element099  label="H_element : 0.146"  # scripted group (container) (typed FeaturePython)
  n = 0.106
FEATURE [App::DocumentObjectGroupPython] C_element108  label="C_element : 0.883"  # scripted group (container) (typed FeaturePython)
  n = 0.099
FEATURE [App::DocumentObjectGroupPython] N_element041  label="N_element : 0.020"  # scripted group (container) (typed FeaturePython)
  n = 0.02
FEATURE [App::DocumentObjectGroupPython] O_element093  label="O_element : 0.766"  # scripted group (container) (typed FeaturePython)
  n = 0.766
FEATURE [App::DocumentObjectGroupPython] Na_element018  label="Na_element : 0.101"  # scripted group (container) (typed FeaturePython)
  n = 0.002
FEATURE [App::DocumentObjectGroupPython] P_element010  label="P_element : 0.108"  # scripted group (container) (typed FeaturePython)
  n = 0.001
FEATURE [App::DocumentObjectGroupPython] S_element021  label="S_element : 0.022"  # scripted group (container) (typed FeaturePython)
  n = 0.002
FEATURE [App::DocumentObjectGroupPython] Cl_element024  label="Cl_element : 0.002"  # scripted group (container) (typed FeaturePython)
  n = 0.002
FEATURE [App::DocumentObjectGroupPython] K_element011  label="K_element : 0.017"  # scripted group (container) (typed FeaturePython)
  n = 0.002
FEATURE [App::DocumentObjectGroupPython] G4_TESTIS_ICRP  # scripted group (container) (typed FeaturePython)
  Dunit = g/cm3
  Dvalue = 1.04
  Group = -> [H_element099,C_element108,N_element041,O_element093,Na_element018,P_element010,S_element021,Cl_element024,K_element011]
  conduct = 2
  density = 1
  expand = 3
  formula = G4_TESTIS_ICRP
  name = G4_TESTIS_ICRP
  specific = 4
FEATURE [App::DocumentObjectGroupPython] C_element109  label="C_element : 060"  # scripted group (container) (typed FeaturePython)
  n = 2
  ref = C_element
FEATURE [App::DocumentObjectGroupPython] Cl_element025  label="Cl_element : 012"  # scripted group (container) (typed FeaturePython)
  n = 4
  ref = Cl_element
FEATURE [App::DocumentObjectGroupPython] G4_TETRACHLOROETHYLENE  # scripted group (container) (typed FeaturePython)
  Dunit = g/cm3
  Dvalue = 1.625
  Group = -> [C_element109,Cl_element025]
  conduct = 2
  density = 1
  expand = 3
  formula = G4_TETRACHLOROETHYLENE
  name = G4_TETRACHLOROETHYLENE
  specific = 4
FEATURE [App::DocumentObjectGroupPython] Tl_element001  label="Tl_element : 1"  # scripted group (container) (typed FeaturePython)
  n = 1
  ref = Tl_element
FEATURE [App::DocumentObjectGroupPython] Cl_element026  label="Cl_element : 013"  # scripted group (container) (typed FeaturePython)
  n = 1
  ref = Cl_element
FEATURE [App::DocumentObjectGroupPython] G4_THALLIUM_CHLORIDE  # scripted group (container) (typed FeaturePython)
  Dunit = g/cm3
  Dvalue = 7.004
  Group = -> [Tl_element001,Cl_element026]
  conduct = 2
  density = 1
  expand = 3
  formula = G4_THALLIUM_CHLORIDE
  name = G4_THALLIUM_CHLORIDE
  specific = 4
FEATURE [App::DocumentObjectGroupPython] H_element100  label="H_element : 0.147"  # scripted group (container) (typed FeaturePython)
  n = 0.105
FEATURE [App::DocumentObjectGroupPython] C_element110  label="C_element : 0.256"  # scripted group (container) (typed FeaturePython)
  n = 0.256
FEATURE [App::DocumentObjectGroupPython] N_element042  label="N_element : 0.760"  # scripted group (container) (typed FeaturePython)
  n = 0.027
FEATURE [App::DocumentObjectGroupPython] O_element094  label="O_element : 0.602"  # scripted group (container) (typed FeaturePython)
  n = 0.602
FEATURE [App::DocumentObjectGroupPython] Na_element019  label="Na_element : 0.102"  # scripted group (container) (typed FeaturePython)
  n = 0.001
FEATURE [App::DocumentObjectGroupPython] P_element011  label="P_element : 0.109"  # scripted group (container) (typed FeaturePython)
  n = 0.002
FEATURE [App::DocumentObjectGroupPython] S_element022  label="S_element : 0.023"  # scripted group (container) (typed FeaturePython)
  n = 0.003
FEATURE [App::DocumentObjectGroupPython] Cl_element027  label="Cl_element : 0.591"  # scripted group (container) (typed FeaturePython)
  n = 0.002
FEATURE [App::DocumentObjectGroupPython] K_element012  label="K_element : 0.018"  # scripted group (container) (typed FeaturePython)
  n = 0.002
FEATURE [App::DocumentObjectGroupPython] G4_TISSUE_SOFT_ICRP  # scripted group (container) (typed FeaturePython)
  Dunit = g/cm3
  Dvalue = 1.03
  Group = -> [H_element100,C_element110,N_element042,O_element094,Na_element019,P_element011,S_element022,Cl_element027,K_element012]
  conduct = 2
  density = 1
  expand = 3
  formula = G4_TISSUE_SOFT_ICRP
  name = G4_TISSUE_SOFT_ICRP
  specific = 4
FEATURE [App::DocumentObjectGroupPython] H_element101  label="H_element : 0.148"  # scripted group (container) (typed FeaturePython)
  n = 0.101
FEATURE [App::DocumentObjectGroupPython] C_element111  label="C_element : 0.111"  # scripted group (container) (typed FeaturePython)
  n = 0.111
FEATURE [App::DocumentObjectGroupPython] N_element043  label="N_element : 0.026"  # scripted group (container) (typed FeaturePython)
  n = 0.026
FEATURE [App::DocumentObjectGroupPython] O_element095  label="O_element : 0.762"  # scripted group (container) (typed FeaturePython)
  n = 0.762
FEATURE [App::DocumentObjectGroupPython] G4_TISSUE_SOFT_ICRU_4  label="G4_TISSUE_SOFT_ICRU-4"  # scripted group (container) (typed FeaturePython)
  Dunit = g/cm3
  Dvalue = 1
  Group = -> [H_element101,C_element111,N_element043,O_element095]
  conduct = 2
  density = 1
  expand = 3
  formula = G4_TISSUE_SOFT_ICRU-4
  name = G4_TISSUE_SOFT_ICRU-4
  specific = 4
FEATURE [App::DocumentObjectGroupPython] H_element102  label="H_element : 0.149"  # scripted group (container) (typed FeaturePython)
  n = 0.101869
FEATURE [App::DocumentObjectGroupPython] C_element112  label="C_element : 0.456"  # scripted group (container) (typed FeaturePython)
  n = 0.456179
FEATURE [App::DocumentObjectGroupPython] N_element044  label="N_element : 0.761"  # scripted group (container) (typed FeaturePython)
  n = 0.035172
FEATURE [App::DocumentObjectGroupPython] O_element096  label="O_element : 0.407"  # scripted group (container) (typed FeaturePython)
  n = 0.40678
FEATURE [App::DocumentObjectGroupPython] G4_TISSUE_METHANE  label="G4_TISSUE-METHANE"  # scripted group (container) (typed FeaturePython)
  Dunit = g/cm3
  Dvalue = 0.00106409
  Group = -> [H_element102,C_element112,N_element044,O_element096]
  conduct = 2
  density = 1
  expand = 3
  formula = G4_TISSUE-METHANE
  name = G4_TISSUE-METHANE
  specific = 4
FEATURE [App::DocumentObjectGroupPython] H_element103  label="H_element : 0.103"  # scripted group (container) (typed FeaturePython)
  n = 0.102672
FEATURE [App::DocumentObjectGroupPython] C_element113  label="C_element : 0.569"  # scripted group (container) (typed FeaturePython)
  n = 0.56894
FEATURE [App::DocumentObjectGroupPython] N_element045  label="N_element : 0.762"  # scripted group (container) (typed FeaturePython)
  n = 0.035022
FEATURE [App::DocumentObjectGroupPython] O_element097  label="O_element : 0.293"  # scripted group (container) (typed FeaturePython)
  n = 0.293366
FEATURE [App::DocumentObjectGroupPython] G4_TISSUE_PROPANE  label="G4_TISSUE-PROPANE"  # scripted group (container) (typed FeaturePython)
  Dunit = g/cm3
  Dvalue = 0.00182628
  Group = -> [H_element103,C_element113,N_element045,O_element097]
  conduct = 2
  density = 1
  expand = 3
  formula = G4_TISSUE-PROPANE
  name = G4_TISSUE-PROPANE
  specific = 4
FEATURE [App::DocumentObjectGroupPython] Ti_element003  label="Ti_element : 1"  # scripted group (container) (typed FeaturePython)
  n = 1
  ref = Ti_element
FEATURE [App::DocumentObjectGroupPython] O_element098  label="O_element : 052"  # scripted group (container) (typed FeaturePython)
  n = 2
  ref = O_element
FEATURE [App::DocumentObjectGroupPython] G4_TITANIUM_DIOXIDE  # scripted group (container) (typed FeaturePython)
  Dunit = g/cm3
  Dvalue = 4.26
  Group = -> [Ti_element003,O_element098]
  conduct = 2
  density = 1
  expand = 3
  formula = G4_TITANIUM_DIOXIDE
  name = G4_TITANIUM_DIOXIDE
  specific = 4
FEATURE [App::DocumentObjectGroupPython] C_element114  label="C_element : 061"  # scripted group (container) (typed FeaturePython)
  n = 7
  ref = C_element
FEATURE [App::DocumentObjectGroupPython] H_element104  label="H_element : 055"  # scripted group (container) (typed FeaturePython)
  n = 8
  ref = H_element
FEATURE [App::DocumentObjectGroupPython] G4_TOLUENE  # scripted group (container) (typed FeaturePython)
  Dunit = g/cm3
  Dvalue = 0.8669
  Group = -> [C_element114,H_element104]
  conduct = 2
  density = 1
  expand = 3
  formula = G4_TOLUENE
  name = G4_TOLUENE
  specific = 4
FEATURE [App::DocumentObjectGroupPython] C_element115  label="C_element : 062"  # scripted group (container) (typed FeaturePython)
  n = 2
  ref = C_element
FEATURE [App::DocumentObjectGroupPython] H_element105  label="H_element : 056"  # scripted group (container) (typed FeaturePython)
  n = 1
  ref = H_element
FEATURE [App::DocumentObjectGroupPython] Cl_element028  label="Cl_element : 014"  # scripted group (container) (typed FeaturePython)
  n = 3
  ref = Cl_element
FEATURE [App::DocumentObjectGroupPython] G4_TRICHLOROETHYLENE  # scripted group (container) (typed FeaturePython)
  Dunit = g/cm3
  Dvalue = 1.46
  Group = -> [C_element115,H_element105,Cl_element028]
  conduct = 2
  density = 1
  expand = 3
  formula = G4_TRICHLOROETHYLENE
  name = G4_TRICHLOROETHYLENE
  specific = 4
FEATURE [App::DocumentObjectGroupPython] C_element116  label="C_element : 063"  # scripted group (container) (typed FeaturePython)
  n = 6
  ref = C_element
FEATURE [App::DocumentObjectGroupPython] H_element106  label="H_element : 15"  # scripted group (container) (typed FeaturePython)
  n = 15
  ref = H_element
FEATURE [App::DocumentObjectGroupPython] O_element099  label="O_element : 053"  # scripted group (container) (typed FeaturePython)
  n = 4
  ref = O_element
FEATURE [App::DocumentObjectGroupPython] P_element012  label="P_element : 1"  # scripted group (container) (typed FeaturePython)
  n = 1
  ref = P_element
FEATURE [App::DocumentObjectGroupPython] G4_TRIETHYL_PHOSPHATE  # scripted group (container) (typed FeaturePython)
  Dunit = g/cm3
  Dvalue = 1.07
  Group = -> [C_element116,H_element106,O_element099,P_element012]
  conduct = 2
  density = 1
  expand = 3
  formula = G4_TRIETHYL_PHOSPHATE
  name = G4_TRIETHYL_PHOSPHATE
  specific = 4
FEATURE [App::DocumentObjectGroupPython] W_element003  label="W_element : 003"  # scripted group (container) (typed FeaturePython)
  n = 1
  ref = W_element
FEATURE [App::DocumentObjectGroupPython] F_element017  label="F_element : 6"  # scripted group (container) (typed FeaturePython)
  n = 6
  ref = F_element
FEATURE [App::DocumentObjectGroupPython] G4_TUNGSTEN_HEXAFLUORIDE  # scripted group (container) (typed FeaturePython)
  Dunit = g/cm3
  Dvalue = 2.4
  Group = -> [W_element003,F_element017]
  conduct = 2
  density = 1
  expand = 3
  formula = G4_TUNGSTEN_HEXAFLUORIDE
  name = G4_TUNGSTEN_HEXAFLUORIDE
  specific = 4
FEATURE [App::DocumentObjectGroupPython] U_element001  label="U_element : 1"  # scripted group (container) (typed FeaturePython)
  n = 1
  ref = U_element
FEATURE [App::DocumentObjectGroupPython] C_element117  label="C_element : 064"  # scripted group (container) (typed FeaturePython)
  n = 2
  ref = C_element
FEATURE [App::DocumentObjectGroupPython] G4_URANIUM_DICARBIDE  # scripted group (container) (typed FeaturePython)
  Dunit = g/cm3
  Dvalue = 11.28
  Group = -> [U_element001,C_element117]
  conduct = 2
  density = 1
  expand = 3
  formula = G4_URANIUM_DICARBIDE
  name = G4_URANIUM_DICARBIDE
  specific = 4
FEATURE [App::DocumentObjectGroupPython] U_element002  label="U_element : 002"  # scripted group (container) (typed FeaturePython)
  n = 1
  ref = U_element
FEATURE [App::DocumentObjectGroupPython] C_element118  label="C_element : 065"  # scripted group (container) (typed FeaturePython)
  n = 1
  ref = C_element
FEATURE [App::DocumentObjectGroupPython] G4_URANIUM_MONOCARBIDE  # scripted group (container) (typed FeaturePython)
  Dunit = g/cm3
  Dvalue = 13.63
  Group = -> [U_element002,C_element118]
  conduct = 2
  density = 1
  expand = 3
  formula = G4_URANIUM_MONOCARBIDE
  name = G4_URANIUM_MONOCARBIDE
  specific = 4
FEATURE [App::DocumentObjectGroupPython] U_element003  label="U_element : 003"  # scripted group (container) (typed FeaturePython)
  n = 1
  ref = U_element
FEATURE [App::DocumentObjectGroupPython] O_element100  label="O_element : 054"  # scripted group (container) (typed FeaturePython)
  n = 2
  ref = O_element
FEATURE [App::DocumentObjectGroupPython] G4_URANIUM_OXIDE  # scripted group (container) (typed FeaturePython)
  Dunit = g/cm3
  Dvalue = 10.96
  Group = -> [U_element003,O_element100]
  conduct = 2
  density = 1
  expand = 3
  formula = G4_URANIUM_OXIDE
  name = G4_URANIUM_OXIDE
  specific = 4
FEATURE [App::DocumentObjectGroupPython] C_element119  label="C_element : 066"  # scripted group (container) (typed FeaturePython)
  n = 1
  ref = C_element
FEATURE [App::DocumentObjectGroupPython] H_element107  label="H_element : 057"  # scripted group (container) (typed FeaturePython)
  n = 4
  ref = H_element
FEATURE [App::DocumentObjectGroupPython] N_element046  label="N_element : 019"  # scripted group (container) (typed FeaturePython)
  n = 2
  ref = N_element
FEATURE [App::DocumentObjectGroupPython] O_element101  label="O_element : 055"  # scripted group (container) (typed FeaturePython)
  n = 1
  ref = O_element
FEATURE [App::DocumentObjectGroupPython] G4_UREA  # scripted group (container) (typed FeaturePython)
  Dunit = g/cm3
  Dvalue = 1.323
  Group = -> [C_element119,H_element107,N_element046,O_element101]
  conduct = 2
  density = 1
  expand = 3
  formula = G4_UREA
  name = G4_UREA
  specific = 4
FEATURE [App::DocumentObjectGroupPython] C_element120  label="C_element : 067"  # scripted group (container) (typed FeaturePython)
  n = 5
  ref = C_element
FEATURE [App::DocumentObjectGroupPython] H_element108  label="H_element : 058"  # scripted group (container) (typed FeaturePython)
  n = 11
  ref = H_element
FEATURE [App::DocumentObjectGroupPython] N_element047  label="N_element : 020"  # scripted group (container) (typed FeaturePython)
  n = 1
  ref = N_element
FEATURE [App::DocumentObjectGroupPython] O_element102  label="O_element : 056"  # scripted group (container) (typed FeaturePython)
  n = 2
  ref = O_element
FEATURE [App::DocumentObjectGroupPython] G4_VALINE  # scripted group (container) (typed FeaturePython)
  Dunit = g/cm3
  Dvalue = 1.23
  Group = -> [C_element120,H_element108,N_element047,O_element102]
  conduct = 2
  density = 1
  expand = 3
  formula = G4_VALINE
  name = G4_VALINE
  specific = 4
FEATURE [App::DocumentObjectGroupPython] H_element109  label="H_element : 0.009"  # scripted group (container) (typed FeaturePython)
  n = 0.009417
FEATURE [App::DocumentObjectGroupPython] C_element121  label="C_element : 0.281"  # scripted group (container) (typed FeaturePython)
  n = 0.280555
FEATURE [App::DocumentObjectGroupPython] F_element018  label="F_element : 0.710"  # scripted group (container) (typed FeaturePython)
  n = 0.710028
FEATURE [App::DocumentObjectGroupPython] G4_VITON  # scripted group (container) (typed FeaturePython)
  Dunit = g/cm3
  Dvalue = 1.8
  Group = -> [H_element109,C_element121,F_element018]
  conduct = 2
  density = 1
  expand = 3
  formula = G4_VITON
  name = G4_VITON
  specific = 4
FEATURE [App::DocumentObjectGroupPython] H_element110  label="H_element : 059"  # scripted group (container) (typed FeaturePython)
  n = 2
  ref = H_element
FEATURE [App::DocumentObjectGroupPython] O_element103  label="O_element : 057"  # scripted group (container) (typed FeaturePython)
  n = 1
  ref = O_element
FEATURE [App::DocumentObjectGroupPython] G4_WATER  # scripted group (container) (typed FeaturePython)
  Dunit = g/cm3
  Dvalue = 1
  Group = -> [H_element110,O_element103]
  conduct = 2
  density = 1
  expand = 3
  formula = G4_WATER
  name = G4_WATER
  specific = 4
FEATURE [App::DocumentObjectGroupPython] H_element111  label="H_element : 060"  # scripted group (container) (typed FeaturePython)
  n = 2
  ref = H_element
FEATURE [App::DocumentObjectGroupPython] O_element104  label="O_element : 058"  # scripted group (container) (typed FeaturePython)
  n = 1
  ref = O_element
FEATURE [App::DocumentObjectGroupPython] G4_WATER_VAPOR  # scripted group (container) (typed FeaturePython)
  Dunit = g/cm3
  Dvalue = 0.000756182
  Group = -> [H_element111,O_element104]
  conduct = 2
  density = 1
  expand = 3
  formula = G4_WATER_VAPOR
  name = G4_WATER_VAPOR
  specific = 4
FEATURE [App::DocumentObjectGroupPython] C_element122  label="C_element : 068"  # scripted group (container) (typed FeaturePython)
  n = 8
  ref = C_element
FEATURE [App::DocumentObjectGroupPython] H_element112  label="H_element : 061"  # scripted group (container) (typed FeaturePython)
  n = 10
  ref = H_element
FEATURE [App::DocumentObjectGroupPython] G4_XYLENE  # scripted group (container) (typed FeaturePython)
  Dunit = g/cm3
  Dvalue = 0.87
  Group = -> [C_element122,H_element112]
  conduct = 2
  density = 1
  expand = 3
  formula = G4_XYLENE
  name = G4_XYLENE
  specific = 4
FEATURE [App::DocumentObjectGroupPython] C_element123  label="C_element : 069"  # scripted group (container) (typed FeaturePython)
  n = 1
  ref = C_element
FEATURE [App::DocumentObjectGroupPython] G4_GRAPHITE  # scripted group (container) (typed FeaturePython)
  Dunit = g/cm3
  Dvalue = 2.21
  Group = -> [C_element123]
  conduct = 2
  density = 1
  expand = 3
  formula = G4_GRAPHITE
  name = G4_GRAPHITE
  specific = 4
FEATURE [App::DocumentObjectGroupPython] NIST  # scripted group (container) (typed FeaturePython)
  Group = -> [G4_A_150_TISSUE,G4_ACETONE,G4_ACETYLENE,G4_ADENINE,G4_ADIPOSE_TISSUE_ICRP,G4_AIR,G4_ALANINE,G4_ALUMINUM_OXIDE,G4_AMBER,G4_AMMONIA,G4_ANILINE,G4_ANTHRACENE,G4_B_100_BONE,G4_BAKELITE,G4_BARIUM_FLUORIDE,G4_BARIUM_SULFATE,G4_BENZENE,G4_BERYLLIUM_OXIDE,G4_BGO,G4_BLOOD_ICRP,G4_BONE_COMPACT_ICRU,G4_BONE_CORTICAL_ICRP,G4_BORON_CARBIDE,G4_BORON_OXIDE,G4_BRAIN_ICRP,G4_BUTANE,G4_N_BUTYL_ALCOHOL,G4_C_552,+152 more]
FEATURE [App::DocumentObjectGroupPython] H_element113  label="H_element : 062"  # scripted group (container) (typed FeaturePython)
  n = 1
  ref = H_element
FEATURE [App::DocumentObjectGroupPython] G4_H  # scripted group (container) (typed FeaturePython)
  Dunit = g/cm3
  Dvalue = 8.3748e-05
  Group = -> [H_element113]
  conduct = 2
  density = 1
  expand = 3
  formula = H
  name = G4_H
  specific = 4
FEATURE [App::DocumentObjectGroupPython] He_element001  label="He_element : 1"  # scripted group (container) (typed FeaturePython)
  n = 1
  ref = He_element
FEATURE [App::DocumentObjectGroupPython] G4_He  # scripted group (container) (typed FeaturePython)
  Dunit = g/cm3
  Dvalue = 0.000166322
  Group = -> [He_element001]
  conduct = 2
  density = 1
  expand = 3
  formula = He
  name = G4_He
  specific = 4
FEATURE [App::DocumentObjectGroupPython] Li_element008  label="Li_element : 008"  # scripted group (container) (typed FeaturePython)
  n = 1
  ref = Li_element
FEATURE [App::DocumentObjectGroupPython] G4_Li  # scripted group (container) (typed FeaturePython)
  Dunit = g/cm3
  Dvalue = 0.534
  Group = -> [Li_element008]
  conduct = 2
  density = 1
  expand = 3
  formula = Li
  name = G4_Li
  specific = 4
FEATURE [App::DocumentObjectGroupPython] Be_element002  label="Be_element : 002"  # scripted group (container) (typed FeaturePython)
  n = 1
  ref = Be_element
FEATURE [App::DocumentObjectGroupPython] G4_Be  # scripted group (container) (typed FeaturePython)
  Dunit = g/cm3
  Dvalue = 1.848
  Group = -> [Be_element002]
  conduct = 2
  density = 1
  expand = 3
  formula = Be
  name = G4_Be
  specific = 4
FEATURE [App::DocumentObjectGroupPython] B_element007  label="B_element : 007"  # scripted group (container) (typed FeaturePython)
  n = 1
  ref = B_element
FEATURE [App::DocumentObjectGroupPython] G4_B  # scripted group (container) (typed FeaturePython)
  Dunit = g/cm3
  Dvalue = 2.37
  Group = -> [B_element007]
  conduct = 2
  density = 1
  expand = 3
  formula = B
  name = G4_B
  specific = 4
FEATURE [App::DocumentObjectGroupPython] C_element124  label="C_element : 070"  # scripted group (container) (typed FeaturePython)
  n = 1
  ref = C_element
FEATURE [App::DocumentObjectGroupPython] G4_C  # scripted group (container) (typed FeaturePython)
  Dunit = g/cm3
  Dvalue = 2
  Group = -> [C_element124]
  conduct = 2
  density = 1
  expand = 3
  formula = C
  name = G4_C
  specific = 4
FEATURE [App::DocumentObjectGroupPython] N_element048  label="N_element : 021"  # scripted group (container) (typed FeaturePython)
  n = 1
  ref = N_element
FEATURE [App::DocumentObjectGroupPython] G4_N  # scripted group (container) (typed FeaturePython)
  Dunit = g/cm3
  Dvalue = 0.0011652
  Group = -> [N_element048]
  conduct = 2
  density = 1
  expand = 3
  formula = N
  name = G4_N
  specific = 4
FEATURE [App::DocumentObjectGroupPython] O_element105  label="O_element : 059"  # scripted group (container) (typed FeaturePython)
  n = 1
  ref = O_element
FEATURE [App::DocumentObjectGroupPython] G4_O  # scripted group (container) (typed FeaturePython)
  Dunit = g/cm3
  Dvalue = 0.00133151
  Group = -> [O_element105]
  conduct = 2
  density = 1
  expand = 3
  formula = O
  name = G4_O
  specific = 4
FEATURE [App::DocumentObjectGroupPython] F_element019  label="F_element : 008"  # scripted group (container) (typed FeaturePython)
  n = 1
  ref = F_element
FEATURE [App::DocumentObjectGroupPython] G4_F  # scripted group (container) (typed FeaturePython)
  Dunit = g/cm3
  Dvalue = 0.00158029
  Group = -> [F_element019]
  conduct = 2
  density = 1
  expand = 3
  formula = F
  name = G4_F
  specific = 4
FEATURE [App::DocumentObjectGroupPython] Ne_element001  label="Ne_element : 1"  # scripted group (container) (typed FeaturePython)
  n = 1
  ref = Ne_element
FEATURE [App::DocumentObjectGroupPython] G4_Ne  # scripted group (container) (typed FeaturePython)
  Dunit = g/cm3
  Dvalue = 0.000838505
  Group = -> [Ne_element001]
  conduct = 2
  density = 1
  expand = 3
  formula = Ne
  name = G4_Ne
  specific = 4
FEATURE [App::DocumentObjectGroupPython] Na_element020  label="Na_element : 005"  # scripted group (container) (typed FeaturePython)
  n = 1
  ref = Na_element
FEATURE [App::DocumentObjectGroupPython] G4_Na  # scripted group (container) (typed FeaturePython)
  Dunit = g/cm3
  Dvalue = 0.971
  Group = -> [Na_element020]
  conduct = 2
  density = 1
  expand = 3
  formula = Na
  name = G4_Na
  specific = 4
FEATURE [App::DocumentObjectGroupPython] Mg_element011  label="Mg_element : 005"  # scripted group (container) (typed FeaturePython)
  n = 1
  ref = Mg_element
FEATURE [App::DocumentObjectGroupPython] G4_Mg  # scripted group (container) (typed FeaturePython)
  Dunit = g/cm3
  Dvalue = 1.74
  Group = -> [Mg_element011]
  conduct = 2
  density = 1
  expand = 3
  formula = Mg
  name = G4_Mg
  specific = 4
FEATURE [App::DocumentObjectGroupPython] Al_element004  label="Al_element : 1"  # scripted group (container) (typed FeaturePython)
  n = 1
  ref = Al_element
FEATURE [App::DocumentObjectGroupPython] G4_Al  # scripted group (container) (typed FeaturePython)
  Dunit = g/cm3
  Dvalue = 2.699
  Group = -> [Al_element004]
  conduct = 2
  density = 1
  expand = 3
  formula = Al
  name = G4_Al
  specific = 4
FEATURE [App::DocumentObjectGroupPython] Si_element007  label="Si_element : 002"  # scripted group (container) (typed FeaturePython)
  n = 1
  ref = Si_element
FEATURE [App::DocumentObjectGroupPython] G4_Si  # scripted group (container) (typed FeaturePython)
  Dunit = g/cm3
  Dvalue = 2.33
  Group = -> [Si_element007]
  conduct = 2
  density = 1
  expand = 3
  formula = Si
  name = G4_Si
  specific = 4
FEATURE [App::DocumentObjectGroupPython] P_element013  label="P_element : 002"  # scripted group (container) (typed FeaturePython)
  n = 1
  ref = P_element
FEATURE [App::DocumentObjectGroupPython] G4_P  # scripted group (container) (typed FeaturePython)
  Dunit = g/cm3
  Dvalue = 2.2
  Group = -> [P_element013]
  conduct = 2
  density = 1
  expand = 3
  formula = P
  name = G4_P
  specific = 4
FEATURE [App::DocumentObjectGroupPython] S_element023  label="S_element : 007"  # scripted group (container) (typed FeaturePython)
  n = 1
  ref = S_element
FEATURE [App::DocumentObjectGroupPython] G4_S  # scripted group (container) (typed FeaturePython)
  Dunit = g/cm3
  Dvalue = 2
  Group = -> [S_element023]
  conduct = 2
  density = 1
  expand = 3
  formula = S
  name = G4_S
  specific = 4
FEATURE [App::DocumentObjectGroupPython] Cl_element029  label="Cl_element : 015"  # scripted group (container) (typed FeaturePython)
  n = 1
  ref = Cl_element
FEATURE [App::DocumentObjectGroupPython] G4_Cl  # scripted group (container) (typed FeaturePython)
  Dunit = g/cm3
  Dvalue = 0.00299473
  Group = -> [Cl_element029]
  conduct = 2
  density = 1
  expand = 3
  formula = Cl
  name = G4_Cl
  specific = 4
FEATURE [App::DocumentObjectGroupPython] Ar_element002  label="Ar_element : 1"  # scripted group (container) (typed FeaturePython)
  n = 1
  ref = Ar_element
FEATURE [App::DocumentObjectGroupPython] G4_Ar  # scripted group (container) (typed FeaturePython)
  Dunit = g/cm3
  Dvalue = 0.00166201
  Group = -> [Ar_element002]
  conduct = 2
  density = 1
  expand = 3
  formula = Ar
  name = G4_Ar
  specific = 4
FEATURE [App::DocumentObjectGroupPython] K_element013  label="K_element : 003"  # scripted group (container) (typed FeaturePython)
  n = 1
  ref = K_element
FEATURE [App::DocumentObjectGroupPython] G4_K  # scripted group (container) (typed FeaturePython)
  Dunit = g/cm3
  Dvalue = 0.862
  Group = -> [K_element013]
  conduct = 2
  density = 1
  expand = 3
  formula = K
  name = G4_K
  specific = 4
FEATURE [App::DocumentObjectGroupPython] Ca_element014  label="Ca_element : 007"  # scripted group (container) (typed FeaturePython)
  n = 1
  ref = Ca_element
FEATURE [App::DocumentObjectGroupPython] G4_Ca  # scripted group (container) (typed FeaturePython)
  Dunit = g/cm3
  Dvalue = 1.55
  Group = -> [Ca_element014]
  conduct = 2
  density = 1
  expand = 3
  formula = Ca
  name = G4_Ca
  specific = 4
FEATURE [App::DocumentObjectGroupPython] Sc_element001  label="Sc_element : 1"  # scripted group (container) (typed FeaturePython)
  n = 1
  ref = Sc_element
FEATURE [App::DocumentObjectGroupPython] G4_Sc  # scripted group (container) (typed FeaturePython)
  Dunit = g/cm3
  Dvalue = 2.989
  Group = -> [Sc_element001]
  conduct = 2
  density = 1
  expand = 3
  formula = Sc
  name = G4_Sc
  specific = 4
FEATURE [App::DocumentObjectGroupPython] Ti_element004  label="Ti_element : 002"  # scripted group (container) (typed FeaturePython)
  n = 1
  ref = Ti_element
FEATURE [App::DocumentObjectGroupPython] G4_Ti  # scripted group (container) (typed FeaturePython)
  Dunit = g/cm3
  Dvalue = 4.54
  Group = -> [Ti_element004]
  conduct = 2
  density = 1
  expand = 3
  formula = Ti
  name = G4_Ti
  specific = 4
FEATURE [App::DocumentObjectGroupPython] V_element001  label="V_element : 1"  # scripted group (container) (typed FeaturePython)
  n = 1
  ref = V_element
FEATURE [App::DocumentObjectGroupPython] G4_V  # scripted group (container) (typed FeaturePython)
  Dunit = g/cm3
  Dvalue = 6.11
  Group = -> [V_element001]
  conduct = 2
  density = 1
  expand = 3
  formula = V
  name = G4_V
  specific = 4
FEATURE [App::DocumentObjectGroupPython] Cr_element001  label="Cr_element : 1"  # scripted group (container) (typed FeaturePython)
  n = 1
  ref = Cr_element
FEATURE [App::DocumentObjectGroupPython] G4_Cr  # scripted group (container) (typed FeaturePython)
  Dunit = g/cm3
  Dvalue = 7.18
  Group = -> [Cr_element001]
  conduct = 2
  density = 1
  expand = 3
  formula = Cr
  name = G4_Cr
  specific = 4
FEATURE [App::DocumentObjectGroupPython] Mn_element001  label="Mn_element : 1"  # scripted group (container) (typed FeaturePython)
  n = 1
  ref = Mn_element
FEATURE [App::DocumentObjectGroupPython] G4_Mn  # scripted group (container) (typed FeaturePython)
  Dunit = g/cm3
  Dvalue = 7.44
  Group = -> [Mn_element001]
  conduct = 2
  density = 1
  expand = 3
  formula = Mn
  name = G4_Mn
  specific = 4
FEATURE [App::DocumentObjectGroupPython] Fe_element007  label="Fe_element : 004"  # scripted group (container) (typed FeaturePython)
  n = 1
  ref = Fe_element
FEATURE [App::DocumentObjectGroupPython] G4_Fe  # scripted group (container) (typed FeaturePython)
  Dunit = g/cm3
  Dvalue = 7.874
  Group = -> [Fe_element007]
  conduct = 2
  density = 1
  expand = 3
  formula = Fe
  name = G4_Fe
  specific = 4
FEATURE [App::DocumentObjectGroupPython] Co_element001  label="Co_element : 1"  # scripted group (container) (typed FeaturePython)
  n = 1
  ref = Co_element
FEATURE [App::DocumentObjectGroupPython] G4_Co  # scripted group (container) (typed FeaturePython)
  Dunit = g/cm3
  Dvalue = 8.9
  Group = -> [Co_element001]
  conduct = 2
  density = 1
  expand = 3
  formula = Co
  name = G4_Co
  specific = 4
FEATURE [App::DocumentObjectGroupPython] Ni_element001  label="Ni_element : 1"  # scripted group (container) (typed FeaturePython)
  n = 1
  ref = Ni_element
FEATURE [App::DocumentObjectGroupPython] G4_Ni  # scripted group (container) (typed FeaturePython)
  Dunit = g/cm3
  Dvalue = 8.902
  Group = -> [Ni_element001]
  conduct = 2
  density = 1
  expand = 3
  formula = Ni
  name = G4_Ni
  specific = 4
FEATURE [App::DocumentObjectGroupPython] Cu_element001  label="Cu_element : 1"  # scripted group (container) (typed FeaturePython)
  n = 1
  ref = Cu_element
FEATURE [App::DocumentObjectGroupPython] G4_Cu  # scripted group (container) (typed FeaturePython)
  Dunit = g/cm3
  Dvalue = 8.96
  Group = -> [Cu_element001]
  conduct = 2
  density = 1
  expand = 3
  formula = Cu
  name = G4_Cu
  specific = 4
FEATURE [App::DocumentObjectGroupPython] Zn_element001  label="Zn_element : 1"  # scripted group (container) (typed FeaturePython)
  n = 1
  ref = Zn_element
FEATURE [App::DocumentObjectGroupPython] G4_Zn  # scripted group (container) (typed FeaturePython)
  Dunit = g/cm3
  Dvalue = 7.133
  Group = -> [Zn_element001]
  conduct = 2
  density = 1
  expand = 3
  formula = Zn
  name = G4_Zn
  specific = 4
FEATURE [App::DocumentObjectGroupPython] Ga_element002  label="Ga_element : 002"  # scripted group (container) (typed FeaturePython)
  n = 1
  ref = Ga_element
FEATURE [App::DocumentObjectGroupPython] G4_Ga  # scripted group (container) (typed FeaturePython)
  Dunit = g/cm3
  Dvalue = 5.904
  Group = -> [Ga_element002]
  conduct = 2
  density = 1
  expand = 3
  formula = Ga
  name = G4_Ga
  specific = 4
FEATURE [App::DocumentObjectGroupPython] Ge_element002  label="Ge_element : 1"  # scripted group (container) (typed FeaturePython)
  n = 1
  ref = Ge_element
FEATURE [App::DocumentObjectGroupPython] G4_Ge  # scripted group (container) (typed FeaturePython)
  Dunit = g/cm3
  Dvalue = 5.323
  Group = -> [Ge_element002]
  conduct = 2
  density = 1
  expand = 3
  formula = Ge
  name = G4_Ge
  specific = 4
FEATURE [App::DocumentObjectGroupPython] As_element003  label="As_element : 002"  # scripted group (container) (typed FeaturePython)
  n = 1
  ref = As_element
FEATURE [App::DocumentObjectGroupPython] G4_As  # scripted group (container) (typed FeaturePython)
  Dunit = g/cm3
  Dvalue = 5.73
  Group = -> [As_element003]
  conduct = 2
  density = 1
  expand = 3
  formula = As
  name = G4_As
  specific = 4
FEATURE [App::DocumentObjectGroupPython] Se_element001  label="Se_element : 1"  # scripted group (container) (typed FeaturePython)
  n = 1
  ref = Se_element
FEATURE [App::DocumentObjectGroupPython] G4_Se  # scripted group (container) (typed FeaturePython)
  Dunit = g/cm3
  Dvalue = 4.5
  Group = -> [Se_element001]
  conduct = 2
  density = 1
  expand = 3
  formula = Se
  name = G4_Se
  specific = 4
FEATURE [App::DocumentObjectGroupPython] Br_element007  label="Br_element : 004"  # scripted group (container) (typed FeaturePython)
  n = 1
  ref = Br_element
FEATURE [App::DocumentObjectGroupPython] G4_Br  # scripted group (container) (typed FeaturePython)
  Dunit = g/cm3
  Dvalue = 0.0070721
  Group = -> [Br_element007]
  conduct = 2
  density = 1
  expand = 3
  formula = Br
  name = G4_Br
  specific = 4
FEATURE [App::DocumentObjectGroupPython] Kr_element001  label="Kr_element : 1"  # scripted group (container) (typed FeaturePython)
  n = 1
  ref = Kr_element
FEATURE [App::DocumentObjectGroupPython] G4_Kr  # scripted group (container) (typed FeaturePython)
  Dunit = g/cm3
  Dvalue = 0.00347832
  Group = -> [Kr_element001]
  conduct = 2
  density = 1
  expand = 3
  formula = Kr
  name = G4_Kr
  specific = 4
FEATURE [App::DocumentObjectGroupPython] Rb_element001  label="Rb_element : 1"  # scripted group (container) (typed FeaturePython)
  n = 1
  ref = Rb_element
FEATURE [App::DocumentObjectGroupPython] G4_Rb  # scripted group (container) (typed FeaturePython)
  Dunit = g/cm3
  Dvalue = 1.532
  Group = -> [Rb_element001]
  conduct = 2
  density = 1
  expand = 3
  formula = Rb
  name = G4_Rb
  specific = 4
FEATURE [App::DocumentObjectGroupPython] Sr_element001  label="Sr_element : 1"  # scripted group (container) (typed FeaturePython)
  n = 1
  ref = Sr_element
FEATURE [App::DocumentObjectGroupPython] G4_Sr  # scripted group (container) (typed FeaturePython)
  Dunit = g/cm3
  Dvalue = 2.54
  Group = -> [Sr_element001]
  conduct = 2
  density = 1
  expand = 3
  formula = Sr
  name = G4_Sr
  specific = 4
FEATURE [App::DocumentObjectGroupPython] Y_element001  label="Y_element : 1"  # scripted group (container) (typed FeaturePython)
  n = 1
  ref = Y_element
FEATURE [App::DocumentObjectGroupPython] G4_Y  # scripted group (container) (typed FeaturePython)
  Dunit = g/cm3
  Dvalue = 4.469
  Group = -> [Y_element001]
  conduct = 2
  density = 1
  expand = 3
  formula = Y
  name = G4_Y
  specific = 4
FEATURE [App::DocumentObjectGroupPython] Zr_element001  label="Zr_element : 1"  # scripted group (container) (typed FeaturePython)
  n = 1
  ref = Zr_element
FEATURE [App::DocumentObjectGroupPython] G4_Zr  # scripted group (container) (typed FeaturePython)
  Dunit = g/cm3
  Dvalue = 6.506
  Group = -> [Zr_element001]
  conduct = 2
  density = 1
  expand = 3
  formula = Zr
  name = G4_Zr
  specific = 4
FEATURE [App::DocumentObjectGroupPython] Nb_element001  label="Nb_element : 1"  # scripted group (container) (typed FeaturePython)
  n = 1
  ref = Nb_element
FEATURE [App::DocumentObjectGroupPython] G4_Nb  # scripted group (container) (typed FeaturePython)
  Dunit = g/cm3
  Dvalue = 8.57
  Group = -> [Nb_element001]
  conduct = 2
  density = 1
  expand = 3
  formula = Nb
  name = G4_Nb
  specific = 4
FEATURE [App::DocumentObjectGroupPython] Mo_element001  label="Mo_element : 1"  # scripted group (container) (typed FeaturePython)
  n = 1
  ref = Mo_element
FEATURE [App::DocumentObjectGroupPython] G4_Mo  # scripted group (container) (typed FeaturePython)
  Dunit = g/cm3
  Dvalue = 10.22
  Group = -> [Mo_element001]
  conduct = 2
  density = 1
  expand = 3
  formula = Mo
  name = G4_Mo
  specific = 4
FEATURE [App::DocumentObjectGroupPython] Tc_element001  label="Tc_element : 1"  # scripted group (container) (typed FeaturePython)
  n = 1
  ref = Tc_element
FEATURE [App::DocumentObjectGroupPython] G4_Tc  # scripted group (container) (typed FeaturePython)
  Dunit = g/cm3
  Dvalue = 11.5
  Group = -> [Tc_element001]
  conduct = 2
  density = 1
  expand = 3
  formula = Tc
  name = G4_Tc
  specific = 4
FEATURE [App::DocumentObjectGroupPython] Ru_element001  label="Ru_element : 1"  # scripted group (container) (typed FeaturePython)
  n = 1
  ref = Ru_element
FEATURE [App::DocumentObjectGroupPython] G4_Ru  # scripted group (container) (typed FeaturePython)
  Dunit = g/cm3
  Dvalue = 12.41
  Group = -> [Ru_element001]
  conduct = 2
  density = 1
  expand = 3
  formula = Ru
  name = G4_Ru
  specific = 4
FEATURE [App::DocumentObjectGroupPython] Rh_element001  label="Rh_element : 1"  # scripted group (container) (typed FeaturePython)
  n = 1
  ref = Rh_element
FEATURE [App::DocumentObjectGroupPython] G4_Rh  # scripted group (container) (typed FeaturePython)
  Dunit = g/cm3
  Dvalue = 12.41
  Group = -> [Rh_element001]
  conduct = 2
  density = 1
  expand = 3
  formula = Rh
  name = G4_Rh
  specific = 4
FEATURE [App::DocumentObjectGroupPython] Pd_element001  label="Pd_element : 1"  # scripted group (container) (typed FeaturePython)
  n = 1
  ref = Pd_element
FEATURE [App::DocumentObjectGroupPython] G4_Pd  # scripted group (container) (typed FeaturePython)
  Dunit = g/cm3
  Dvalue = 12.02
  Group = -> [Pd_element001]
  conduct = 2
  density = 1
  expand = 3
  formula = Pd
  name = G4_Pd
  specific = 4
FEATURE [App::DocumentObjectGroupPython] Ag_element006  label="Ag_element : 004"  # scripted group (container) (typed FeaturePython)
  n = 1
  ref = Ag_element
FEATURE [App::DocumentObjectGroupPython] G4_Ag  # scripted group (container) (typed FeaturePython)
  Dunit = g/cm3
  Dvalue = 10.5
  Group = -> [Ag_element006]
  conduct = 2
  density = 1
  expand = 3
  formula = Ag
  name = G4_Ag
  specific = 4
FEATURE [App::DocumentObjectGroupPython] Cd_element003  label="Cd_element : 003"  # scripted group (container) (typed FeaturePython)
  n = 1
  ref = Cd_element
FEATURE [App::DocumentObjectGroupPython] G4_Cd  # scripted group (container) (typed FeaturePython)
  Dunit = g/cm3
  Dvalue = 8.65
  Group = -> [Cd_element003]
  conduct = 2
  density = 1
  expand = 3
  formula = Cd
  name = G4_Cd
  specific = 4
FEATURE [App::DocumentObjectGroupPython] In_element001  label="In_element : 1"  # scripted group (container) (typed FeaturePython)
  n = 1
  ref = In_element
FEATURE [App::DocumentObjectGroupPython] G4_In  # scripted group (container) (typed FeaturePython)
  Dunit = g/cm3
  Dvalue = 7.31
  Group = -> [In_element001]
  conduct = 2
  density = 1
  expand = 3
  formula = In
  name = G4_In
  specific = 4
FEATURE [App::DocumentObjectGroupPython] Sn_element001  label="Sn_element : 1"  # scripted group (container) (typed FeaturePython)
  n = 1
  ref = Sn_element
FEATURE [App::DocumentObjectGroupPython] G4_Sn  # scripted group (container) (typed FeaturePython)
  Dunit = g/cm3
  Dvalue = 7.31
  Group = -> [Sn_element001]
  conduct = 2
  density = 1
  expand = 3
  formula = Sn
  name = G4_Sn
  specific = 4
FEATURE [App::DocumentObjectGroupPython] Sb_element001  label="Sb_element : 1"  # scripted group (container) (typed FeaturePython)
  n = 1
  ref = Sb_element
FEATURE [App::DocumentObjectGroupPython] G4_Sb  # scripted group (container) (typed FeaturePython)
  Dunit = g/cm3
  Dvalue = 6.691
  Group = -> [Sb_element001]
  conduct = 2
  density = 1
  expand = 3
  formula = Sb
  name = G4_Sb
  specific = 4
FEATURE [App::DocumentObjectGroupPython] Te_element002  label="Te_element : 002"  # scripted group (container) (typed FeaturePython)
  n = 1
  ref = Te_element
FEATURE [App::DocumentObjectGroupPython] G4_Te  # scripted group (container) (typed FeaturePython)
  Dunit = g/cm3
  Dvalue = 6.24
  Group = -> [Te_element002]
  conduct = 2
  density = 1
  expand = 3
  formula = Te
  name = G4_Te
  specific = 4
FEATURE [App::DocumentObjectGroupPython] I_element010  label="I_element : 006"  # scripted group (container) (typed FeaturePython)
  n = 1
  ref = I_element
FEATURE [App::DocumentObjectGroupPython] G4_I  # scripted group (container) (typed FeaturePython)
  Dunit = g/cm3
  Dvalue = 4.93
  Group = -> [I_element010]
  conduct = 2
  density = 1
  expand = 3
  formula = I
  name = G4_I
  specific = 4
FEATURE [App::DocumentObjectGroupPython] Xe_element001  label="Xe_element : 1"  # scripted group (container) (typed FeaturePython)
  n = 1
  ref = Xe_element
FEATURE [App::DocumentObjectGroupPython] G4_Xe  # scripted group (container) (typed FeaturePython)
  Dunit = g/cm3
  Dvalue = 0.00548536
  Group = -> [Xe_element001]
  conduct = 2
  density = 1
  expand = 3
  formula = Xe
  name = G4_Xe
  specific = 4
FEATURE [App::DocumentObjectGroupPython] Cs_element003  label="Cs_element : 003"  # scripted group (container) (typed FeaturePython)
  n = 1
  ref = Cs_element
FEATURE [App::DocumentObjectGroupPython] G4_Cs  # scripted group (container) (typed FeaturePython)
  Dunit = g/cm3
  Dvalue = 1.873
  Group = -> [Cs_element003]
  conduct = 2
  density = 1
  expand = 3
  formula = Cs
  name = G4_Cs
  specific = 4
FEATURE [App::DocumentObjectGroupPython] Ba_element003  label="Ba_element : 003"  # scripted group (container) (typed FeaturePython)
  n = 1
  ref = Ba_element
FEATURE [App::DocumentObjectGroupPython] G4_Ba  # scripted group (container) (typed FeaturePython)
  Dunit = g/cm3
  Dvalue = 3.5
  Group = -> [Ba_element003]
  conduct = 2
  density = 1
  expand = 3
  formula = Ba
  name = G4_Ba
  specific = 4
FEATURE [App::DocumentObjectGroupPython] La_element003  label="La_element : 003"  # scripted group (container) (typed FeaturePython)
  n = 1
  ref = La_element
FEATURE [App::DocumentObjectGroupPython] G4_La  # scripted group (container) (typed FeaturePython)
  Dunit = g/cm3
  Dvalue = 6.154
  Group = -> [La_element003]
  conduct = 2
  density = 1
  expand = 3
  formula = La
  name = G4_La
  specific = 4
FEATURE [App::DocumentObjectGroupPython] Ce_element002  label="Ce_element : 1"  # scripted group (container) (typed FeaturePython)
  n = 1
  ref = Ce_element
FEATURE [App::DocumentObjectGroupPython] G4_Ce  # scripted group (container) (typed FeaturePython)
  Dunit = g/cm3
  Dvalue = 6.657
  Group = -> [Ce_element002]
  conduct = 2
  density = 1
  expand = 3
  formula = Ce
  name = G4_Ce
  specific = 4
FEATURE [App::DocumentObjectGroupPython] Pr_element001  label="Pr_element : 1"  # scripted group (container) (typed FeaturePython)
  n = 1
  ref = Pr_element
FEATURE [App::DocumentObjectGroupPython] G4_Pr  # scripted group (container) (typed FeaturePython)
  Dunit = g/cm3
  Dvalue = 6.71
  Group = -> [Pr_element001]
  conduct = 2
  density = 1
  expand = 3
  formula = Pr
  name = G4_Pr
  specific = 4
FEATURE [App::DocumentObjectGroupPython] Nd_element001  label="Nd_element : 1"  # scripted group (container) (typed FeaturePython)
  n = 1
  ref = Nd_element
FEATURE [App::DocumentObjectGroupPython] G4_Nd  # scripted group (container) (typed FeaturePython)
  Dunit = g/cm3
  Dvalue = 6.9
  Group = -> [Nd_element001]
  conduct = 2
  density = 1
  expand = 3
  formula = Nd
  name = G4_Nd
  specific = 4
FEATURE [App::DocumentObjectGroupPython] Pm_element001  label="Pm_element : 1"  # scripted group (container) (typed FeaturePython)
  n = 1
  ref = Pm_element
FEATURE [App::DocumentObjectGroupPython] G4_Pm  # scripted group (container) (typed FeaturePython)
  Dunit = g/cm3
  Dvalue = 7.22
  Group = -> [Pm_element001]
  conduct = 2
  density = 1
  expand = 3
  formula = Pm
  name = G4_Pm
  specific = 4
FEATURE [App::DocumentObjectGroupPython] Sm_element001  label="Sm_element : 1"  # scripted group (container) (typed FeaturePython)
  n = 1
  ref = Sm_element
FEATURE [App::DocumentObjectGroupPython] G4_Sm  # scripted group (container) (typed FeaturePython)
  Dunit = g/cm3
  Dvalue = 7.46
  Group = -> [Sm_element001]
  conduct = 2
  density = 1
  expand = 3
  formula = Sm
  name = G4_Sm
  specific = 4
FEATURE [App::DocumentObjectGroupPython] Eu_element001  label="Eu_element : 1"  # scripted group (container) (typed FeaturePython)
  n = 1
  ref = Eu_element
FEATURE [App::DocumentObjectGroupPython] G4_Eu  # scripted group (container) (typed FeaturePython)
  Dunit = g/cm3
  Dvalue = 5.243
  Group = -> [Eu_element001]
  conduct = 2
  density = 1
  expand = 3
  formula = Eu
  name = G4_Eu
  specific = 4
FEATURE [App::DocumentObjectGroupPython] Gd_element002  label="Gd_element : 1"  # scripted group (container) (typed FeaturePython)
  n = 1
  ref = Gd_element
FEATURE [App::DocumentObjectGroupPython] G4_Gd  # scripted group (container) (typed FeaturePython)
  Dunit = g/cm3
  Dvalue = 7.9004
  Group = -> [Gd_element002]
  conduct = 2
  density = 1
  expand = 3
  formula = Gd
  name = G4_Gd
  specific = 4
FEATURE [App::DocumentObjectGroupPython] Tb_element001  label="Tb_element : 1"  # scripted group (container) (typed FeaturePython)
  n = 1
  ref = Tb_element
FEATURE [App::DocumentObjectGroupPython] G4_Tb  # scripted group (container) (typed FeaturePython)
  Dunit = g/cm3
  Dvalue = 8.229
  Group = -> [Tb_element001]
  conduct = 2
  density = 1
  expand = 3
  formula = Tb
  name = G4_Tb
  specific = 4
FEATURE [App::DocumentObjectGroupPython] Dy_element001  label="Dy_element : 1"  # scripted group (container) (typed FeaturePython)
  n = 1
  ref = Dy_element
FEATURE [App::DocumentObjectGroupPython] G4_Dy  # scripted group (container) (typed FeaturePython)
  Dunit = g/cm3
  Dvalue = 8.55
  Group = -> [Dy_element001]
  conduct = 2
  density = 1
  expand = 3
  formula = Dy
  name = G4_Dy
  specific = 4
FEATURE [App::DocumentObjectGroupPython] Ho_element001  label="Ho_element : 1"  # scripted group (container) (typed FeaturePython)
  n = 1
  ref = Ho_element
FEATURE [App::DocumentObjectGroupPython] G4_Ho  # scripted group (container) (typed FeaturePython)
  Dunit = g/cm3
  Dvalue = 8.795
  Group = -> [Ho_element001]
  conduct = 2
  density = 1
  expand = 3
  formula = Ho
  name = G4_Ho
  specific = 4
FEATURE [App::DocumentObjectGroupPython] Er_element001  label="Er_element : 1"  # scripted group (container) (typed FeaturePython)
  n = 1
  ref = Er_element
FEATURE [App::DocumentObjectGroupPython] G4_Er  # scripted group (container) (typed FeaturePython)
  Dunit = g/cm3
  Dvalue = 9.066
  Group = -> [Er_element001]
  conduct = 2
  density = 1
  expand = 3
  formula = Er
  name = G4_Er
  specific = 4
FEATURE [App::DocumentObjectGroupPython] Tm_element001  label="Tm_element : 1"  # scripted group (container) (typed FeaturePython)
  n = 1
  ref = Tm_element
FEATURE [App::DocumentObjectGroupPython] G4_Tm  # scripted group (container) (typed FeaturePython)
  Dunit = g/cm3
  Dvalue = 9.321
  Group = -> [Tm_element001]
  conduct = 2
  density = 1
  expand = 3
  formula = Tm
  name = G4_Tm
  specific = 4
FEATURE [App::DocumentObjectGroupPython] Yb_element001  label="Yb_element : 1"  # scripted group (container) (typed FeaturePython)
  n = 1
  ref = Yb_element
FEATURE [App::DocumentObjectGroupPython] G4_Yb  # scripted group (container) (typed FeaturePython)
  Dunit = g/cm3
  Dvalue = 6.73
  Group = -> [Yb_element001]
  conduct = 2
  density = 1
  expand = 3
  formula = Yb
  name = G4_Yb
  specific = 4
FEATURE [App::DocumentObjectGroupPython] Lu_element001  label="Lu_element : 1"  # scripted group (container) (typed FeaturePython)
  n = 1
  ref = Lu_element
FEATURE [App::DocumentObjectGroupPython] G4_Lu  # scripted group (container) (typed FeaturePython)
  Dunit = g/cm3
  Dvalue = 9.84
  Group = -> [Lu_element001]
  conduct = 2
  density = 1
  expand = 3
  formula = Lu
  name = G4_Lu
  specific = 4
FEATURE [App::DocumentObjectGroupPython] Hf_element001  label="Hf_element : 1"  # scripted group (container) (typed FeaturePython)
  n = 1
  ref = Hf_element
FEATURE [App::DocumentObjectGroupPython] G4_Hf  # scripted group (container) (typed FeaturePython)
  Dunit = g/cm3
  Dvalue = 13.31
  Group = -> [Hf_element001]
  conduct = 2
  density = 1
  expand = 3
  formula = Hf
  name = G4_Hf
  specific = 4
FEATURE [App::DocumentObjectGroupPython] Ta_element001  label="Ta_element : 1"  # scripted group (container) (typed FeaturePython)
  n = 1
  ref = Ta_element
FEATURE [App::DocumentObjectGroupPython] G4_Ta  # scripted group (container) (typed FeaturePython)
  Dunit = g/cm3
  Dvalue = 16.654
  Group = -> [Ta_element001]
  conduct = 2
  density = 1
  expand = 3
  formula = Ta
  name = G4_Ta
  specific = 4
FEATURE [App::DocumentObjectGroupPython] W_element004  label="W_element : 004"  # scripted group (container) (typed FeaturePython)
  n = 1
  ref = W_element
FEATURE [App::DocumentObjectGroupPython] G4_W  # scripted group (container) (typed FeaturePython)
  Dunit = g/cm3
  Dvalue = 19.3
  Group = -> [W_element004]
  conduct = 2
  density = 1
  expand = 3
  formula = W
  name = G4_W
  specific = 4
FEATURE [App::DocumentObjectGroupPython] Re_element001  label="Re_element : 1"  # scripted group (container) (typed FeaturePython)
  n = 1
  ref = Re_element
FEATURE [App::DocumentObjectGroupPython] G4_Re  # scripted group (container) (typed FeaturePython)
  Dunit = g/cm3
  Dvalue = 21.02
  Group = -> [Re_element001]
  conduct = 2
  density = 1
  expand = 3
  formula = Re
  name = G4_Re
  specific = 4
FEATURE [App::DocumentObjectGroupPython] Os_element001  label="Os_element : 1"  # scripted group (container) (typed FeaturePython)
  n = 1
  ref = Os_element
FEATURE [App::DocumentObjectGroupPython] G4_Os  # scripted group (container) (typed FeaturePython)
  Dunit = g/cm3
  Dvalue = 22.57
  Group = -> [Os_element001]
  conduct = 2
  density = 1
  expand = 3
  formula = Os
  name = G4_Os
  specific = 4
FEATURE [App::DocumentObjectGroupPython] Ir_element001  label="Ir_element : 1"  # scripted group (container) (typed FeaturePython)
  n = 1
  ref = Ir_element
FEATURE [App::DocumentObjectGroupPython] G4_Ir  # scripted group (container) (typed FeaturePython)
  Dunit = g/cm3
  Dvalue = 22.42
  Group = -> [Ir_element001]
  conduct = 2
  density = 1
  expand = 3
  formula = Ir
  name = G4_Ir
  specific = 4
FEATURE [App::DocumentObjectGroupPython] Pt_element001  label="Pt_element : 1"  # scripted group (container) (typed FeaturePython)
  n = 1
  ref = Pt_element
FEATURE [App::DocumentObjectGroupPython] G4_Pt  # scripted group (container) (typed FeaturePython)
  Dunit = g/cm3
  Dvalue = 21.45
  Group = -> [Pt_element001]
  conduct = 2
  density = 1
  expand = 3
  formula = Pt
  name = G4_Pt
  specific = 4
FEATURE [App::DocumentObjectGroupPython] Au_element001  label="Au_element : 1"  # scripted group (container) (typed FeaturePython)
  n = 1
  ref = Au_element
FEATURE [App::DocumentObjectGroupPython] G4_Au  # scripted group (container) (typed FeaturePython)
  Dunit = g/cm3
  Dvalue = 19.32
  Group = -> [Au_element001]
  conduct = 2
  density = 1
  expand = 3
  formula = Au
  name = G4_Au
  specific = 4
FEATURE [App::DocumentObjectGroupPython] Hg_element002  label="Hg_element : 002"  # scripted group (container) (typed FeaturePython)
  n = 1
  ref = Hg_element
FEATURE [App::DocumentObjectGroupPython] G4_Hg  # scripted group (container) (typed FeaturePython)
  Dunit = g/cm3
  Dvalue = 13.546
  Group = -> [Hg_element002]
  conduct = 2
  density = 1
  expand = 3
  formula = Hg
  name = G4_Hg
  specific = 4
FEATURE [App::DocumentObjectGroupPython] Tl_element002  label="Tl_element : 002"  # scripted group (container) (typed FeaturePython)
  n = 1
  ref = Tl_element
FEATURE [App::DocumentObjectGroupPython] G4_Tl  # scripted group (container) (typed FeaturePython)
  Dunit = g/cm3
  Dvalue = 11.72
  Group = -> [Tl_element002]
  conduct = 2
  density = 1
  expand = 3
  formula = Tl
  name = G4_Tl
  specific = 4
FEATURE [App::DocumentObjectGroupPython] Pb_element003  label="Pb_element : 1"  # scripted group (container) (typed FeaturePython)
  n = 1
  ref = Pb_element
FEATURE [App::DocumentObjectGroupPython] G4_Pb  # scripted group (container) (typed FeaturePython)
  Dunit = g/cm3
  Dvalue = 11.35
  Group = -> [Pb_element003]
  conduct = 2
  density = 1
  expand = 3
  formula = Pb
  name = G4_Pb
  specific = 4
FEATURE [App::DocumentObjectGroupPython] Bi_element002  label="Bi_element : 1"  # scripted group (container) (typed FeaturePython)
  n = 1
  ref = Bi_element
FEATURE [App::DocumentObjectGroupPython] G4_Bi  # scripted group (container) (typed FeaturePython)
  Dunit = g/cm3
  Dvalue = 9.747
  Group = -> [Bi_element002]
  conduct = 2
  density = 1
  expand = 3
  formula = Bi
  name = G4_Bi
  specific = 4
FEATURE [App::DocumentObjectGroupPython] Po_element001  label="Po_element : 1"  # scripted group (container) (typed FeaturePython)
  n = 1
  ref = Po_element
FEATURE [App::DocumentObjectGroupPython] G4_Po  # scripted group (container) (typed FeaturePython)
  Dunit = g/cm3
  Dvalue = 9.32
  Group = -> [Po_element001]
  conduct = 2
  density = 1
  expand = 3
  formula = Po
  name = G4_Po
  specific = 4
FEATURE [App::DocumentObjectGroupPython] At_element001  label="At_element : 1"  # scripted group (container) (typed FeaturePython)
  n = 1
  ref = At_element
FEATURE [App::DocumentObjectGroupPython] G4_At  # scripted group (container) (typed FeaturePython)
  Dunit = g/cm3
  Dvalue = 9.32
  Group = -> [At_element001]
  conduct = 2
  density = 1
  expand = 3
  formula = At
  name = G4_At
  specific = 4
FEATURE [App::DocumentObjectGroupPython] Rn_element001  label="Rn_element : 1"  # scripted group (container) (typed FeaturePython)
  n = 1
  ref = Rn_element
FEATURE [App::DocumentObjectGroupPython] G4_Rn  # scripted group (container) (typed FeaturePython)
  Dunit = g/cm3
  Dvalue = 0.00900662
  Group = -> [Rn_element001]
  conduct = 2
  density = 1
  expand = 3
  formula = Rn
  name = G4_Rn
  specific = 4
FEATURE [App::DocumentObjectGroupPython] Fr_element001  label="Fr_element : 1"  # scripted group (container) (typed FeaturePython)
  n = 1
  ref = Fr_element
FEATURE [App::DocumentObjectGroupPython] G4_Fr  # scripted group (container) (typed FeaturePython)
  Dunit = g/cm3
  Dvalue = 1
  Group = -> [Fr_element001]
  conduct = 2
  density = 1
  expand = 3
  formula = Fr
  name = G4_Fr
  specific = 4
FEATURE [App::DocumentObjectGroupPython] Ra_element001  label="Ra_element : 1"  # scripted group (container) (typed FeaturePython)
  n = 1
  ref = Ra_element
FEATURE [App::DocumentObjectGroupPython] G4_Ra  # scripted group (container) (typed FeaturePython)
  Dunit = g/cm3
  Dvalue = 5
  Group = -> [Ra_element001]
  conduct = 2
  density = 1
  expand = 3
  formula = Ra
  name = G4_Ra
  specific = 4
FEATURE [App::DocumentObjectGroupPython] Ac_element001  label="Ac_element : 1"  # scripted group (container) (typed FeaturePython)
  n = 1
  ref = Ac_element
FEATURE [App::DocumentObjectGroupPython] G4_Ac  # scripted group (container) (typed FeaturePython)
  Dunit = g/cm3
  Dvalue = 10.07
  Group = -> [Ac_element001]
  conduct = 2
  density = 1
  expand = 3
  formula = Ac
  name = G4_Ac
  specific = 4
FEATURE [App::DocumentObjectGroupPython] Th_element001  label="Th_element : 1"  # scripted group (container) (typed FeaturePython)
  n = 1
  ref = Th_element
FEATURE [App::DocumentObjectGroupPython] G4_Th  # scripted group (container) (typed FeaturePython)
  Dunit = g/cm3
  Dvalue = 11.72
  Group = -> [Th_element001]
  conduct = 2
  density = 1
  expand = 3
  formula = Th
  name = G4_Th
  specific = 4
FEATURE [App::DocumentObjectGroupPython] Pa_element001  label="Pa_element : 1"  # scripted group (container) (typed FeaturePython)
  n = 1
  ref = Pa_element
FEATURE [App::DocumentObjectGroupPython] G4_Pa  # scripted group (container) (typed FeaturePython)
  Dunit = g/cm3
  Dvalue = 15.37
  Group = -> [Pa_element001]
  conduct = 2
  density = 1
  expand = 3
  formula = Pa
  name = G4_Pa
  specific = 4
FEATURE [App::DocumentObjectGroupPython] U_element004  label="U_element : 004"  # scripted group (container) (typed FeaturePython)
  n = 1
  ref = U_element
FEATURE [App::DocumentObjectGroupPython] G4_U  # scripted group (container) (typed FeaturePython)
  Dunit = g/cm3
  Dvalue = 18.95
  Group = -> [U_element004]
  conduct = 2
  density = 1
  expand = 3
  formula = U
  name = G4_U
  specific = 4
FEATURE [App::DocumentObjectGroupPython] Np_element001  label="Np_element : 1"  # scripted group (container) (typed FeaturePython)
  n = 1
  ref = Np_element
FEATURE [App::DocumentObjectGroupPython] G4_Np  # scripted group (container) (typed FeaturePython)
  Dunit = g/cm3
  Dvalue = 20.25
  Group = -> [Np_element001]
  conduct = 2
  density = 1
  expand = 3
  formula = Np
  name = G4_Np
  specific = 4
FEATURE [App::DocumentObjectGroupPython] Pu_element002  label="Pu_element : 002"  # scripted group (container) (typed FeaturePython)
  n = 1
  ref = Pu_element
FEATURE [App::DocumentObjectGroupPython] G4_Pu  # scripted group (container) (typed FeaturePython)
  Dunit = g/cm3
  Dvalue = 19.84
  Group = -> [Pu_element002]
  conduct = 2
  density = 1
  expand = 3
  formula = Pu
  name = G4_Pu
  specific = 4
FEATURE [App::DocumentObjectGroupPython] Am_element001  label="Am_element : 1"  # scripted group (container) (typed FeaturePython)
  n = 1
  ref = Am_element
FEATURE [App::DocumentObjectGroupPython] G4_Am  # scripted group (container) (typed FeaturePython)
  Dunit = g/cm3
  Dvalue = 13.67
  Group = -> [Am_element001]
  conduct = 2
  density = 1
  expand = 3
  formula = Am
  name = G4_Am
  specific = 4
FEATURE [App::DocumentObjectGroupPython] Cm_element001  label="Cm_element : 1"  # scripted group (container) (typed FeaturePython)
  n = 1
  ref = Cm_element
FEATURE [App::DocumentObjectGroupPython] G4_Cm  # scripted group (container) (typed FeaturePython)
  Dunit = g/cm3
  Dvalue = 13.51
  Group = -> [Cm_element001]
  conduct = 2
  density = 1
  expand = 3
  formula = Cm
  name = G4_Cm
  specific = 4
FEATURE [App::DocumentObjectGroupPython] Bk_element001  label="Bk_element : 1"  # scripted group (container) (typed FeaturePython)
  n = 1
  ref = Bk_element
FEATURE [App::DocumentObjectGroupPython] G4_Bk  # scripted group (container) (typed FeaturePython)
  Dunit = g/cm3
  Dvalue = 14
  Group = -> [Bk_element001]
  conduct = 2
  density = 1
  expand = 3
  formula = Bk
  name = G4_Bk
  specific = 4
FEATURE [App::DocumentObjectGroupPython] Cf_element001  label="Cf_element : 1"  # scripted group (container) (typed FeaturePython)
  n = 1
  ref = Cf_element
FEATURE [App::DocumentObjectGroupPython] G4_Cf  # scripted group (container) (typed FeaturePython)
  Dunit = g/cm3
  Dvalue = 10
  Group = -> [Cf_element001]
  conduct = 2
  density = 1
  expand = 3
  formula = Cf
  name = G4_Cf
  specific = 4
FEATURE [App::DocumentObjectGroupPython] Element  # scripted group (container) (typed FeaturePython)
  Group = -> [G4_H,G4_He,G4_Li,G4_Be,G4_B,G4_C,G4_N,G4_O,G4_F,G4_Ne,G4_Na,G4_Mg,G4_Al,G4_Si,G4_P,G4_S,G4_Cl,G4_Ar,G4_K,G4_Ca,G4_Sc,G4_Ti,G4_V,G4_Cr,G4_Mn,G4_Fe,G4_Co,G4_Ni,G4_Cu,G4_Zn,G4_Ga,G4_Ge,G4_As,G4_Se,G4_Br,G4_Kr,G4_Rb,G4_Sr,G4_Y,G4_Zr,G4_Nb,G4_Mo,G4_Tc,G4_Ru,G4_Rh,G4_Pd,G4_Ag,G4_Cd,G4_In,G4_Sn,G4_Sb,G4_Te,G4_I,G4_Xe,G4_Cs,G4_Ba,G4_La,G4_Ce,G4_Pr,G4_Nd,G4_Pm,G4_Sm,G4_Eu,G4_Gd,G4_Tb,G4_Dy,G4_Ho,G4_Er,+30 more]
FEATURE [App::DocumentObjectGroupPython] H_element114  label="H_element : 063"  # scripted group (container) (typed FeaturePython)
  n = 2
  ref = H_element
FEATURE [App::DocumentObjectGroupPython] G4_lH2  # scripted group (container) (typed FeaturePython)
  Dunit = g/cm3
  Dvalue = 0.0708
  Group = -> [H_element114]
  conduct = 2
  density = 1
  expand = 3
  formula = G4_lH2
  name = G4_lH2
  specific = 4
FEATURE [App::DocumentObjectGroupPython] N_element049  label="N_element : 022"  # scripted group (container) (typed FeaturePython)
  n = 2
  ref = N_element
FEATURE [App::DocumentObjectGroupPython] G4_lN2  # scripted group (container) (typed FeaturePython)
  Dunit = g/cm3
  Dvalue = 0.807
  Group = -> [N_element049]
  conduct = 2
  density = 1
  expand = 3
  formula = G4_lN2
  name = G4_lN2
  specific = 4
FEATURE [App::DocumentObjectGroupPython] O_element106  label="O_element : 060"  # scripted group (container) (typed FeaturePython)
  n = 2
  ref = O_element
FEATURE [App::DocumentObjectGroupPython] G4_lO2  # scripted group (container) (typed FeaturePython)
  Dunit = g/cm3
  Dvalue = 1.141
  Group = -> [O_element106]
  conduct = 2
  density = 1
  expand = 3
  formula = G4_lO2
  name = G4_lO2
  specific = 4
FEATURE [App::DocumentObjectGroupPython] Ar  label="Ar : 1"  # scripted group (container) (typed FeaturePython)
  n = 1
  ref = Ar
FEATURE [App::DocumentObjectGroupPython] G4_lAr  # scripted group (container) (typed FeaturePython)
  Dunit = g/cm3
  Dvalue = 1.396
  Group = -> [Ar]
  conduct = 2
  density = 1
  expand = 3
  formula = G4_lAr
  name = G4_lAr
  specific = 4
FEATURE [App::DocumentObjectGroupPython] Br  label="Br : 1"  # scripted group (container) (typed FeaturePython)
  n = 1
  ref = Br
FEATURE [App::DocumentObjectGroupPython] G4_lBr  # scripted group (container) (typed FeaturePython)
  Dunit = g/cm3
  Dvalue = 3.1028
  Group = -> [Br]
  conduct = 2
  density = 1
  expand = 3
  formula = G4_lBr
  name = G4_lBr
  specific = 4
FEATURE [App::DocumentObjectGroupPython] Kr  label="Kr : 1"  # scripted group (container) (typed FeaturePython)
  n = 1
  ref = Kr
FEATURE [App::DocumentObjectGroupPython] G4_lKr  # scripted group (container) (typed FeaturePython)
  Dunit = g/cm3
  Dvalue = 2.418
  Group = -> [Kr]
  conduct = 2
  density = 1
  expand = 3
  formula = G4_lKr
  name = G4_lKr
  specific = 4
FEATURE [App::DocumentObjectGroupPython] Xe  label="Xe : 1"  # scripted group (container) (typed FeaturePython)
  n = 1
  ref = Xe
FEATURE [App::DocumentObjectGroupPython] G4_lXe  # scripted group (container) (typed FeaturePython)
  Dunit = g/cm3
  Dvalue = 2.953
  Group = -> [Xe]
  conduct = 2
  density = 1
  expand = 3
  formula = G4_lXe
  name = G4_lXe
  specific = 4
FEATURE [App::DocumentObjectGroupPython] O_element107  label="O_element : 061"  # scripted group (container) (typed FeaturePython)
  n = 4
  ref = O_element
FEATURE [App::DocumentObjectGroupPython] Pb_element004  label="Pb_element : 002"  # scripted group (container) (typed FeaturePython)
  n = 1
  ref = Pb_element
FEATURE [App::DocumentObjectGroupPython] W_element005  label="W_element : 005"  # scripted group (container) (typed FeaturePython)
  n = 1
  ref = W_element
FEATURE [App::DocumentObjectGroupPython] G4_PbWO4  # scripted group (container) (typed FeaturePython)
  Dunit = g/cm3
  Dvalue = 8.28
  Group = -> [O_element107,Pb_element004,W_element005]
  conduct = 2
  density = 1
  expand = 3
  formula = G4_PbWO4
  name = G4_PbWO4
  specific = 4
FEATURE [App::DocumentObjectGroupPython] alactic  label="alactic : 1"  # scripted group (container) (typed FeaturePython)
  n = 1
  ref = alactic
FEATURE [App::DocumentObjectGroupPython] G4_Galactic  # scripted group (container) (typed FeaturePython)
  Dunit = g/cm3
  Dvalue = 0
  Group = -> [alactic]
  conduct = 2
  density = 1
  expand = 3
  formula = G4_Galactic
  name = G4_Galactic
  specific = 4
FEATURE [App::DocumentObjectGroupPython] RAPHITE_POROUS  label="RAPHITE_POROUS : 1"  # scripted group (container) (typed FeaturePython)
  n = 1
  ref = RAPHITE_POROUS
FEATURE [App::DocumentObjectGroupPython] G4_GRAPHITE_POROUS  # scripted group (container) (typed FeaturePython)
  Dunit = g/cm3
  Dvalue = 1.7
  Group = -> [RAPHITE_POROUS]
  conduct = 2
  density = 1
  expand = 3
  formula = G4_GRAPHITE_POROUS
  name = G4_GRAPHITE_POROUS
  specific = 4
FEATURE [App::DocumentObjectGroupPython] H_element115  label="H_element : 0.150"  # scripted group (container) (typed FeaturePython)
  n = 0.080538
FEATURE [App::DocumentObjectGroupPython] C_element125  label="C_element : 0.600"  # scripted group (container) (typed FeaturePython)
  n = 0.599848
FEATURE [App::DocumentObjectGroupPython] O_element108  label="O_element : 0.320"  # scripted group (container) (typed FeaturePython)
  n = 0.319614
FEATURE [App::DocumentObjectGroupPython] G4_LUCITE  # scripted group (container) (typed FeaturePython)
  Dunit = g/cm3
  Dvalue = 1.19
  Group = -> [H_element115,C_element125,O_element108]
  conduct = 2
  density = 1
  expand = 3
  formula = G4_LUCITE
  name = G4_LUCITE
  specific = 4
FEATURE [App::DocumentObjectGroupPython] Cu_element002  label="Cu_element : 62"  # scripted group (container) (typed FeaturePython)
  n = 62
  ref = Cu_element
FEATURE [App::DocumentObjectGroupPython] Zn_element002  label="Zn_element : 35"  # scripted group (container) (typed FeaturePython)
  n = 35
  ref = Zn_element
FEATURE [App::DocumentObjectGroupPython] Pb_element005  label="Pb_element : 3"  # scripted group (container) (typed FeaturePython)
  n = 3
  ref = Pb_element
FEATURE [App::DocumentObjectGroupPython] G4_BRASS  # scripted group (container) (typed FeaturePython)
  Dunit = g/cm3
  Dvalue = 8.52
  Group = -> [Cu_element002,Zn_element002,Pb_element005]
  conduct = 2
  density = 1
  expand = 3
  formula = G4_BRASS
  name = G4_BRASS
  specific = 4
FEATURE [App::DocumentObjectGroupPython] Cu_element003  label="Cu_element : 89"  # scripted group (container) (typed FeaturePython)
  n = 89
  ref = Cu_element
FEATURE [App::DocumentObjectGroupPython] Zn_element003  label="Zn_element : 9"  # scripted group (container) (typed FeaturePython)
  n = 9
  ref = Zn_element
FEATURE [App::DocumentObjectGroupPython] Pb_element006  label="Pb_element : 2"  # scripted group (container) (typed FeaturePython)
  n = 2
  ref = Pb_element
FEATURE [App::DocumentObjectGroupPython] G4_BRONZE  # scripted group (container) (typed FeaturePython)
  Dunit = g/cm3
  Dvalue = 8.82
  Group = -> [Cu_element003,Zn_element003,Pb_element006]
  conduct = 2
  density = 1
  expand = 3
  formula = G4_BRONZE
  name = G4_BRONZE
  specific = 4
FEATURE [App::DocumentObjectGroupPython] Fe_element008  label="Fe_element : 74"  # scripted group (container) (typed FeaturePython)
  n = 74
  ref = Fe_element
FEATURE [App::DocumentObjectGroupPython] Cr_element002  label="Cr_element : 18"  # scripted group (container) (typed FeaturePython)
  n = 18
  ref = Cr_element
FEATURE [App::DocumentObjectGroupPython] Ni_element002  label="Ni_element : 8"  # scripted group (container) (typed FeaturePython)
  n = 8
  ref = Ni_element
FEATURE [App::DocumentObjectGroupPython] G4_STAINLESS_STEEL  label="G4_STAINLESS-STEEL"  # scripted group (container) (typed FeaturePython)
  Dunit = g/cm3
  Dvalue = 8
  Group = -> [Fe_element008,Cr_element002,Ni_element002]
  conduct = 2
  density = 1
  expand = 3
  formula = G4_STAINLESS-STEEL
  name = G4_STAINLESS-STEEL
  specific = 4
FEATURE [App::DocumentObjectGroupPython] H_element116  label="H_element : 064"  # scripted group (container) (typed FeaturePython)
  n = 18
  ref = H_element
FEATURE [App::DocumentObjectGroupPython] C_element126  label="C_element : 071"  # scripted group (container) (typed FeaturePython)
  n = 12
  ref = C_element
FEATURE [App::DocumentObjectGroupPython] O_element109  label="O_element : 062"  # scripted group (container) (typed FeaturePython)
  n = 7
  ref = O_element
FEATURE [App::DocumentObjectGroupPython] G4_CR39  # scripted group (container) (typed FeaturePython)
  Dunit = g/cm3
  Dvalue = 1.32
  Group = -> [H_element116,C_element126,O_element109]
  conduct = 2
  density = 1
  expand = 3
  formula = G4_CR39
  name = G4_CR39
  specific = 4
FEATURE [App::DocumentObjectGroupPython] H_element117  label="H_element : 38"  # scripted group (container) (typed FeaturePython)
  n = 38
  ref = H_element
FEATURE [App::DocumentObjectGroupPython] C_element127  label="C_element : 072"  # scripted group (container) (typed FeaturePython)
  n = 18
  ref = C_element
FEATURE [App::DocumentObjectGroupPython] O_element110  label="O_element : 063"  # scripted group (container) (typed FeaturePython)
  n = 1
  ref = O_element
FEATURE [App::DocumentObjectGroupPython] G4_OCTADECANOL  # scripted group (container) (typed FeaturePython)
  Dunit = g/cm3
  Dvalue = 0.812
  Group = -> [H_element117,C_element127,O_element110]
  conduct = 2
  density = 1
  expand = 3
  formula = G4_OCTADECANOL
  name = G4_OCTADECANOL
  specific = 4
FEATURE [App::DocumentObjectGroupPython] HEP  # scripted group (container) (typed FeaturePython)
  Group = -> [G4_lH2,G4_lN2,G4_lO2,G4_lAr,G4_lBr,G4_lKr,G4_lXe,G4_PbWO4,G4_Galactic,G4_GRAPHITE_POROUS,G4_LUCITE,G4_BRASS,G4_BRONZE,G4_STAINLESS_STEEL,G4_CR39,G4_OCTADECANOL]
FEATURE [App::DocumentObjectGroupPython] C_element128  label="C_element : 073"  # scripted group (container) (typed FeaturePython)
  n = 14
  ref = C_element
FEATURE [App::DocumentObjectGroupPython] H_element118  label="H_element : 065"  # scripted group (container) (typed FeaturePython)
  n = 10
  ref = H_element
FEATURE [App::DocumentObjectGroupPython] O_element111  label="O_element : 064"  # scripted group (container) (typed FeaturePython)
  n = 2
  ref = O_element
FEATURE [App::DocumentObjectGroupPython] N_element050  label="N_element : 023"  # scripted group (container) (typed FeaturePython)
  n = 2
  ref = N_element
FEATURE [App::DocumentObjectGroupPython] G4_KEVLAR  # scripted group (container) (typed FeaturePython)
  Dunit = g/cm3
  Dvalue = 1.44
  Group = -> [C_element128,H_element118,O_element111,N_element050]
  conduct = 2
  density = 1
  expand = 3
  formula = G4_KEVLAR
  name = G4_KEVLAR
  specific = 4
FEATURE [App::DocumentObjectGroupPython] C_element129  label="C_element : 074"  # scripted group (container) (typed FeaturePython)
  n = 10
  ref = C_element
FEATURE [App::DocumentObjectGroupPython] H_element119  label="H_element : 066"  # scripted group (container) (typed FeaturePython)
  n = 8
  ref = H_element
FEATURE [App::DocumentObjectGroupPython] O_element112  label="O_element : 065"  # scripted group (container) (typed FeaturePython)
  n = 4
  ref = O_element
FEATURE [App::DocumentObjectGroupPython] G4_DACRON  # scripted group (container) (typed FeaturePython)
  Dunit = g/cm3
  Dvalue = 1.4
  Group = -> [C_element129,H_element119,O_element112]
  conduct = 2
  density = 1
  expand = 3
  formula = G4_DACRON
  name = G4_DACRON
  specific = 4
FEATURE [App::DocumentObjectGroupPython] C_element130  label="C_element : 075"  # scripted group (container) (typed FeaturePython)
  n = 4
  ref = C_element
FEATURE [App::DocumentObjectGroupPython] H_element120  label="H_element : 067"  # scripted group (container) (typed FeaturePython)
  n = 5
  ref = H_element
FEATURE [App::DocumentObjectGroupPython] Cl_element030  label="Cl_element : 016"  # scripted group (container) (typed FeaturePython)
  n = 1
  ref = Cl_element
FEATURE [App::DocumentObjectGroupPython] G4_NEOPRENE  # scripted group (container) (typed FeaturePython)
  Dunit = g/cm3
  Dvalue = 1.23
  Group = -> [C_element130,H_element120,Cl_element030]
  conduct = 2
  density = 1
  expand = 3
  formula = G4_NEOPRENE
  name = G4_NEOPRENE
  specific = 4
FEATURE [App::DocumentObjectGroupPython] Space  # scripted group (container) (typed FeaturePython)
  Group = -> [G4_KEVLAR,G4_DACRON,G4_NEOPRENE]
FEATURE [App::DocumentObjectGroupPython] H_element121  label="H_element : 068"  # scripted group (container) (typed FeaturePython)
  n = 5
  ref = H_element
FEATURE [App::DocumentObjectGroupPython] C_element131  label="C_element : 076"  # scripted group (container) (typed FeaturePython)
  n = 4
  ref = C_element
FEATURE [App::DocumentObjectGroupPython] N_element051  label="N_element : 3"  # scripted group (container) (typed FeaturePython)
  n = 3
  ref = N_element
FEATURE [App::DocumentObjectGroupPython] O_element113  label="O_element : 066"  # scripted group (container) (typed FeaturePython)
  n = 1
  ref = O_element
FEATURE [App::DocumentObjectGroupPython] G4_CYTOSINE  # scripted group (container) (typed FeaturePython)
  Dunit = g/cm3
  Dvalue = 1.55
  Group = -> [H_element121,C_element131,N_element051,O_element113]
  conduct = 2
  density = 1
  expand = 3
  formula = G4_CYTOSINE
  name = G4_CYTOSINE
  specific = 4
FEATURE [App::DocumentObjectGroupPython] H_element122  label="H_element : 069"  # scripted group (container) (typed FeaturePython)
  n = 6
  ref = H_element
FEATURE [App::DocumentObjectGroupPython] C_element132  label="C_element : 077"  # scripted group (container) (typed FeaturePython)
  n = 5
  ref = C_element
FEATURE [App::DocumentObjectGroupPython] N_element052  label="N_element : 024"  # scripted group (container) (typed FeaturePython)
  n = 2
  ref = N_element
FEATURE [App::DocumentObjectGroupPython] O_element114  label="O_element : 067"  # scripted group (container) (typed FeaturePython)
  n = 2
  ref = O_element
FEATURE [App::DocumentObjectGroupPython] G4_THYMINE  # scripted group (container) (typed FeaturePython)
  Dunit = g/cm3
  Dvalue = 1.23
  Group = -> [H_element122,C_element132,N_element052,O_element114]
  conduct = 2
  density = 1
  expand = 3
  formula = G4_THYMINE
  name = G4_THYMINE
  specific = 4
FEATURE [App::DocumentObjectGroupPython] H_element123  label="H_element : 070"  # scripted group (container) (typed FeaturePython)
  n = 4
  ref = H_element
FEATURE [App::DocumentObjectGroupPython] C_element133  label="C_element : 078"  # scripted group (container) (typed FeaturePython)
  n = 4
  ref = C_element
FEATURE [App::DocumentObjectGroupPython] N_element053  label="N_element : 025"  # scripted group (container) (typed FeaturePython)
  n = 2
  ref = N_element
FEATURE [App::DocumentObjectGroupPython] O_element115  label="O_element : 068"  # scripted group (container) (typed FeaturePython)
  n = 2
  ref = O_element
FEATURE [App::DocumentObjectGroupPython] G4_URACIL  # scripted group (container) (typed FeaturePython)
  Dunit = g/cm3
  Dvalue = 1.32
  Group = -> [H_element123,C_element133,N_element053,O_element115]
  conduct = 2
  density = 1
  expand = 3
  formula = G4_URACIL
  name = G4_URACIL
  specific = 4
FEATURE [App::DocumentObjectGroupPython] H_element124  label="H_element : 071"  # scripted group (container) (typed FeaturePython)
  n = 4
  ref = H_element
FEATURE [App::DocumentObjectGroupPython] C_element134  label="C_element : 079"  # scripted group (container) (typed FeaturePython)
  n = 5
  ref = C_element
FEATURE [App::DocumentObjectGroupPython] N_element054  label="N_element : 026"  # scripted group (container) (typed FeaturePython)
  n = 5
  ref = N_element
FEATURE [App::DocumentObjectGroupPython] G4_DNA_ADENINE  # scripted group (container) (typed FeaturePython)
  Dunit = g/cm3
  Dvalue = 1
  Group = -> [H_element124,C_element134,N_element054]
  conduct = 2
  density = 1
  expand = 3
  formula = G4_DNA_ADENINE
  name = G4_DNA_ADENINE
  specific = 4
FEATURE [App::DocumentObjectGroupPython] H_element125  label="H_element : 072"  # scripted group (container) (typed FeaturePython)
  n = 4
  ref = H_element
FEATURE [App::DocumentObjectGroupPython] C_element135  label="C_element : 080"  # scripted group (container) (typed FeaturePython)
  n = 5
  ref = C_element
FEATURE [App::DocumentObjectGroupPython] N_element055  label="N_element : 027"  # scripted group (container) (typed FeaturePython)
  n = 5
  ref = N_element
FEATURE [App::DocumentObjectGroupPython] O_element116  label="O_element : 069"  # scripted group (container) (typed FeaturePython)
  n = 1
  ref = O_element
FEATURE [App::DocumentObjectGroupPython] G4_DNA_GUANINE  # scripted group (container) (typed FeaturePython)
  Dunit = g/cm3
  Dvalue = 1
  Group = -> [H_element125,C_element135,N_element055,O_element116]
  conduct = 2
  density = 1
  expand = 3
  formula = G4_DNA_GUANINE
  name = G4_DNA_GUANINE
  specific = 4
FEATURE [App::DocumentObjectGroupPython] H_element126  label="H_element : 073"  # scripted group (container) (typed FeaturePython)
  n = 4
  ref = H_element
FEATURE [App::DocumentObjectGroupPython] C_element136  label="C_element : 081"  # scripted group (container) (typed FeaturePython)
  n = 4
  ref = C_element
FEATURE [App::DocumentObjectGroupPython] N_element056  label="N_element : 028"  # scripted group (container) (typed FeaturePython)
  n = 3
  ref = N_element
FEATURE [App::DocumentObjectGroupPython] O_element117  label="O_element : 070"  # scripted group (container) (typed FeaturePython)
  n = 1
  ref = O_element
FEATURE [App::DocumentObjectGroupPython] G4_DNA_CYTOSINE  # scripted group (container) (typed FeaturePython)
  Dunit = g/cm3
  Dvalue = 1
  Group = -> [H_element126,C_element136,N_element056,O_element117]
  conduct = 2
  density = 1
  expand = 3
  formula = G4_DNA_CYTOSINE
  name = G4_DNA_CYTOSINE
  specific = 4
FEATURE [App::DocumentObjectGroupPython] H_element127  label="H_element : 074"  # scripted group (container) (typed FeaturePython)
  n = 5
  ref = H_element
FEATURE [App::DocumentObjectGroupPython] C_element137  label="C_element : 082"  # scripted group (container) (typed FeaturePython)
  n = 5
  ref = C_element
FEATURE [App::DocumentObjectGroupPython] N_element057  label="N_element : 029"  # scripted group (container) (typed FeaturePython)
  n = 2
  ref = N_element
FEATURE [App::DocumentObjectGroupPython] O_element118  label="O_element : 071"  # scripted group (container) (typed FeaturePython)
  n = 2
  ref = O_element
FEATURE [App::DocumentObjectGroupPython] G4_DNA_THYMINE  # scripted group (container) (typed FeaturePython)
  Dunit = g/cm3
  Dvalue = 1
  Group = -> [H_element127,C_element137,N_element057,O_element118]
  conduct = 2
  density = 1
  expand = 3
  formula = G4_DNA_THYMINE
  name = G4_DNA_THYMINE
  specific = 4
FEATURE [App::DocumentObjectGroupPython] H_element128  label="H_element : 075"  # scripted group (container) (typed FeaturePython)
  n = 3
  ref = H_element
FEATURE [App::DocumentObjectGroupPython] C_element138  label="C_element : 083"  # scripted group (container) (typed FeaturePython)
  n = 4
  ref = C_element
FEATURE [App::DocumentObjectGroupPython] N_element058  label="N_element : 030"  # scripted group (container) (typed FeaturePython)
  n = 2
  ref = N_element
FEATURE [App::DocumentObjectGroupPython] O_element119  label="O_element : 072"  # scripted group (container) (typed FeaturePython)
  n = 2
  ref = O_element
FEATURE [App::DocumentObjectGroupPython] G4_DNA_URACIL  # scripted group (container) (typed FeaturePython)
  Dunit = g/cm3
  Dvalue = 1
  Group = -> [H_element128,C_element138,N_element058,O_element119]
  conduct = 2
  density = 1
  expand = 3
  formula = G4_DNA_URACIL
  name = G4_DNA_URACIL
  specific = 4
FEATURE [App::DocumentObjectGroupPython] H_element129  label="H_element : 076"  # scripted group (container) (typed FeaturePython)
  n = 10
  ref = H_element
FEATURE [App::DocumentObjectGroupPython] C_element139  label="C_element : 084"  # scripted group (container) (typed FeaturePython)
  n = 10
  ref = C_element
FEATURE [App::DocumentObjectGroupPython] N_element059  label="N_element : 031"  # scripted group (container) (typed FeaturePython)
  n = 5
  ref = N_element
FEATURE [App::DocumentObjectGroupPython] O_element120  label="O_element : 073"  # scripted group (container) (typed FeaturePython)
  n = 4
  ref = O_element
FEATURE [App::DocumentObjectGroupPython] G4_DNA_ADENOSINE  # scripted group (container) (typed FeaturePython)
  Dunit = g/cm3
  Dvalue = 1
  Group = -> [H_element129,C_element139,N_element059,O_element120]
  conduct = 2
  density = 1
  expand = 3
  formula = G4_DNA_ADENOSINE
  name = G4_DNA_ADENOSINE
  specific = 4
FEATURE [App::DocumentObjectGroupPython] H_element130  label="H_element : 077"  # scripted group (container) (typed FeaturePython)
  n = 10
  ref = H_element
FEATURE [App::DocumentObjectGroupPython] C_element140  label="C_element : 085"  # scripted group (container) (typed FeaturePython)
  n = 10
  ref = C_element
FEATURE [App::DocumentObjectGroupPython] N_element060  label="N_element : 032"  # scripted group (container) (typed FeaturePython)
  n = 5
  ref = N_element
FEATURE [App::DocumentObjectGroupPython] O_element121  label="O_element : 074"  # scripted group (container) (typed FeaturePython)
  n = 5
  ref = O_element
FEATURE [App::DocumentObjectGroupPython] G4_DNA_GUANOSINE  # scripted group (container) (typed FeaturePython)
  Dunit = g/cm3
  Dvalue = 1
  Group = -> [H_element130,C_element140,N_element060,O_element121]
  conduct = 2
  density = 1
  expand = 3
  formula = G4_DNA_GUANOSINE
  name = G4_DNA_GUANOSINE
  specific = 4
FEATURE [App::DocumentObjectGroupPython] H_element131  label="H_element : 078"  # scripted group (container) (typed FeaturePython)
  n = 10
  ref = H_element
FEATURE [App::DocumentObjectGroupPython] C_element141  label="C_element : 086"  # scripted group (container) (typed FeaturePython)
  n = 9
  ref = C_element
FEATURE [App::DocumentObjectGroupPython] N_element061  label="N_element : 033"  # scripted group (container) (typed FeaturePython)
  n = 3
  ref = N_element
FEATURE [App::DocumentObjectGroupPython] O_element122  label="O_element : 075"  # scripted group (container) (typed FeaturePython)
  n = 5
  ref = O_element
FEATURE [App::DocumentObjectGroupPython] G4_DNA_CYTIDINE  # scripted group (container) (typed FeaturePython)
  Dunit = g/cm3
  Dvalue = 1
  Group = -> [H_element131,C_element141,N_element061,O_element122]
  conduct = 2
  density = 1
  expand = 3
  formula = G4_DNA_CYTIDINE
  name = G4_DNA_CYTIDINE
  specific = 4
FEATURE [App::DocumentObjectGroupPython] H_element132  label="H_element : 079"  # scripted group (container) (typed FeaturePython)
  n = 9
  ref = H_element
FEATURE [App::DocumentObjectGroupPython] C_element142  label="C_element : 087"  # scripted group (container) (typed FeaturePython)
  n = 9
  ref = C_element
FEATURE [App::DocumentObjectGroupPython] N_element062  label="N_element : 034"  # scripted group (container) (typed FeaturePython)
  n = 2
  ref = N_element
FEATURE [App::DocumentObjectGroupPython] O_element123  label="O_element : 076"  # scripted group (container) (typed FeaturePython)
  n = 6
  ref = O_element
FEATURE [App::DocumentObjectGroupPython] G4_DNA_URIDINE  # scripted group (container) (typed FeaturePython)
  Dunit = g/cm3
  Dvalue = 1
  Group = -> [H_element132,C_element142,N_element062,O_element123]
  conduct = 2
  density = 1
  expand = 3
  formula = G4_DNA_URIDINE
  name = G4_DNA_URIDINE
  specific = 4
FEATURE [App::DocumentObjectGroupPython] H_element133  label="H_element : 080"  # scripted group (container) (typed FeaturePython)
  n = 11
  ref = H_element
FEATURE [App::DocumentObjectGroupPython] C_element143  label="C_element : 088"  # scripted group (container) (typed FeaturePython)
  n = 10
  ref = C_element
FEATURE [App::DocumentObjectGroupPython] N_element063  label="N_element : 035"  # scripted group (container) (typed FeaturePython)
  n = 2
  ref = N_element
FEATURE [App::DocumentObjectGroupPython] O_element124  label="O_element : 077"  # scripted group (container) (typed FeaturePython)
  n = 6
  ref = O_element
FEATURE [App::DocumentObjectGroupPython] G4_DNA_METHYLURIDINE  # scripted group (container) (typed FeaturePython)
  Dunit = g/cm3
  Dvalue = 1
  Group = -> [H_element133,C_element143,N_element063,O_element124]
  conduct = 2
  density = 1
  expand = 3
  formula = G4_DNA_METHYLURIDINE
  name = G4_DNA_METHYLURIDINE
  specific = 4
FEATURE [App::DocumentObjectGroupPython] P_element014  label="P_element : 003"  # scripted group (container) (typed FeaturePython)
  n = 1
  ref = P_element
FEATURE [App::DocumentObjectGroupPython] O_element125  label="O_element : 078"  # scripted group (container) (typed FeaturePython)
  n = 3
  ref = O_element
FEATURE [App::DocumentObjectGroupPython] G4_DNA_MONOPHOSPHATE  # scripted group (container) (typed FeaturePython)
  Dunit = g/cm3
  Dvalue = 1
  Group = -> [P_element014,O_element125]
  conduct = 2
  density = 1
  expand = 3
  formula = G4_DNA_MONOPHOSPHATE
  name = G4_DNA_MONOPHOSPHATE
  specific = 4
FEATURE [App::DocumentObjectGroupPython] H_element134  label="H_element : 081"  # scripted group (container) (typed FeaturePython)
  n = 10
  ref = H_element
FEATURE [App::DocumentObjectGroupPython] C_element144  label="C_element : 089"  # scripted group (container) (typed FeaturePython)
  n = 10
  ref = C_element
FEATURE [App::DocumentObjectGroupPython] N_element064  label="N_element : 036"  # scripted group (container) (typed FeaturePython)
  n = 5
  ref = N_element
FEATURE [App::DocumentObjectGroupPython] O_element126  label="O_element : 079"  # scripted group (container) (typed FeaturePython)
  n = 7
  ref = O_element
FEATURE [App::DocumentObjectGroupPython] P_element015  label="P_element : 004"  # scripted group (container) (typed FeaturePython)
  n = 1
  ref = P_element
FEATURE [App::DocumentObjectGroupPython] G4_DNA_A  # scripted group (container) (typed FeaturePython)
  Dunit = g/cm3
  Dvalue = 1
  Group = -> [H_element134,C_element144,N_element064,O_element126,P_element015]
  conduct = 2
  density = 1
  expand = 3
  formula = G4_DNA_A
  name = G4_DNA_A
  specific = 4
FEATURE [App::DocumentObjectGroupPython] H_element135  label="H_element : 082"  # scripted group (container) (typed FeaturePython)
  n = 10
  ref = H_element
FEATURE [App::DocumentObjectGroupPython] C_element145  label="C_element : 090"  # scripted group (container) (typed FeaturePython)
  n = 10
  ref = C_element
FEATURE [App::DocumentObjectGroupPython] N_element065  label="N_element : 037"  # scripted group (container) (typed FeaturePython)
  n = 5
  ref = N_element
FEATURE [App::DocumentObjectGroupPython] O_element127  label="O_element : 8"  # scripted group (container) (typed FeaturePython)
  n = 8
  ref = O_element
FEATURE [App::DocumentObjectGroupPython] P_element016  label="P_element : 005"  # scripted group (container) (typed FeaturePython)
  n = 1
  ref = P_element
FEATURE [App::DocumentObjectGroupPython] G4_DNA_G  # scripted group (container) (typed FeaturePython)
  Dunit = g/cm3
  Dvalue = 1
  Group = -> [H_element135,C_element145,N_element065,O_element127,P_element016]
  conduct = 2
  density = 1
  expand = 3
  formula = G4_DNA_G
  name = G4_DNA_G
  specific = 4
FEATURE [App::DocumentObjectGroupPython] H_element136  label="H_element : 083"  # scripted group (container) (typed FeaturePython)
  n = 10
  ref = H_element
FEATURE [App::DocumentObjectGroupPython] C_element146  label="C_element : 091"  # scripted group (container) (typed FeaturePython)
  n = 9
  ref = C_element
FEATURE [App::DocumentObjectGroupPython] N_element066  label="N_element : 038"  # scripted group (container) (typed FeaturePython)
  n = 3
  ref = N_element
FEATURE [App::DocumentObjectGroupPython] O_element128  label="O_element : 080"  # scripted group (container) (typed FeaturePython)
  n = 8
  ref = O_element
FEATURE [App::DocumentObjectGroupPython] P_element017  label="P_element : 006"  # scripted group (container) (typed FeaturePython)
  n = 1
  ref = P_element
FEATURE [App::DocumentObjectGroupPython] G4_DNA_C  # scripted group (container) (typed FeaturePython)
  Dunit = g/cm3
  Dvalue = 1
  Group = -> [H_element136,C_element146,N_element066,O_element128,P_element017]
  conduct = 2
  density = 1
  expand = 3
  formula = G4_DNA_C
  name = G4_DNA_C
  specific = 4
FEATURE [App::DocumentObjectGroupPython] H_element137  label="H_element : 084"  # scripted group (container) (typed FeaturePython)
  n = 9
  ref = H_element
FEATURE [App::DocumentObjectGroupPython] C_element147  label="C_element : 092"  # scripted group (container) (typed FeaturePython)
  n = 9
  ref = C_element
FEATURE [App::DocumentObjectGroupPython] N_element067  label="N_element : 039"  # scripted group (container) (typed FeaturePython)
  n = 2
  ref = N_element
FEATURE [App::DocumentObjectGroupPython] O_element129  label="O_element : 9"  # scripted group (container) (typed FeaturePython)
  n = 9
  ref = O_element
FEATURE [App::DocumentObjectGroupPython] P_element018  label="P_element : 007"  # scripted group (container) (typed FeaturePython)
  n = 1
  ref = P_element
FEATURE [App::DocumentObjectGroupPython] G4_DNA_U  # scripted group (container) (typed FeaturePython)
  Dunit = g/cm3
  Dvalue = 1
  Group = -> [H_element137,C_element147,N_element067,O_element129,P_element018]
  conduct = 2
  density = 1
  expand = 3
  formula = G4_DNA_U
  name = G4_DNA_U
  specific = 4
FEATURE [App::DocumentObjectGroupPython] H_element138  label="H_element : 085"  # scripted group (container) (typed FeaturePython)
  n = 11
  ref = H_element
FEATURE [App::DocumentObjectGroupPython] C_element148  label="C_element : 093"  # scripted group (container) (typed FeaturePython)
  n = 10
  ref = C_element
FEATURE [App::DocumentObjectGroupPython] N_element068  label="N_element : 040"  # scripted group (container) (typed FeaturePython)
  n = 2
  ref = N_element
FEATURE [App::DocumentObjectGroupPython] O_element130  label="O_element : 081"  # scripted group (container) (typed FeaturePython)
  n = 9
  ref = O_element
FEATURE [App::DocumentObjectGroupPython] P_element019  label="P_element : 008"  # scripted group (container) (typed FeaturePython)
  n = 1
  ref = P_element
FEATURE [App::DocumentObjectGroupPython] G4_DNA_MU  # scripted group (container) (typed FeaturePython)
  Dunit = g/cm3
  Dvalue = 1
  Group = -> [H_element138,C_element148,N_element068,O_element130,P_element019]
  conduct = 2
  density = 1
  expand = 3
  formula = G4_DNA_MU
  name = G4_DNA_MU
  specific = 4
FEATURE [App::DocumentObjectGroupPython] BioChemical  # scripted group (container) (typed FeaturePython)
  Group = -> [G4_CYTOSINE,G4_THYMINE,G4_URACIL,G4_DNA_ADENINE,G4_DNA_GUANINE,G4_DNA_CYTOSINE,G4_DNA_THYMINE,G4_DNA_URACIL,G4_DNA_ADENOSINE,G4_DNA_GUANOSINE,G4_DNA_CYTIDINE,G4_DNA_URIDINE,G4_DNA_METHYLURIDINE,G4_DNA_MONOPHOSPHATE,G4_DNA_A,G4_DNA_G,G4_DNA_C,G4_DNA_U,G4_DNA_MU]
FEATURE [App::DocumentObjectGroupPython] G4Materials  # scripted group (container) (typed FeaturePython)
  Group = -> [NIST,Element,HEP,Space,BioChemical]
  version = 1
FEATURE [App::DocumentObjectGroupPython] Geant4  # scripted group (container) (typed FeaturePython)
  Group = -> [G4Isotopes,G4Elements,G4Materials]
FEATURE [App::DocumentObjectGroupPython] Materials  # scripted group (container) (typed FeaturePython)
  Group = -> [Geant4]
FEATURE [Part::FeaturePython] GDMLBox_WorldBox  # WARN: FeaturePython — macro-defined, semantics opaque (R4)
  lunit = 2
  material = 5
  x = 100
  y = 100
  z = 100
FEATURE [Part::FeaturePython] GDMLBox_Box  # WARN: FeaturePython — macro-defined, semantics opaque (R4)
  lunit = 2
  material = 0
  x = 5
  y = 5
  z = 5
FEATURE [App::Part] LV_Box
  Group = -> [GDMLBox_Box]
  Origin = -> Origin001
  Placement = pos=(10,0,0) rot=(0,0,1;0rad)
FEATURE [Part::FeaturePython] Array  # Draft array (typed FeaturePython)
  Angle = 360
  ArrayType = 1
  Axis = (0,0,1)
  Base = -> LV_Box
  Center = (0,0,0)
  Count = 5
  Fuse = false
  IntervalAxis = (0,0,0)
  IntervalX = (50,0,0)
  IntervalY = (0,50,0)
  IntervalZ = (0,0,50)
  NumberCircles = 3
  NumberPolar = 5
  NumberX = 2
  NumberY = 2
  NumberZ = 1
  RadialDistance = 50
  Symmetry = 1
  TangentialDistance = 25
FEATURE [App::Part] Part001
  Group = -> [LV_Box,Array]
  Origin = -> Origin003
FEATURE [Part::FeaturePython] Array001  # Draft array (typed FeaturePython)
  Angle = 360
  ArrayType = 0
  Axis = (0,0,1)
  Base = -> Part001
  Center = (0,0,0)
  Count = 4
  Fuse = false
  IntervalAxis = (0,0,0)
  IntervalX = (50,0,0)
  IntervalY = (0,30,0)
  IntervalZ = (0,0,100)
  NumberCircles = 3
  NumberPolar = 5
  NumberX = 2
  NumberY = 2
  NumberZ = 1
  Placement = pos=(-20,-14,0) rot=(0,0,1;0rad)
  RadialDistance = 50
  Symmetry = 1
  TangentialDistance = 25
FEATURE [App::Part] Part
  Group = -> [Part001,Array001]
  Origin = -> Origin002
FEATURE [App::Part] worldVOL
  Group = -> [GDMLBox_WorldBox,Part]
  Origin = -> Origin
